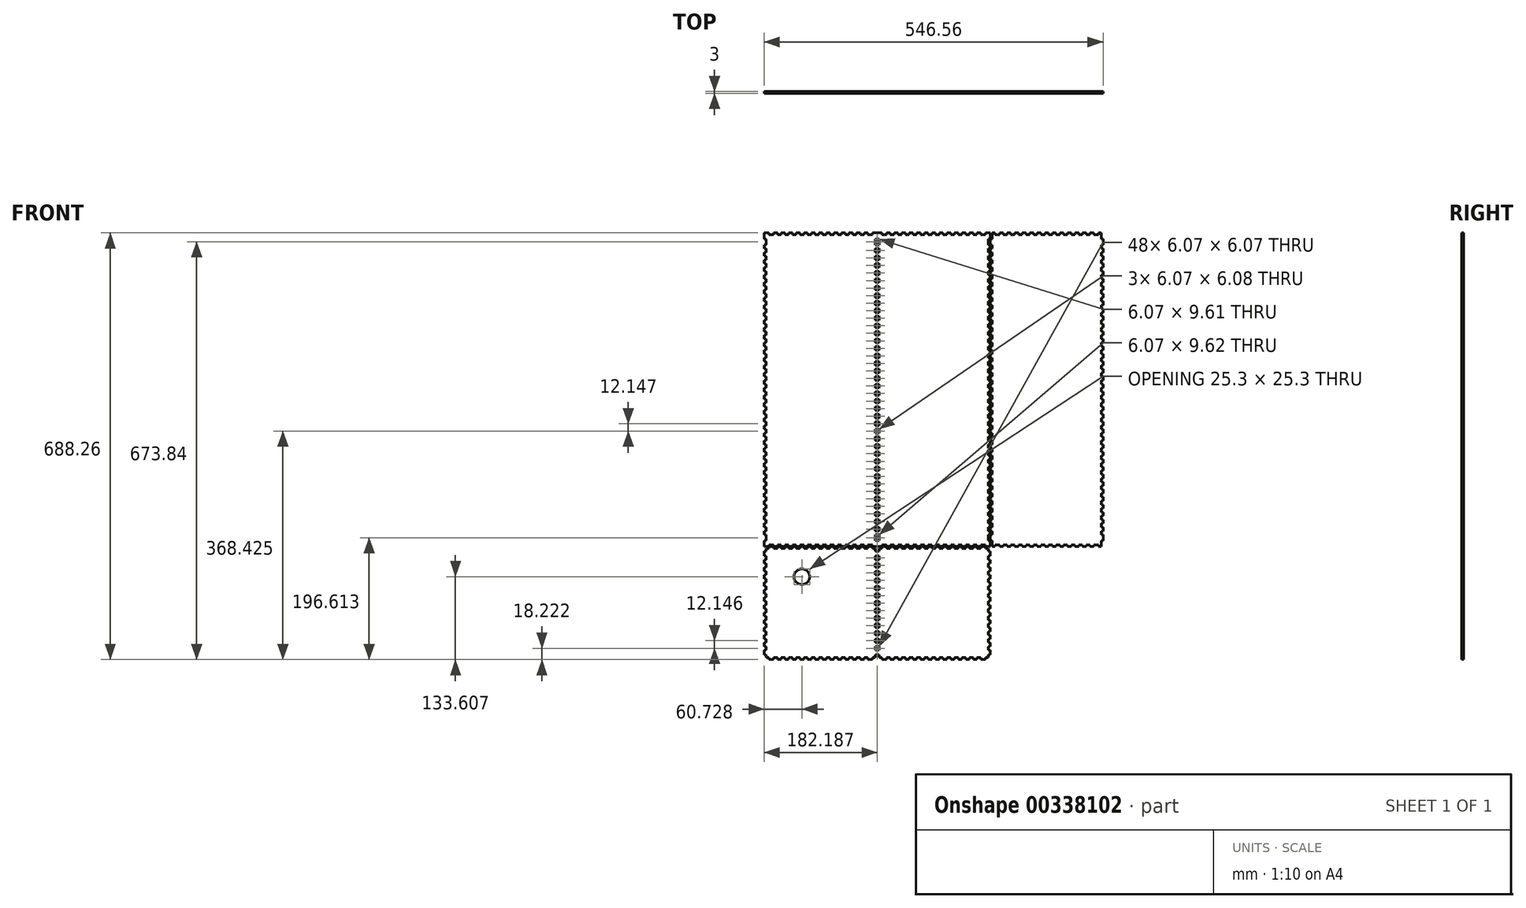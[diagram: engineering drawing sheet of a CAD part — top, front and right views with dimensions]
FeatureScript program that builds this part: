
annotation { "Feature Type Name" : "Feature", "Feature Type Description" : "" }
export const myFeature = defineFeature(function(context is Context, id is Id, definition is map)
    precondition{}
    {
        {
            var Q0;
            Q0=qCreatedBy(makeId("Front.planeOp"),FACE);
            var sketch = newSketch(context, id + "F0", { "sketchPlane" : qUnion([Q0])});
            skLineSegment(sketch, "E0", {"start": v(-273.28, 506.07) * mm, "end": v(-265.69, 506.07) * mm});
            skLineSegment(sketch, "E1", {"start": v(-265.69, 506.07) * mm, "end": v(-265.69, 503.04) * mm});
            skLineSegment(sketch, "E2", {"start": v(-265.69, 503.04) * mm, "end": v(-258.1, 503.04) * mm});
            skLineSegment(sketch, "E3", {"start": v(-258.1, 503.04) * mm, "end": v(-258.1, 506.07) * mm});
            skLineSegment(sketch, "E4", {"start": v(-258.1, 506.07) * mm, "end": v(-252.03, 506.07) * mm});
            skLineSegment(sketch, "E5", {"start": v(-252.03, 506.07) * mm, "end": v(-252.03, 503.04) * mm});
            skLineSegment(sketch, "E6", {"start": v(-252.03, 503.04) * mm, "end": v(-245.95, 503.04) * mm});
            skLineSegment(sketch, "E7", {"start": v(-245.95, 503.04) * mm, "end": v(-245.95, 506.07) * mm});
            skLineSegment(sketch, "E8", {"start": v(-245.95, 506.07) * mm, "end": v(-239.88, 506.07) * mm});
            skLineSegment(sketch, "E9", {"start": v(-239.88, 506.07) * mm, "end": v(-239.88, 503.04) * mm});
            skLineSegment(sketch, "E10", {"start": v(-239.88, 503.04) * mm, "end": v(-233.8, 503.04) * mm});
            skLineSegment(sketch, "E11", {"start": v(-233.8, 503.04) * mm, "end": v(-233.8, 506.07) * mm});
            skLineSegment(sketch, "E12", {"start": v(-233.8, 506.07) * mm, "end": v(-227.73, 506.07) * mm});
            skLineSegment(sketch, "E13", {"start": v(-227.73, 506.07) * mm, "end": v(-227.73, 503.04) * mm});
            skLineSegment(sketch, "E14", {"start": v(-227.73, 503.04) * mm, "end": v(-221.66, 503.04) * mm});
            skLineSegment(sketch, "E15", {"start": v(-221.66, 503.04) * mm, "end": v(-221.66, 506.07) * mm});
            skLineSegment(sketch, "E16", {"start": v(-221.66, 506.07) * mm, "end": v(-215.59, 506.07) * mm});
            skLineSegment(sketch, "E17", {"start": v(-215.59, 506.07) * mm, "end": v(-215.59, 503.04) * mm});
            skLineSegment(sketch, "E18", {"start": v(-215.59, 503.04) * mm, "end": v(-209.52, 503.04) * mm});
            skLineSegment(sketch, "E19", {"start": v(-209.52, 503.04) * mm, "end": v(-209.52, 506.07) * mm});
            skLineSegment(sketch, "E20", {"start": v(-209.52, 506.07) * mm, "end": v(-203.44, 506.07) * mm});
            skLineSegment(sketch, "E21", {"start": v(-203.44, 506.07) * mm, "end": v(-203.44, 503.04) * mm});
            skLineSegment(sketch, "E22", {"start": v(-203.44, 503.04) * mm, "end": v(-197.37, 503.04) * mm});
            skLineSegment(sketch, "E23", {"start": v(-197.37, 503.04) * mm, "end": v(-197.37, 506.07) * mm});
            skLineSegment(sketch, "E24", {"start": v(-197.37, 506.07) * mm, "end": v(-191.3, 506.07) * mm});
            skLineSegment(sketch, "E25", {"start": v(-191.3, 506.07) * mm, "end": v(-191.3, 503.04) * mm});
            skLineSegment(sketch, "E26", {"start": v(-191.3, 503.04) * mm, "end": v(-185.22, 503.04) * mm});
            skLineSegment(sketch, "E27", {"start": v(-185.22, 503.04) * mm, "end": v(-185.22, 506.07) * mm});
            skLineSegment(sketch, "E28", {"start": v(-185.22, 506.07) * mm, "end": v(-179.15, 506.07) * mm});
            skLineSegment(sketch, "E29", {"start": v(-179.15, 506.07) * mm, "end": v(-179.15, 503.04) * mm});
            skLineSegment(sketch, "E30", {"start": v(-179.15, 503.04) * mm, "end": v(-173.08, 503.04) * mm});
            skLineSegment(sketch, "E31", {"start": v(-173.08, 503.04) * mm, "end": v(-173.08, 506.07) * mm});
            skLineSegment(sketch, "E32", {"start": v(-173.08, 506.07) * mm, "end": v(-167, 506.07) * mm});
            skLineSegment(sketch, "E33", {"start": v(-167, 506.07) * mm, "end": v(-167, 503.04) * mm});
            skLineSegment(sketch, "E34", {"start": v(-167, 503.04) * mm, "end": v(-160.93, 503.04) * mm});
            skLineSegment(sketch, "E35", {"start": v(-160.93, 503.04) * mm, "end": v(-160.93, 506.07) * mm});
            skLineSegment(sketch, "E36", {"start": v(-160.93, 506.07) * mm, "end": v(-154.86, 506.07) * mm});
            skLineSegment(sketch, "E37", {"start": v(-154.86, 506.07) * mm, "end": v(-154.86, 503.04) * mm});
            skLineSegment(sketch, "E38", {"start": v(-154.86, 503.04) * mm, "end": v(-148.79, 503.04) * mm});
            skLineSegment(sketch, "E39", {"start": v(-148.79, 503.04) * mm, "end": v(-148.79, 506.07) * mm});
            skLineSegment(sketch, "E40", {"start": v(-148.79, 506.07) * mm, "end": v(-142.71, 506.07) * mm});
            skLineSegment(sketch, "E41", {"start": v(-142.71, 506.07) * mm, "end": v(-142.71, 503.04) * mm});
            skLineSegment(sketch, "E42", {"start": v(-142.71, 503.04) * mm, "end": v(-136.64, 503.04) * mm});
            skLineSegment(sketch, "E43", {"start": v(-136.64, 503.04) * mm, "end": v(-136.64, 506.07) * mm});
            skLineSegment(sketch, "E44", {"start": v(-136.64, 506.07) * mm, "end": v(-130.57, 506.07) * mm});
            skLineSegment(sketch, "E45", {"start": v(-130.57, 506.07) * mm, "end": v(-130.57, 503.04) * mm});
            skLineSegment(sketch, "E46", {"start": v(-130.57, 503.04) * mm, "end": v(-124.5, 503.04) * mm});
            skLineSegment(sketch, "E47", {"start": v(-124.5, 503.04) * mm, "end": v(-124.5, 506.07) * mm});
            skLineSegment(sketch, "E48", {"start": v(-124.5, 506.07) * mm, "end": v(-118.42, 506.07) * mm});
            skLineSegment(sketch, "E49", {"start": v(-118.42, 506.07) * mm, "end": v(-118.42, 503.04) * mm});
            skLineSegment(sketch, "E50", {"start": v(-118.42, 503.04) * mm, "end": v(-112.35, 503.04) * mm});
            skLineSegment(sketch, "E51", {"start": v(-112.35, 503.04) * mm, "end": v(-112.35, 506.07) * mm});
            skLineSegment(sketch, "E52", {"start": v(-112.35, 506.07) * mm, "end": v(-106.28, 506.07) * mm});
            skLineSegment(sketch, "E53", {"start": v(-106.28, 506.07) * mm, "end": v(-106.28, 503.04) * mm});
            skLineSegment(sketch, "E54", {"start": v(-106.28, 503.04) * mm, "end": v(-98.68, 503.04) * mm});
            skLineSegment(sketch, "E55", {"start": v(-98.68, 503.04) * mm, "end": v(-98.68, 506.07) * mm});
            skLineSegment(sketch, "E56", {"start": v(-98.68, 506.07) * mm, "end": v(-91.1, 506.07) * mm});
            skLineSegment(sketch, "E57", {"start": v(-91.1, 506.07) * mm, "end": v(-91.1, 496.46) * mm});
            skLineSegment(sketch, "E58", {"start": v(-91.1, 496.46) * mm, "end": v(-94.13, 496.46) * mm});
            skLineSegment(sketch, "E59", {"start": v(-94.13, 496.46) * mm, "end": v(-94.13, 486.84) * mm});
            skLineSegment(sketch, "E60", {"start": v(-94.13, 486.84) * mm, "end": v(-91.1, 486.84) * mm});
            skLineSegment(sketch, "E61", {"start": v(-91.1, 486.84) * mm, "end": v(-91.1, 480.77) * mm});
            skLineSegment(sketch, "E62", {"start": v(-91.1, 480.77) * mm, "end": v(-94.13, 480.77) * mm});
            skLineSegment(sketch, "E63", {"start": v(-94.13, 480.77) * mm, "end": v(-94.13, 474.7) * mm});
            skLineSegment(sketch, "E64", {"start": v(-94.13, 474.7) * mm, "end": v(-91.1, 474.7) * mm});
            skLineSegment(sketch, "E65", {"start": v(-91.1, 474.7) * mm, "end": v(-91.1, 468.62) * mm});
            skLineSegment(sketch, "E66", {"start": v(-91.1, 468.62) * mm, "end": v(-94.13, 468.62) * mm});
            skLineSegment(sketch, "E67", {"start": v(-94.13, 468.62) * mm, "end": v(-94.13, 462.55) * mm});
            skLineSegment(sketch, "E68", {"start": v(-94.13, 462.55) * mm, "end": v(-91.1, 462.55) * mm});
            skLineSegment(sketch, "E69", {"start": v(-91.1, 462.55) * mm, "end": v(-91.1, 456.48) * mm});
            skLineSegment(sketch, "E70", {"start": v(-91.1, 456.48) * mm, "end": v(-94.13, 456.48) * mm});
            skLineSegment(sketch, "E71", {"start": v(-94.13, 456.48) * mm, "end": v(-94.13, 450.4) * mm});
            skLineSegment(sketch, "E72", {"start": v(-94.13, 450.4) * mm, "end": v(-91.1, 450.4) * mm});
            skLineSegment(sketch, "E73", {"start": v(-91.1, 450.4) * mm, "end": v(-91.1, 444.33) * mm});
            skLineSegment(sketch, "E74", {"start": v(-91.1, 444.33) * mm, "end": v(-94.13, 444.33) * mm});
            skLineSegment(sketch, "E75", {"start": v(-94.13, 444.33) * mm, "end": v(-94.13, 438.26) * mm});
            skLineSegment(sketch, "E76", {"start": v(-94.13, 438.26) * mm, "end": v(-91.1, 438.26) * mm});
            skLineSegment(sketch, "E77", {"start": v(-91.1, 438.26) * mm, "end": v(-91.1, 432.18) * mm});
            skLineSegment(sketch, "E78", {"start": v(-91.1, 432.18) * mm, "end": v(-94.13, 432.18) * mm});
            skLineSegment(sketch, "E79", {"start": v(-94.13, 432.18) * mm, "end": v(-94.13, 426.11) * mm});
            skLineSegment(sketch, "E80", {"start": v(-94.13, 426.11) * mm, "end": v(-91.1, 426.11) * mm});
            skLineSegment(sketch, "E81", {"start": v(-91.1, 426.11) * mm, "end": v(-91.1, 420.04) * mm});
            skLineSegment(sketch, "E82", {"start": v(-91.1, 420.04) * mm, "end": v(-94.13, 420.04) * mm});
            skLineSegment(sketch, "E83", {"start": v(-94.13, 420.04) * mm, "end": v(-94.13, 413.97) * mm});
            skLineSegment(sketch, "E84", {"start": v(-94.13, 413.97) * mm, "end": v(-91.1, 413.97) * mm});
            skLineSegment(sketch, "E85", {"start": v(-91.1, 413.97) * mm, "end": v(-91.1, 407.9) * mm});
            skLineSegment(sketch, "E86", {"start": v(-91.1, 407.9) * mm, "end": v(-94.13, 407.9) * mm});
            skLineSegment(sketch, "E87", {"start": v(-94.13, 407.9) * mm, "end": v(-94.13, 401.82) * mm});
            skLineSegment(sketch, "E88", {"start": v(-94.13, 401.82) * mm, "end": v(-91.1, 401.82) * mm});
            skLineSegment(sketch, "E89", {"start": v(-91.1, 401.82) * mm, "end": v(-91.1, 395.75) * mm});
            skLineSegment(sketch, "E90", {"start": v(-91.1, 395.75) * mm, "end": v(-94.13, 395.75) * mm});
            skLineSegment(sketch, "E91", {"start": v(-94.13, 395.75) * mm, "end": v(-94.13, 389.68) * mm});
            skLineSegment(sketch, "E92", {"start": v(-94.13, 389.68) * mm, "end": v(-91.1, 389.68) * mm});
            skLineSegment(sketch, "E93", {"start": v(-91.1, 389.68) * mm, "end": v(-91.1, 383.6) * mm});
            skLineSegment(sketch, "E94", {"start": v(-91.1, 383.6) * mm, "end": v(-94.13, 383.6) * mm});
            skLineSegment(sketch, "E95", {"start": v(-94.13, 383.6) * mm, "end": v(-94.13, 377.53) * mm});
            skLineSegment(sketch, "E96", {"start": v(-94.13, 377.53) * mm, "end": v(-91.1, 377.53) * mm});
            skLineSegment(sketch, "E97", {"start": v(-91.1, 377.53) * mm, "end": v(-91.1, 371.46) * mm});
            skLineSegment(sketch, "E98", {"start": v(-91.1, 371.46) * mm, "end": v(-94.13, 371.46) * mm});
            skLineSegment(sketch, "E99", {"start": v(-94.13, 371.46) * mm, "end": v(-94.13, 365.39) * mm});
            skLineSegment(sketch, "E100", {"start": v(-94.13, 365.39) * mm, "end": v(-91.1, 365.39) * mm});
            skLineSegment(sketch, "E101", {"start": v(-91.1, 365.39) * mm, "end": v(-91.1, 359.31) * mm});
            skLineSegment(sketch, "E102", {"start": v(-91.1, 359.31) * mm, "end": v(-94.13, 359.31) * mm});
            skLineSegment(sketch, "E103", {"start": v(-94.13, 359.31) * mm, "end": v(-94.13, 353.24) * mm});
            skLineSegment(sketch, "E104", {"start": v(-94.13, 353.24) * mm, "end": v(-91.1, 353.24) * mm});
            skLineSegment(sketch, "E105", {"start": v(-91.1, 353.24) * mm, "end": v(-91.1, 347.16) * mm});
            skLineSegment(sketch, "E106", {"start": v(-91.1, 347.16) * mm, "end": v(-94.13, 347.16) * mm});
            skLineSegment(sketch, "E107", {"start": v(-94.13, 347.16) * mm, "end": v(-94.13, 341.1) * mm});
            skLineSegment(sketch, "E108", {"start": v(-94.13, 341.1) * mm, "end": v(-91.1, 341.1) * mm});
            skLineSegment(sketch, "E109", {"start": v(-91.1, 341.1) * mm, "end": v(-91.1, 335.02) * mm});
            skLineSegment(sketch, "E110", {"start": v(-91.1, 335.02) * mm, "end": v(-94.13, 335.02) * mm});
            skLineSegment(sketch, "E111", {"start": v(-94.13, 335.02) * mm, "end": v(-94.13, 328.95) * mm});
            skLineSegment(sketch, "E112", {"start": v(-94.13, 328.95) * mm, "end": v(-91.1, 328.95) * mm});
            skLineSegment(sketch, "E113", {"start": v(-91.1, 328.95) * mm, "end": v(-91.1, 322.87) * mm});
            skLineSegment(sketch, "E114", {"start": v(-91.1, 322.87) * mm, "end": v(-94.13, 322.87) * mm});
            skLineSegment(sketch, "E115", {"start": v(-94.13, 322.87) * mm, "end": v(-94.13, 316.8) * mm});
            skLineSegment(sketch, "E116", {"start": v(-94.13, 316.8) * mm, "end": v(-91.1, 316.8) * mm});
            skLineSegment(sketch, "E117", {"start": v(-91.1, 316.8) * mm, "end": v(-91.1, 310.73) * mm});
            skLineSegment(sketch, "E118", {"start": v(-91.1, 310.73) * mm, "end": v(-94.13, 310.73) * mm});
            skLineSegment(sketch, "E119", {"start": v(-94.13, 310.73) * mm, "end": v(-94.13, 304.66) * mm});
            skLineSegment(sketch, "E120", {"start": v(-94.13, 304.66) * mm, "end": v(-91.1, 304.66) * mm});
            skLineSegment(sketch, "E121", {"start": v(-91.1, 304.66) * mm, "end": v(-91.1, 298.58) * mm});
            skLineSegment(sketch, "E122", {"start": v(-91.1, 298.58) * mm, "end": v(-94.13, 298.58) * mm});
            skLineSegment(sketch, "E123", {"start": v(-94.13, 298.58) * mm, "end": v(-94.13, 292.51) * mm});
            skLineSegment(sketch, "E124", {"start": v(-94.13, 292.51) * mm, "end": v(-91.1, 292.51) * mm});
            skLineSegment(sketch, "E125", {"start": v(-91.1, 292.51) * mm, "end": v(-91.1, 286.44) * mm});
            skLineSegment(sketch, "E126", {"start": v(-91.1, 286.44) * mm, "end": v(-94.13, 286.44) * mm});
            skLineSegment(sketch, "E127", {"start": v(-94.13, 286.44) * mm, "end": v(-94.13, 280.37) * mm});
            skLineSegment(sketch, "E128", {"start": v(-94.13, 280.37) * mm, "end": v(-91.1, 280.37) * mm});
            skLineSegment(sketch, "E129", {"start": v(-91.1, 280.37) * mm, "end": v(-91.1, 274.3) * mm});
            skLineSegment(sketch, "E130", {"start": v(-91.1, 274.3) * mm, "end": v(-94.13, 274.3) * mm});
            skLineSegment(sketch, "E131", {"start": v(-94.13, 274.3) * mm, "end": v(-94.13, 268.22) * mm});
            skLineSegment(sketch, "E132", {"start": v(-94.13, 268.22) * mm, "end": v(-91.1, 268.22) * mm});
            skLineSegment(sketch, "E133", {"start": v(-91.1, 268.22) * mm, "end": v(-91.1, 262.15) * mm});
            skLineSegment(sketch, "E134", {"start": v(-91.1, 262.15) * mm, "end": v(-94.13, 262.15) * mm});
            skLineSegment(sketch, "E135", {"start": v(-94.13, 262.15) * mm, "end": v(-94.13, 256.07) * mm});
            skLineSegment(sketch, "E136", {"start": v(-94.13, 256.07) * mm, "end": v(-91.1, 256.07) * mm});
            skLineSegment(sketch, "E137", {"start": v(-91.1, 256.07) * mm, "end": v(-91.1, 250) * mm});
            skLineSegment(sketch, "E138", {"start": v(-91.1, 250) * mm, "end": v(-94.13, 250) * mm});
            skLineSegment(sketch, "E139", {"start": v(-94.13, 250) * mm, "end": v(-94.13, 243.93) * mm});
            skLineSegment(sketch, "E140", {"start": v(-94.13, 243.93) * mm, "end": v(-91.1, 243.93) * mm});
            skLineSegment(sketch, "E141", {"start": v(-91.1, 243.93) * mm, "end": v(-91.1, 237.85) * mm});
            skLineSegment(sketch, "E142", {"start": v(-91.1, 237.85) * mm, "end": v(-94.13, 237.85) * mm});
            skLineSegment(sketch, "E143", {"start": v(-94.13, 237.85) * mm, "end": v(-94.13, 231.78) * mm});
            skLineSegment(sketch, "E144", {"start": v(-94.13, 231.78) * mm, "end": v(-91.1, 231.78) * mm});
            skLineSegment(sketch, "E145", {"start": v(-91.1, 231.78) * mm, "end": v(-91.1, 225.7) * mm});
            skLineSegment(sketch, "E146", {"start": v(-91.1, 225.7) * mm, "end": v(-94.13, 225.7) * mm});
            skLineSegment(sketch, "E147", {"start": v(-94.13, 225.7) * mm, "end": v(-94.13, 219.64) * mm});
            skLineSegment(sketch, "E148", {"start": v(-94.13, 219.64) * mm, "end": v(-91.1, 219.64) * mm});
            skLineSegment(sketch, "E149", {"start": v(-91.1, 219.64) * mm, "end": v(-91.1, 213.56) * mm});
            skLineSegment(sketch, "E150", {"start": v(-91.1, 213.56) * mm, "end": v(-94.13, 213.56) * mm});
            skLineSegment(sketch, "E151", {"start": v(-94.13, 213.56) * mm, "end": v(-94.13, 207.49) * mm});
            skLineSegment(sketch, "E152", {"start": v(-94.13, 207.49) * mm, "end": v(-91.1, 207.49) * mm});
            skLineSegment(sketch, "E153", {"start": v(-91.1, 207.49) * mm, "end": v(-91.1, 201.42) * mm});
            skLineSegment(sketch, "E154", {"start": v(-91.1, 201.42) * mm, "end": v(-94.13, 201.42) * mm});
            skLineSegment(sketch, "E155", {"start": v(-94.13, 201.42) * mm, "end": v(-94.13, 195.34) * mm});
            skLineSegment(sketch, "E156", {"start": v(-94.13, 195.34) * mm, "end": v(-91.1, 195.34) * mm});
            skLineSegment(sketch, "E157", {"start": v(-91.1, 195.34) * mm, "end": v(-91.1, 189.27) * mm});
            skLineSegment(sketch, "E158", {"start": v(-91.1, 189.27) * mm, "end": v(-94.13, 189.27) * mm});
            skLineSegment(sketch, "E159", {"start": v(-94.13, 189.27) * mm, "end": v(-94.13, 183.2) * mm});
            skLineSegment(sketch, "E160", {"start": v(-94.13, 183.2) * mm, "end": v(-91.1, 183.2) * mm});
            skLineSegment(sketch, "E161", {"start": v(-91.1, 183.2) * mm, "end": v(-91.1, 177.13) * mm});
            skLineSegment(sketch, "E162", {"start": v(-91.1, 177.13) * mm, "end": v(-94.13, 177.13) * mm});
            skLineSegment(sketch, "E163", {"start": v(-94.13, 177.13) * mm, "end": v(-94.13, 171.06) * mm});
            skLineSegment(sketch, "E164", {"start": v(-94.13, 171.06) * mm, "end": v(-91.1, 171.06) * mm});
            skLineSegment(sketch, "E165", {"start": v(-91.1, 171.06) * mm, "end": v(-91.1, 164.98) * mm});
            skLineSegment(sketch, "E166", {"start": v(-91.1, 164.98) * mm, "end": v(-94.13, 164.98) * mm});
            skLineSegment(sketch, "E167", {"start": v(-94.13, 164.98) * mm, "end": v(-94.13, 158.9) * mm});
            skLineSegment(sketch, "E168", {"start": v(-94.13, 158.9) * mm, "end": v(-91.1, 158.9) * mm});
            skLineSegment(sketch, "E169", {"start": v(-91.1, 158.9) * mm, "end": v(-91.1, 152.83) * mm});
            skLineSegment(sketch, "E170", {"start": v(-91.1, 152.83) * mm, "end": v(-94.13, 152.83) * mm});
            skLineSegment(sketch, "E171", {"start": v(-94.13, 152.83) * mm, "end": v(-94.13, 146.76) * mm});
            skLineSegment(sketch, "E172", {"start": v(-94.13, 146.76) * mm, "end": v(-91.1, 146.76) * mm});
            skLineSegment(sketch, "E173", {"start": v(-91.1, 146.76) * mm, "end": v(-91.1, 140.69) * mm});
            skLineSegment(sketch, "E174", {"start": v(-91.1, 140.69) * mm, "end": v(-94.13, 140.69) * mm});
            skLineSegment(sketch, "E175", {"start": v(-94.13, 140.69) * mm, "end": v(-94.13, 134.62) * mm});
            skLineSegment(sketch, "E176", {"start": v(-94.13, 134.62) * mm, "end": v(-91.1, 134.62) * mm});
            skLineSegment(sketch, "E177", {"start": v(-91.1, 134.62) * mm, "end": v(-91.1, 128.54) * mm});
            skLineSegment(sketch, "E178", {"start": v(-91.1, 128.54) * mm, "end": v(-94.13, 128.54) * mm});
            skLineSegment(sketch, "E179", {"start": v(-94.13, 128.54) * mm, "end": v(-94.13, 122.47) * mm});
            skLineSegment(sketch, "E180", {"start": v(-94.13, 122.47) * mm, "end": v(-91.1, 122.47) * mm});
            skLineSegment(sketch, "E181", {"start": v(-91.1, 122.47) * mm, "end": v(-91.1, 116.4) * mm});
            skLineSegment(sketch, "E182", {"start": v(-91.1, 116.4) * mm, "end": v(-94.13, 116.4) * mm});
            skLineSegment(sketch, "E183", {"start": v(-94.13, 116.4) * mm, "end": v(-94.13, 110.32) * mm});
            skLineSegment(sketch, "E184", {"start": v(-94.13, 110.32) * mm, "end": v(-91.1, 110.32) * mm});
            skLineSegment(sketch, "E185", {"start": v(-91.1, 110.32) * mm, "end": v(-91.1, 104.25) * mm});
            skLineSegment(sketch, "E186", {"start": v(-91.1, 104.25) * mm, "end": v(-94.13, 104.25) * mm});
            skLineSegment(sketch, "E187", {"start": v(-94.13, 104.25) * mm, "end": v(-94.13, 98.18) * mm});
            skLineSegment(sketch, "E188", {"start": v(-94.13, 98.18) * mm, "end": v(-91.1, 98.18) * mm});
            skLineSegment(sketch, "E189", {"start": v(-91.1, 98.18) * mm, "end": v(-91.1, 92.1) * mm});
            skLineSegment(sketch, "E190", {"start": v(-91.1, 92.1) * mm, "end": v(-94.13, 92.1) * mm});
            skLineSegment(sketch, "E191", {"start": v(-94.13, 92.1) * mm, "end": v(-94.13, 86.03) * mm});
            skLineSegment(sketch, "E192", {"start": v(-94.13, 86.03) * mm, "end": v(-91.1, 86.03) * mm});
            skLineSegment(sketch, "E193", {"start": v(-91.1, 86.03) * mm, "end": v(-91.1, 79.96) * mm});
            skLineSegment(sketch, "E194", {"start": v(-91.1, 79.96) * mm, "end": v(-94.13, 79.96) * mm});
            skLineSegment(sketch, "E195", {"start": v(-94.13, 79.96) * mm, "end": v(-94.13, 73.89) * mm});
            skLineSegment(sketch, "E196", {"start": v(-94.13, 73.89) * mm, "end": v(-91.1, 73.89) * mm});
            skLineSegment(sketch, "E197", {"start": v(-91.1, 73.89) * mm, "end": v(-91.1, 67.81) * mm});
            skLineSegment(sketch, "E198", {"start": v(-91.1, 67.81) * mm, "end": v(-94.13, 67.81) * mm});
            skLineSegment(sketch, "E199", {"start": v(-94.13, 67.81) * mm, "end": v(-94.13, 61.74) * mm});
            skLineSegment(sketch, "E200", {"start": v(-94.13, 61.74) * mm, "end": v(-91.1, 61.74) * mm});
            skLineSegment(sketch, "E201", {"start": v(-91.1, 61.74) * mm, "end": v(-91.1, 55.67) * mm});
            skLineSegment(sketch, "E202", {"start": v(-91.1, 55.67) * mm, "end": v(-94.13, 55.67) * mm});
            skLineSegment(sketch, "E203", {"start": v(-94.13, 55.67) * mm, "end": v(-94.13, 49.6) * mm});
            skLineSegment(sketch, "E204", {"start": v(-94.13, 49.6) * mm, "end": v(-91.1, 49.6) * mm});
            skLineSegment(sketch, "E205", {"start": v(-91.1, 49.6) * mm, "end": v(-91.1, 43.52) * mm});
            skLineSegment(sketch, "E206", {"start": v(-91.1, 43.52) * mm, "end": v(-94.13, 43.52) * mm});
            skLineSegment(sketch, "E207", {"start": v(-94.13, 43.52) * mm, "end": v(-94.13, 37.45) * mm});
            skLineSegment(sketch, "E208", {"start": v(-94.13, 37.45) * mm, "end": v(-91.1, 37.45) * mm});
            skLineSegment(sketch, "E209", {"start": v(-91.1, 37.45) * mm, "end": v(-91.1, 31.38) * mm});
            skLineSegment(sketch, "E210", {"start": v(-91.1, 31.38) * mm, "end": v(-94.13, 31.38) * mm});
            skLineSegment(sketch, "E211", {"start": v(-94.13, 31.38) * mm, "end": v(-94.13, 25.3) * mm});
            skLineSegment(sketch, "E212", {"start": v(-94.13, 25.3) * mm, "end": v(-91.1, 25.3) * mm});
            skLineSegment(sketch, "E213", {"start": v(-91.1, 25.3) * mm, "end": v(-91.1, 19.23) * mm});
            skLineSegment(sketch, "E214", {"start": v(-91.1, 19.23) * mm, "end": v(-94.13, 19.23) * mm});
            skLineSegment(sketch, "E215", {"start": v(-94.13, 19.23) * mm, "end": v(-94.13, 9.62) * mm});
            skLineSegment(sketch, "E216", {"start": v(-94.13, 9.62) * mm, "end": v(-91.1, 9.62) * mm});
            skLineSegment(sketch, "E217", {"start": v(-91.1, 9.62) * mm, "end": v(-91.1, 0) * mm});
            skLineSegment(sketch, "E218", {"start": v(-91.1, 0) * mm, "end": v(-98.68, 0) * mm});
            skLineSegment(sketch, "E219", {"start": v(-98.68, 0) * mm, "end": v(-98.68, 3.04) * mm});
            skLineSegment(sketch, "E220", {"start": v(-98.68, 3.04) * mm, "end": v(-106.28, 3.04) * mm});
            skLineSegment(sketch, "E221", {"start": v(-106.28, 3.04) * mm, "end": v(-106.28, 0) * mm});
            skLineSegment(sketch, "E222", {"start": v(-106.28, 0) * mm, "end": v(-112.35, 0) * mm});
            skLineSegment(sketch, "E223", {"start": v(-112.35, 0) * mm, "end": v(-112.35, 3.04) * mm});
            skLineSegment(sketch, "E224", {"start": v(-112.35, 3.04) * mm, "end": v(-118.42, 3.04) * mm});
            skLineSegment(sketch, "E225", {"start": v(-118.42, 3.04) * mm, "end": v(-118.42, 0) * mm});
            skLineSegment(sketch, "E226", {"start": v(-118.42, 0) * mm, "end": v(-124.5, 0) * mm});
            skLineSegment(sketch, "E227", {"start": v(-124.5, 0) * mm, "end": v(-124.5, 3.04) * mm});
            skLineSegment(sketch, "E228", {"start": v(-124.5, 3.04) * mm, "end": v(-130.57, 3.04) * mm});
            skLineSegment(sketch, "E229", {"start": v(-130.57, 3.04) * mm, "end": v(-130.57, 0) * mm});
            skLineSegment(sketch, "E230", {"start": v(-130.57, 0) * mm, "end": v(-136.64, 0) * mm});
            skLineSegment(sketch, "E231", {"start": v(-136.64, 0) * mm, "end": v(-136.64, 3.04) * mm});
            skLineSegment(sketch, "E232", {"start": v(-136.64, 3.04) * mm, "end": v(-142.71, 3.04) * mm});
            skLineSegment(sketch, "E233", {"start": v(-142.71, 3.04) * mm, "end": v(-142.71, 0) * mm});
            skLineSegment(sketch, "E234", {"start": v(-142.71, 0) * mm, "end": v(-148.79, 0) * mm});
            skLineSegment(sketch, "E235", {"start": v(-148.79, 0) * mm, "end": v(-148.79, 3.04) * mm});
            skLineSegment(sketch, "E236", {"start": v(-148.79, 3.04) * mm, "end": v(-154.86, 3.04) * mm});
            skLineSegment(sketch, "E237", {"start": v(-154.86, 3.04) * mm, "end": v(-154.86, 0) * mm});
            skLineSegment(sketch, "E238", {"start": v(-154.86, 0) * mm, "end": v(-160.93, 0) * mm});
            skLineSegment(sketch, "E239", {"start": v(-160.93, 0) * mm, "end": v(-160.93, 3.04) * mm});
            skLineSegment(sketch, "E240", {"start": v(-160.93, 3.04) * mm, "end": v(-167, 3.04) * mm});
            skLineSegment(sketch, "E241", {"start": v(-167, 3.04) * mm, "end": v(-167, 0) * mm});
            skLineSegment(sketch, "E242", {"start": v(-167, 0) * mm, "end": v(-173.08, 0) * mm});
            skLineSegment(sketch, "E243", {"start": v(-173.08, 0) * mm, "end": v(-173.08, 3.04) * mm});
            skLineSegment(sketch, "E244", {"start": v(-173.08, 3.04) * mm, "end": v(-179.15, 3.04) * mm});
            skLineSegment(sketch, "E245", {"start": v(-179.15, 3.04) * mm, "end": v(-179.15, 0) * mm});
            skLineSegment(sketch, "E246", {"start": v(-179.15, 0) * mm, "end": v(-185.22, 0) * mm});
            skLineSegment(sketch, "E247", {"start": v(-185.22, 0) * mm, "end": v(-185.22, 3.04) * mm});
            skLineSegment(sketch, "E248", {"start": v(-185.22, 3.04) * mm, "end": v(-191.3, 3.04) * mm});
            skLineSegment(sketch, "E249", {"start": v(-191.3, 3.04) * mm, "end": v(-191.3, 0) * mm});
            skLineSegment(sketch, "E250", {"start": v(-191.3, 0) * mm, "end": v(-197.37, 0) * mm});
            skLineSegment(sketch, "E251", {"start": v(-197.37, 0) * mm, "end": v(-197.37, 3.04) * mm});
            skLineSegment(sketch, "E252", {"start": v(-197.37, 3.04) * mm, "end": v(-203.44, 3.04) * mm});
            skLineSegment(sketch, "E253", {"start": v(-203.44, 3.04) * mm, "end": v(-203.44, 0) * mm});
            skLineSegment(sketch, "E254", {"start": v(-203.44, 0) * mm, "end": v(-209.52, 0) * mm});
            skLineSegment(sketch, "E255", {"start": v(-209.52, 0) * mm, "end": v(-209.52, 3.04) * mm});
            skLineSegment(sketch, "E256", {"start": v(-209.52, 3.04) * mm, "end": v(-215.59, 3.04) * mm});
            skLineSegment(sketch, "E257", {"start": v(-215.59, 3.04) * mm, "end": v(-215.59, 0) * mm});
            skLineSegment(sketch, "E258", {"start": v(-215.59, 0) * mm, "end": v(-221.66, 0) * mm});
            skLineSegment(sketch, "E259", {"start": v(-221.66, 0) * mm, "end": v(-221.66, 3.04) * mm});
            skLineSegment(sketch, "E260", {"start": v(-221.66, 3.04) * mm, "end": v(-227.73, 3.04) * mm});
            skLineSegment(sketch, "E261", {"start": v(-227.73, 3.04) * mm, "end": v(-227.73, 0) * mm});
            skLineSegment(sketch, "E262", {"start": v(-227.73, 0) * mm, "end": v(-233.8, 0) * mm});
            skLineSegment(sketch, "E263", {"start": v(-233.8, 0) * mm, "end": v(-233.8, 3.04) * mm});
            skLineSegment(sketch, "E264", {"start": v(-233.8, 3.04) * mm, "end": v(-239.88, 3.04) * mm});
            skLineSegment(sketch, "E265", {"start": v(-239.88, 3.04) * mm, "end": v(-239.88, 0) * mm});
            skLineSegment(sketch, "E266", {"start": v(-239.88, 0) * mm, "end": v(-245.95, 0) * mm});
            skLineSegment(sketch, "E267", {"start": v(-245.95, 0) * mm, "end": v(-245.95, 3.04) * mm});
            skLineSegment(sketch, "E268", {"start": v(-245.95, 3.04) * mm, "end": v(-252.03, 3.04) * mm});
            skLineSegment(sketch, "E269", {"start": v(-252.03, 3.04) * mm, "end": v(-252.03, 0) * mm});
            skLineSegment(sketch, "E270", {"start": v(-252.03, 0) * mm, "end": v(-258.1, 0) * mm});
            skLineSegment(sketch, "E271", {"start": v(-258.1, 0) * mm, "end": v(-258.1, 3.04) * mm});
            skLineSegment(sketch, "E272", {"start": v(-258.1, 3.04) * mm, "end": v(-265.69, 3.04) * mm});
            skLineSegment(sketch, "E273", {"start": v(-265.69, 3.04) * mm, "end": v(-265.69, 0) * mm});
            skLineSegment(sketch, "E274", {"start": v(-265.69, 0) * mm, "end": v(-273.28, 0) * mm});
            skLineSegment(sketch, "E275", {"start": v(-273.28, 0) * mm, "end": v(-273.28, 9.62) * mm});
            skLineSegment(sketch, "E276", {"start": v(-273.28, 9.62) * mm, "end": v(-270.24, 9.62) * mm});
            skLineSegment(sketch, "E277", {"start": v(-270.24, 9.62) * mm, "end": v(-270.24, 19.23) * mm});
            skLineSegment(sketch, "E278", {"start": v(-270.24, 19.23) * mm, "end": v(-273.28, 19.23) * mm});
            skLineSegment(sketch, "E279", {"start": v(-273.28, 19.23) * mm, "end": v(-273.28, 25.3) * mm});
            skLineSegment(sketch, "E280", {"start": v(-273.28, 25.3) * mm, "end": v(-270.24, 25.3) * mm});
            skLineSegment(sketch, "E281", {"start": v(-270.24, 25.3) * mm, "end": v(-270.24, 31.38) * mm});
            skLineSegment(sketch, "E282", {"start": v(-270.24, 31.38) * mm, "end": v(-273.28, 31.38) * mm});
            skLineSegment(sketch, "E283", {"start": v(-273.28, 31.38) * mm, "end": v(-273.28, 37.45) * mm});
            skLineSegment(sketch, "E284", {"start": v(-273.28, 37.45) * mm, "end": v(-270.24, 37.45) * mm});
            skLineSegment(sketch, "E285", {"start": v(-270.24, 37.45) * mm, "end": v(-270.24, 43.52) * mm});
            skLineSegment(sketch, "E286", {"start": v(-270.24, 43.52) * mm, "end": v(-273.28, 43.52) * mm});
            skLineSegment(sketch, "E287", {"start": v(-273.28, 43.52) * mm, "end": v(-273.28, 49.6) * mm});
            skLineSegment(sketch, "E288", {"start": v(-273.28, 49.6) * mm, "end": v(-270.24, 49.6) * mm});
            skLineSegment(sketch, "E289", {"start": v(-270.24, 49.6) * mm, "end": v(-270.24, 55.67) * mm});
            skLineSegment(sketch, "E290", {"start": v(-270.24, 55.67) * mm, "end": v(-273.28, 55.67) * mm});
            skLineSegment(sketch, "E291", {"start": v(-273.28, 55.67) * mm, "end": v(-273.28, 61.74) * mm});
            skLineSegment(sketch, "E292", {"start": v(-273.28, 61.74) * mm, "end": v(-270.24, 61.74) * mm});
            skLineSegment(sketch, "E293", {"start": v(-270.24, 61.74) * mm, "end": v(-270.24, 67.81) * mm});
            skLineSegment(sketch, "E294", {"start": v(-270.24, 67.81) * mm, "end": v(-273.28, 67.81) * mm});
            skLineSegment(sketch, "E295", {"start": v(-273.28, 67.81) * mm, "end": v(-273.28, 73.89) * mm});
            skLineSegment(sketch, "E296", {"start": v(-273.28, 73.89) * mm, "end": v(-270.24, 73.89) * mm});
            skLineSegment(sketch, "E297", {"start": v(-270.24, 73.89) * mm, "end": v(-270.24, 79.96) * mm});
            skLineSegment(sketch, "E298", {"start": v(-270.24, 79.96) * mm, "end": v(-273.28, 79.96) * mm});
            skLineSegment(sketch, "E299", {"start": v(-273.28, 79.96) * mm, "end": v(-273.28, 86.03) * mm});
            skLineSegment(sketch, "E300", {"start": v(-273.28, 86.03) * mm, "end": v(-270.24, 86.03) * mm});
            skLineSegment(sketch, "E301", {"start": v(-270.24, 86.03) * mm, "end": v(-270.24, 92.1) * mm});
            skLineSegment(sketch, "E302", {"start": v(-270.24, 92.1) * mm, "end": v(-273.28, 92.1) * mm});
            skLineSegment(sketch, "E303", {"start": v(-273.28, 92.1) * mm, "end": v(-273.28, 98.18) * mm});
            skLineSegment(sketch, "E304", {"start": v(-273.28, 98.18) * mm, "end": v(-270.24, 98.18) * mm});
            skLineSegment(sketch, "E305", {"start": v(-270.24, 98.18) * mm, "end": v(-270.24, 104.25) * mm});
            skLineSegment(sketch, "E306", {"start": v(-270.24, 104.25) * mm, "end": v(-273.28, 104.25) * mm});
            skLineSegment(sketch, "E307", {"start": v(-273.28, 104.25) * mm, "end": v(-273.28, 110.32) * mm});
            skLineSegment(sketch, "E308", {"start": v(-273.28, 110.32) * mm, "end": v(-270.24, 110.32) * mm});
            skLineSegment(sketch, "E309", {"start": v(-270.24, 110.32) * mm, "end": v(-270.24, 116.4) * mm});
            skLineSegment(sketch, "E310", {"start": v(-270.24, 116.4) * mm, "end": v(-273.28, 116.4) * mm});
            skLineSegment(sketch, "E311", {"start": v(-273.28, 116.4) * mm, "end": v(-273.28, 122.47) * mm});
            skLineSegment(sketch, "E312", {"start": v(-273.28, 122.47) * mm, "end": v(-270.24, 122.47) * mm});
            skLineSegment(sketch, "E313", {"start": v(-270.24, 122.47) * mm, "end": v(-270.24, 128.54) * mm});
            skLineSegment(sketch, "E314", {"start": v(-270.24, 128.54) * mm, "end": v(-273.28, 128.54) * mm});
            skLineSegment(sketch, "E315", {"start": v(-273.28, 128.54) * mm, "end": v(-273.28, 134.62) * mm});
            skLineSegment(sketch, "E316", {"start": v(-273.28, 134.62) * mm, "end": v(-270.24, 134.62) * mm});
            skLineSegment(sketch, "E317", {"start": v(-270.24, 134.62) * mm, "end": v(-270.24, 140.69) * mm});
            skLineSegment(sketch, "E318", {"start": v(-270.24, 140.69) * mm, "end": v(-273.28, 140.69) * mm});
            skLineSegment(sketch, "E319", {"start": v(-273.28, 140.69) * mm, "end": v(-273.28, 146.76) * mm});
            skLineSegment(sketch, "E320", {"start": v(-273.28, 146.76) * mm, "end": v(-270.24, 146.76) * mm});
            skLineSegment(sketch, "E321", {"start": v(-270.24, 146.76) * mm, "end": v(-270.24, 152.83) * mm});
            skLineSegment(sketch, "E322", {"start": v(-270.24, 152.83) * mm, "end": v(-273.28, 152.83) * mm});
            skLineSegment(sketch, "E323", {"start": v(-273.28, 152.83) * mm, "end": v(-273.28, 158.9) * mm});
            skLineSegment(sketch, "E324", {"start": v(-273.28, 158.9) * mm, "end": v(-270.24, 158.9) * mm});
            skLineSegment(sketch, "E325", {"start": v(-270.24, 158.9) * mm, "end": v(-270.24, 164.98) * mm});
            skLineSegment(sketch, "E326", {"start": v(-270.24, 164.98) * mm, "end": v(-273.28, 164.98) * mm});
            skLineSegment(sketch, "E327", {"start": v(-273.28, 164.98) * mm, "end": v(-273.28, 171.06) * mm});
            skLineSegment(sketch, "E328", {"start": v(-273.28, 171.06) * mm, "end": v(-270.24, 171.06) * mm});
            skLineSegment(sketch, "E329", {"start": v(-270.24, 171.06) * mm, "end": v(-270.24, 177.13) * mm});
            skLineSegment(sketch, "E330", {"start": v(-270.24, 177.13) * mm, "end": v(-273.28, 177.13) * mm});
            skLineSegment(sketch, "E331", {"start": v(-273.28, 177.13) * mm, "end": v(-273.28, 183.2) * mm});
            skLineSegment(sketch, "E332", {"start": v(-273.28, 183.2) * mm, "end": v(-270.24, 183.2) * mm});
            skLineSegment(sketch, "E333", {"start": v(-270.24, 183.2) * mm, "end": v(-270.24, 189.27) * mm});
            skLineSegment(sketch, "E334", {"start": v(-270.24, 189.27) * mm, "end": v(-273.28, 189.27) * mm});
            skLineSegment(sketch, "E335", {"start": v(-273.28, 189.27) * mm, "end": v(-273.28, 195.34) * mm});
            skLineSegment(sketch, "E336", {"start": v(-273.28, 195.34) * mm, "end": v(-270.24, 195.34) * mm});
            skLineSegment(sketch, "E337", {"start": v(-270.24, 195.34) * mm, "end": v(-270.24, 201.42) * mm});
            skLineSegment(sketch, "E338", {"start": v(-270.24, 201.42) * mm, "end": v(-273.28, 201.42) * mm});
            skLineSegment(sketch, "E339", {"start": v(-273.28, 201.42) * mm, "end": v(-273.28, 207.49) * mm});
            skLineSegment(sketch, "E340", {"start": v(-273.28, 207.49) * mm, "end": v(-270.24, 207.49) * mm});
            skLineSegment(sketch, "E341", {"start": v(-270.24, 207.49) * mm, "end": v(-270.24, 213.56) * mm});
            skLineSegment(sketch, "E342", {"start": v(-270.24, 213.56) * mm, "end": v(-273.28, 213.56) * mm});
            skLineSegment(sketch, "E343", {"start": v(-273.28, 213.56) * mm, "end": v(-273.28, 219.64) * mm});
            skLineSegment(sketch, "E344", {"start": v(-273.28, 219.64) * mm, "end": v(-270.24, 219.64) * mm});
            skLineSegment(sketch, "E345", {"start": v(-270.24, 219.64) * mm, "end": v(-270.24, 225.7) * mm});
            skLineSegment(sketch, "E346", {"start": v(-270.24, 225.7) * mm, "end": v(-273.28, 225.7) * mm});
            skLineSegment(sketch, "E347", {"start": v(-273.28, 225.7) * mm, "end": v(-273.28, 231.78) * mm});
            skLineSegment(sketch, "E348", {"start": v(-273.28, 231.78) * mm, "end": v(-270.24, 231.78) * mm});
            skLineSegment(sketch, "E349", {"start": v(-270.24, 231.78) * mm, "end": v(-270.24, 237.85) * mm});
            skLineSegment(sketch, "E350", {"start": v(-270.24, 237.85) * mm, "end": v(-273.28, 237.85) * mm});
            skLineSegment(sketch, "E351", {"start": v(-273.28, 237.85) * mm, "end": v(-273.28, 243.93) * mm});
            skLineSegment(sketch, "E352", {"start": v(-273.28, 243.93) * mm, "end": v(-270.24, 243.93) * mm});
            skLineSegment(sketch, "E353", {"start": v(-270.24, 243.93) * mm, "end": v(-270.24, 250) * mm});
            skLineSegment(sketch, "E354", {"start": v(-270.24, 250) * mm, "end": v(-273.28, 250) * mm});
            skLineSegment(sketch, "E355", {"start": v(-273.28, 250) * mm, "end": v(-273.28, 256.07) * mm});
            skLineSegment(sketch, "E356", {"start": v(-273.28, 256.07) * mm, "end": v(-270.24, 256.07) * mm});
            skLineSegment(sketch, "E357", {"start": v(-270.24, 256.07) * mm, "end": v(-270.24, 262.15) * mm});
            skLineSegment(sketch, "E358", {"start": v(-270.24, 262.15) * mm, "end": v(-273.28, 262.15) * mm});
            skLineSegment(sketch, "E359", {"start": v(-273.28, 262.15) * mm, "end": v(-273.28, 268.22) * mm});
            skLineSegment(sketch, "E360", {"start": v(-273.28, 268.22) * mm, "end": v(-270.24, 268.22) * mm});
            skLineSegment(sketch, "E361", {"start": v(-270.24, 268.22) * mm, "end": v(-270.24, 274.3) * mm});
            skLineSegment(sketch, "E362", {"start": v(-270.24, 274.3) * mm, "end": v(-273.28, 274.3) * mm});
            skLineSegment(sketch, "E363", {"start": v(-273.28, 274.3) * mm, "end": v(-273.28, 280.37) * mm});
            skLineSegment(sketch, "E364", {"start": v(-273.28, 280.37) * mm, "end": v(-270.24, 280.37) * mm});
            skLineSegment(sketch, "E365", {"start": v(-270.24, 280.37) * mm, "end": v(-270.24, 286.44) * mm});
            skLineSegment(sketch, "E366", {"start": v(-270.24, 286.44) * mm, "end": v(-273.28, 286.44) * mm});
            skLineSegment(sketch, "E367", {"start": v(-273.28, 286.44) * mm, "end": v(-273.28, 292.51) * mm});
            skLineSegment(sketch, "E368", {"start": v(-273.28, 292.51) * mm, "end": v(-270.24, 292.51) * mm});
            skLineSegment(sketch, "E369", {"start": v(-270.24, 292.51) * mm, "end": v(-270.24, 298.58) * mm});
            skLineSegment(sketch, "E370", {"start": v(-270.24, 298.58) * mm, "end": v(-273.28, 298.58) * mm});
            skLineSegment(sketch, "E371", {"start": v(-273.28, 298.58) * mm, "end": v(-273.28, 304.66) * mm});
            skLineSegment(sketch, "E372", {"start": v(-273.28, 304.66) * mm, "end": v(-270.24, 304.66) * mm});
            skLineSegment(sketch, "E373", {"start": v(-270.24, 304.66) * mm, "end": v(-270.24, 310.73) * mm});
            skLineSegment(sketch, "E374", {"start": v(-270.24, 310.73) * mm, "end": v(-273.28, 310.73) * mm});
            skLineSegment(sketch, "E375", {"start": v(-273.28, 310.73) * mm, "end": v(-273.28, 316.8) * mm});
            skLineSegment(sketch, "E376", {"start": v(-273.28, 316.8) * mm, "end": v(-270.24, 316.8) * mm});
            skLineSegment(sketch, "E377", {"start": v(-270.24, 316.8) * mm, "end": v(-270.24, 322.87) * mm});
            skLineSegment(sketch, "E378", {"start": v(-270.24, 322.87) * mm, "end": v(-273.28, 322.87) * mm});
            skLineSegment(sketch, "E379", {"start": v(-273.28, 322.87) * mm, "end": v(-273.28, 328.95) * mm});
            skLineSegment(sketch, "E380", {"start": v(-273.28, 328.95) * mm, "end": v(-270.24, 328.95) * mm});
            skLineSegment(sketch, "E381", {"start": v(-270.24, 328.95) * mm, "end": v(-270.24, 335.02) * mm});
            skLineSegment(sketch, "E382", {"start": v(-270.24, 335.02) * mm, "end": v(-273.28, 335.02) * mm});
            skLineSegment(sketch, "E383", {"start": v(-273.28, 335.02) * mm, "end": v(-273.28, 341.1) * mm});
            skLineSegment(sketch, "E384", {"start": v(-273.28, 341.1) * mm, "end": v(-270.24, 341.1) * mm});
            skLineSegment(sketch, "E385", {"start": v(-270.24, 341.1) * mm, "end": v(-270.24, 347.16) * mm});
            skLineSegment(sketch, "E386", {"start": v(-270.24, 347.16) * mm, "end": v(-273.28, 347.16) * mm});
            skLineSegment(sketch, "E387", {"start": v(-273.28, 347.16) * mm, "end": v(-273.28, 353.24) * mm});
            skLineSegment(sketch, "E388", {"start": v(-273.28, 353.24) * mm, "end": v(-270.24, 353.24) * mm});
            skLineSegment(sketch, "E389", {"start": v(-270.24, 353.24) * mm, "end": v(-270.24, 359.31) * mm});
            skLineSegment(sketch, "E390", {"start": v(-270.24, 359.31) * mm, "end": v(-273.28, 359.31) * mm});
            skLineSegment(sketch, "E391", {"start": v(-273.28, 359.31) * mm, "end": v(-273.28, 365.39) * mm});
            skLineSegment(sketch, "E392", {"start": v(-273.28, 365.39) * mm, "end": v(-270.24, 365.39) * mm});
            skLineSegment(sketch, "E393", {"start": v(-270.24, 365.39) * mm, "end": v(-270.24, 371.46) * mm});
            skLineSegment(sketch, "E394", {"start": v(-270.24, 371.46) * mm, "end": v(-273.28, 371.46) * mm});
            skLineSegment(sketch, "E395", {"start": v(-273.28, 371.46) * mm, "end": v(-273.28, 377.53) * mm});
            skLineSegment(sketch, "E396", {"start": v(-273.28, 377.53) * mm, "end": v(-270.24, 377.53) * mm});
            skLineSegment(sketch, "E397", {"start": v(-270.24, 377.53) * mm, "end": v(-270.24, 383.6) * mm});
            skLineSegment(sketch, "E398", {"start": v(-270.24, 383.6) * mm, "end": v(-273.28, 383.6) * mm});
            skLineSegment(sketch, "E399", {"start": v(-273.28, 383.6) * mm, "end": v(-273.28, 389.68) * mm});
            skLineSegment(sketch, "E400", {"start": v(-273.28, 389.68) * mm, "end": v(-270.24, 389.68) * mm});
            skLineSegment(sketch, "E401", {"start": v(-270.24, 389.68) * mm, "end": v(-270.24, 395.75) * mm});
            skLineSegment(sketch, "E402", {"start": v(-270.24, 395.75) * mm, "end": v(-273.28, 395.75) * mm});
            skLineSegment(sketch, "E403", {"start": v(-273.28, 395.75) * mm, "end": v(-273.28, 401.82) * mm});
            skLineSegment(sketch, "E404", {"start": v(-273.28, 401.82) * mm, "end": v(-270.24, 401.82) * mm});
            skLineSegment(sketch, "E405", {"start": v(-270.24, 401.82) * mm, "end": v(-270.24, 407.9) * mm});
            skLineSegment(sketch, "E406", {"start": v(-270.24, 407.9) * mm, "end": v(-273.28, 407.9) * mm});
            skLineSegment(sketch, "E407", {"start": v(-273.28, 407.9) * mm, "end": v(-273.28, 413.97) * mm});
            skLineSegment(sketch, "E408", {"start": v(-273.28, 413.97) * mm, "end": v(-270.24, 413.97) * mm});
            skLineSegment(sketch, "E409", {"start": v(-270.24, 413.97) * mm, "end": v(-270.24, 420.04) * mm});
            skLineSegment(sketch, "E410", {"start": v(-270.24, 420.04) * mm, "end": v(-273.28, 420.04) * mm});
            skLineSegment(sketch, "E411", {"start": v(-273.28, 420.04) * mm, "end": v(-273.28, 426.11) * mm});
            skLineSegment(sketch, "E412", {"start": v(-273.28, 426.11) * mm, "end": v(-270.24, 426.11) * mm});
            skLineSegment(sketch, "E413", {"start": v(-270.24, 426.11) * mm, "end": v(-270.24, 432.18) * mm});
            skLineSegment(sketch, "E414", {"start": v(-270.24, 432.18) * mm, "end": v(-273.28, 432.18) * mm});
            skLineSegment(sketch, "E415", {"start": v(-273.28, 432.18) * mm, "end": v(-273.28, 438.26) * mm});
            skLineSegment(sketch, "E416", {"start": v(-273.28, 438.26) * mm, "end": v(-270.24, 438.26) * mm});
            skLineSegment(sketch, "E417", {"start": v(-270.24, 438.26) * mm, "end": v(-270.24, 444.33) * mm});
            skLineSegment(sketch, "E418", {"start": v(-270.24, 444.33) * mm, "end": v(-273.28, 444.33) * mm});
            skLineSegment(sketch, "E419", {"start": v(-273.28, 444.33) * mm, "end": v(-273.28, 450.4) * mm});
            skLineSegment(sketch, "E420", {"start": v(-273.28, 450.4) * mm, "end": v(-270.24, 450.4) * mm});
            skLineSegment(sketch, "E421", {"start": v(-270.24, 450.4) * mm, "end": v(-270.24, 456.48) * mm});
            skLineSegment(sketch, "E422", {"start": v(-270.24, 456.48) * mm, "end": v(-273.28, 456.48) * mm});
            skLineSegment(sketch, "E423", {"start": v(-273.28, 456.48) * mm, "end": v(-273.28, 462.55) * mm});
            skLineSegment(sketch, "E424", {"start": v(-273.28, 462.55) * mm, "end": v(-270.24, 462.55) * mm});
            skLineSegment(sketch, "E425", {"start": v(-270.24, 462.55) * mm, "end": v(-270.24, 468.62) * mm});
            skLineSegment(sketch, "E426", {"start": v(-270.24, 468.62) * mm, "end": v(-273.28, 468.62) * mm});
            skLineSegment(sketch, "E427", {"start": v(-273.28, 468.62) * mm, "end": v(-273.28, 474.7) * mm});
            skLineSegment(sketch, "E428", {"start": v(-273.28, 474.7) * mm, "end": v(-270.24, 474.7) * mm});
            skLineSegment(sketch, "E429", {"start": v(-270.24, 474.7) * mm, "end": v(-270.24, 480.77) * mm});
            skLineSegment(sketch, "E430", {"start": v(-270.24, 480.77) * mm, "end": v(-273.28, 480.77) * mm});
            skLineSegment(sketch, "E431", {"start": v(-273.28, 480.77) * mm, "end": v(-273.28, 486.84) * mm});
            skLineSegment(sketch, "E432", {"start": v(-273.28, 486.84) * mm, "end": v(-270.24, 486.84) * mm});
            skLineSegment(sketch, "E433", {"start": v(-270.24, 486.84) * mm, "end": v(-270.24, 496.46) * mm});
            skLineSegment(sketch, "E434", {"start": v(-270.24, 496.46) * mm, "end": v(-273.28, 496.46) * mm});
            skLineSegment(sketch, "E435", {"start": v(-273.28, 496.46) * mm, "end": v(-273.28, 506.07) * mm});
            skLineSegment(sketch, "E436", {"start": v(-91.1, 506.07) * mm, "end": v(-83.5, 506.07) * mm});
            skLineSegment(sketch, "E437", {"start": v(-83.5, 506.07) * mm, "end": v(-83.5, 503.04) * mm});
            skLineSegment(sketch, "E438", {"start": v(-83.5, 503.04) * mm, "end": v(-75.91, 503.04) * mm});
            skLineSegment(sketch, "E439", {"start": v(-75.91, 503.04) * mm, "end": v(-75.91, 506.07) * mm});
            skLineSegment(sketch, "E440", {"start": v(-75.91, 506.07) * mm, "end": v(-69.84, 506.07) * mm});
            skLineSegment(sketch, "E441", {"start": v(-69.84, 506.07) * mm, "end": v(-69.84, 503.04) * mm});
            skLineSegment(sketch, "E442", {"start": v(-69.84, 503.04) * mm, "end": v(-63.77, 503.04) * mm});
            skLineSegment(sketch, "E443", {"start": v(-63.77, 503.04) * mm, "end": v(-63.77, 506.07) * mm});
            skLineSegment(sketch, "E444", {"start": v(-63.77, 506.07) * mm, "end": v(-57.7, 506.07) * mm});
            skLineSegment(sketch, "E445", {"start": v(-57.7, 506.07) * mm, "end": v(-57.7, 503.04) * mm});
            skLineSegment(sketch, "E446", {"start": v(-57.7, 503.04) * mm, "end": v(-51.62, 503.04) * mm});
            skLineSegment(sketch, "E447", {"start": v(-51.62, 503.04) * mm, "end": v(-51.62, 506.07) * mm});
            skLineSegment(sketch, "E448", {"start": v(-51.62, 506.07) * mm, "end": v(-45.55, 506.07) * mm});
            skLineSegment(sketch, "E449", {"start": v(-45.55, 506.07) * mm, "end": v(-45.55, 503.04) * mm});
            skLineSegment(sketch, "E450", {"start": v(-45.55, 503.04) * mm, "end": v(-39.47, 503.04) * mm});
            skLineSegment(sketch, "E451", {"start": v(-39.47, 503.04) * mm, "end": v(-39.47, 506.07) * mm});
            skLineSegment(sketch, "E452", {"start": v(-39.47, 506.07) * mm, "end": v(-33.4, 506.07) * mm});
            skLineSegment(sketch, "E453", {"start": v(-33.4, 506.07) * mm, "end": v(-33.4, 503.04) * mm});
            skLineSegment(sketch, "E454", {"start": v(-33.4, 503.04) * mm, "end": v(-27.33, 503.04) * mm});
            skLineSegment(sketch, "E455", {"start": v(-27.33, 503.04) * mm, "end": v(-27.33, 506.07) * mm});
            skLineSegment(sketch, "E456", {"start": v(-27.33, 506.07) * mm, "end": v(-21.25, 506.07) * mm});
            skLineSegment(sketch, "E457", {"start": v(-21.25, 506.07) * mm, "end": v(-21.25, 503.04) * mm});
            skLineSegment(sketch, "E458", {"start": v(-21.25, 503.04) * mm, "end": v(-15.18, 503.04) * mm});
            skLineSegment(sketch, "E459", {"start": v(-15.18, 503.04) * mm, "end": v(-15.18, 506.07) * mm});
            skLineSegment(sketch, "E460", {"start": v(-15.18, 506.07) * mm, "end": v(-9.1, 506.07) * mm});
            skLineSegment(sketch, "E461", {"start": v(-9.1, 506.07) * mm, "end": v(-9.1, 503.04) * mm});
            skLineSegment(sketch, "E462", {"start": v(-9.1, 503.04) * mm, "end": v(-3.04, 503.04) * mm});
            skLineSegment(sketch, "E463", {"start": v(-3.04, 503.04) * mm, "end": v(-3.04, 506.07) * mm});
            skLineSegment(sketch, "E464", {"start": v(-3.04, 506.07) * mm, "end": v(3.04, 506.07) * mm});
            skLineSegment(sketch, "E465", {"start": v(3.04, 506.07) * mm, "end": v(3.04, 503.04) * mm});
            skLineSegment(sketch, "E466", {"start": v(3.04, 503.04) * mm, "end": v(9.1, 503.04) * mm});
            skLineSegment(sketch, "E467", {"start": v(9.1, 503.04) * mm, "end": v(9.1, 506.07) * mm});
            skLineSegment(sketch, "E468", {"start": v(9.1, 506.07) * mm, "end": v(15.18, 506.07) * mm});
            skLineSegment(sketch, "E469", {"start": v(15.18, 506.07) * mm, "end": v(15.18, 503.04) * mm});
            skLineSegment(sketch, "E470", {"start": v(15.18, 503.04) * mm, "end": v(21.25, 503.04) * mm});
            skLineSegment(sketch, "E471", {"start": v(21.25, 503.04) * mm, "end": v(21.25, 506.07) * mm});
            skLineSegment(sketch, "E472", {"start": v(21.25, 506.07) * mm, "end": v(27.33, 506.07) * mm});
            skLineSegment(sketch, "E473", {"start": v(27.33, 506.07) * mm, "end": v(27.33, 503.04) * mm});
            skLineSegment(sketch, "E474", {"start": v(27.33, 503.04) * mm, "end": v(33.4, 503.04) * mm});
            skLineSegment(sketch, "E475", {"start": v(33.4, 503.04) * mm, "end": v(33.4, 506.07) * mm});
            skLineSegment(sketch, "E476", {"start": v(33.4, 506.07) * mm, "end": v(39.47, 506.07) * mm});
            skLineSegment(sketch, "E477", {"start": v(39.47, 506.07) * mm, "end": v(39.47, 503.04) * mm});
            skLineSegment(sketch, "E478", {"start": v(39.47, 503.04) * mm, "end": v(45.54, 503.04) * mm});
            skLineSegment(sketch, "E479", {"start": v(45.54, 503.04) * mm, "end": v(45.54, 506.07) * mm});
            skLineSegment(sketch, "E480", {"start": v(45.54, 506.07) * mm, "end": v(51.62, 506.07) * mm});
            skLineSegment(sketch, "E481", {"start": v(51.62, 506.07) * mm, "end": v(51.62, 503.04) * mm});
            skLineSegment(sketch, "E482", {"start": v(51.62, 503.04) * mm, "end": v(57.7, 503.04) * mm});
            skLineSegment(sketch, "E483", {"start": v(57.7, 503.04) * mm, "end": v(57.7, 506.07) * mm});
            skLineSegment(sketch, "E484", {"start": v(57.7, 506.07) * mm, "end": v(63.77, 506.07) * mm});
            skLineSegment(sketch, "E485", {"start": v(63.77, 506.07) * mm, "end": v(63.77, 503.04) * mm});
            skLineSegment(sketch, "E486", {"start": v(63.77, 503.04) * mm, "end": v(69.84, 503.04) * mm});
            skLineSegment(sketch, "E487", {"start": v(69.84, 503.04) * mm, "end": v(69.84, 506.07) * mm});
            skLineSegment(sketch, "E488", {"start": v(69.84, 506.07) * mm, "end": v(75.91, 506.07) * mm});
            skLineSegment(sketch, "E489", {"start": v(75.91, 506.07) * mm, "end": v(75.91, 503.04) * mm});
            skLineSegment(sketch, "E490", {"start": v(75.91, 503.04) * mm, "end": v(83.5, 503.04) * mm});
            skLineSegment(sketch, "E491", {"start": v(83.5, 503.04) * mm, "end": v(83.5, 506.07) * mm});
            skLineSegment(sketch, "E492", {"start": v(83.5, 506.07) * mm, "end": v(91.1, 506.07) * mm});
            skLineSegment(sketch, "E493", {"start": v(91.1, 506.07) * mm, "end": v(91.1, 496.46) * mm});
            skLineSegment(sketch, "E494", {"start": v(91.1, 496.46) * mm, "end": v(88.06, 496.46) * mm});
            skLineSegment(sketch, "E495", {"start": v(88.06, 496.46) * mm, "end": v(88.06, 486.84) * mm});
            skLineSegment(sketch, "E496", {"start": v(88.06, 486.84) * mm, "end": v(91.1, 486.84) * mm});
            skLineSegment(sketch, "E497", {"start": v(91.1, 486.84) * mm, "end": v(91.1, 480.77) * mm});
            skLineSegment(sketch, "E498", {"start": v(91.1, 480.77) * mm, "end": v(88.06, 480.77) * mm});
            skLineSegment(sketch, "E499", {"start": v(88.06, 480.77) * mm, "end": v(88.06, 474.7) * mm});
            skLineSegment(sketch, "E500", {"start": v(88.06, 474.7) * mm, "end": v(91.1, 474.7) * mm});
            skLineSegment(sketch, "E501", {"start": v(91.1, 474.7) * mm, "end": v(91.1, 468.62) * mm});
            skLineSegment(sketch, "E502", {"start": v(91.1, 468.62) * mm, "end": v(88.06, 468.62) * mm});
            skLineSegment(sketch, "E503", {"start": v(88.06, 468.62) * mm, "end": v(88.06, 462.55) * mm});
            skLineSegment(sketch, "E504", {"start": v(88.06, 462.55) * mm, "end": v(91.1, 462.55) * mm});
            skLineSegment(sketch, "E505", {"start": v(91.1, 462.55) * mm, "end": v(91.1, 456.48) * mm});
            skLineSegment(sketch, "E506", {"start": v(91.1, 456.48) * mm, "end": v(88.06, 456.48) * mm});
            skLineSegment(sketch, "E507", {"start": v(88.06, 456.48) * mm, "end": v(88.06, 450.4) * mm});
            skLineSegment(sketch, "E508", {"start": v(88.06, 450.4) * mm, "end": v(91.1, 450.4) * mm});
            skLineSegment(sketch, "E509", {"start": v(91.1, 450.4) * mm, "end": v(91.1, 444.33) * mm});
            skLineSegment(sketch, "E510", {"start": v(91.1, 444.33) * mm, "end": v(88.06, 444.33) * mm});
            skLineSegment(sketch, "E511", {"start": v(88.06, 444.33) * mm, "end": v(88.06, 438.26) * mm});
            skLineSegment(sketch, "E512", {"start": v(88.06, 438.26) * mm, "end": v(91.1, 438.26) * mm});
            skLineSegment(sketch, "E513", {"start": v(91.1, 438.26) * mm, "end": v(91.1, 432.18) * mm});
            skLineSegment(sketch, "E514", {"start": v(91.1, 432.18) * mm, "end": v(88.06, 432.18) * mm});
            skLineSegment(sketch, "E515", {"start": v(88.06, 432.18) * mm, "end": v(88.06, 426.11) * mm});
            skLineSegment(sketch, "E516", {"start": v(88.06, 426.11) * mm, "end": v(91.1, 426.11) * mm});
            skLineSegment(sketch, "E517", {"start": v(91.1, 426.11) * mm, "end": v(91.1, 420.04) * mm});
            skLineSegment(sketch, "E518", {"start": v(91.1, 420.04) * mm, "end": v(88.06, 420.04) * mm});
            skLineSegment(sketch, "E519", {"start": v(88.06, 420.04) * mm, "end": v(88.06, 413.97) * mm});
            skLineSegment(sketch, "E520", {"start": v(88.06, 413.97) * mm, "end": v(91.1, 413.97) * mm});
            skLineSegment(sketch, "E521", {"start": v(91.1, 413.97) * mm, "end": v(91.1, 407.9) * mm});
            skLineSegment(sketch, "E522", {"start": v(91.1, 407.9) * mm, "end": v(88.06, 407.9) * mm});
            skLineSegment(sketch, "E523", {"start": v(88.06, 407.9) * mm, "end": v(88.06, 401.82) * mm});
            skLineSegment(sketch, "E524", {"start": v(88.06, 401.82) * mm, "end": v(91.1, 401.82) * mm});
            skLineSegment(sketch, "E525", {"start": v(91.1, 401.82) * mm, "end": v(91.1, 395.75) * mm});
            skLineSegment(sketch, "E526", {"start": v(91.1, 395.75) * mm, "end": v(88.06, 395.75) * mm});
            skLineSegment(sketch, "E527", {"start": v(88.06, 395.75) * mm, "end": v(88.06, 389.68) * mm});
            skLineSegment(sketch, "E528", {"start": v(88.06, 389.68) * mm, "end": v(91.1, 389.68) * mm});
            skLineSegment(sketch, "E529", {"start": v(91.1, 389.68) * mm, "end": v(91.1, 383.6) * mm});
            skLineSegment(sketch, "E530", {"start": v(91.1, 383.6) * mm, "end": v(88.06, 383.6) * mm});
            skLineSegment(sketch, "E531", {"start": v(88.06, 383.6) * mm, "end": v(88.06, 377.53) * mm});
            skLineSegment(sketch, "E532", {"start": v(88.06, 377.53) * mm, "end": v(91.1, 377.53) * mm});
            skLineSegment(sketch, "E533", {"start": v(91.1, 377.53) * mm, "end": v(91.1, 371.46) * mm});
            skLineSegment(sketch, "E534", {"start": v(91.1, 371.46) * mm, "end": v(88.06, 371.46) * mm});
            skLineSegment(sketch, "E535", {"start": v(88.06, 371.46) * mm, "end": v(88.06, 365.39) * mm});
            skLineSegment(sketch, "E536", {"start": v(88.06, 365.39) * mm, "end": v(91.1, 365.39) * mm});
            skLineSegment(sketch, "E537", {"start": v(91.1, 365.39) * mm, "end": v(91.1, 359.31) * mm});
            skLineSegment(sketch, "E538", {"start": v(91.1, 359.31) * mm, "end": v(88.06, 359.31) * mm});
            skLineSegment(sketch, "E539", {"start": v(88.06, 359.31) * mm, "end": v(88.06, 353.24) * mm});
            skLineSegment(sketch, "E540", {"start": v(88.06, 353.24) * mm, "end": v(91.1, 353.24) * mm});
            skLineSegment(sketch, "E541", {"start": v(91.1, 353.24) * mm, "end": v(91.1, 347.16) * mm});
            skLineSegment(sketch, "E542", {"start": v(91.1, 347.16) * mm, "end": v(88.06, 347.16) * mm});
            skLineSegment(sketch, "E543", {"start": v(88.06, 347.16) * mm, "end": v(88.06, 341.1) * mm});
            skLineSegment(sketch, "E544", {"start": v(88.06, 341.1) * mm, "end": v(91.1, 341.1) * mm});
            skLineSegment(sketch, "E545", {"start": v(91.1, 341.1) * mm, "end": v(91.1, 335.02) * mm});
            skLineSegment(sketch, "E546", {"start": v(91.1, 335.02) * mm, "end": v(88.06, 335.02) * mm});
            skLineSegment(sketch, "E547", {"start": v(88.06, 335.02) * mm, "end": v(88.06, 328.95) * mm});
            skLineSegment(sketch, "E548", {"start": v(88.06, 328.95) * mm, "end": v(91.1, 328.95) * mm});
            skLineSegment(sketch, "E549", {"start": v(91.1, 328.95) * mm, "end": v(91.1, 322.87) * mm});
            skLineSegment(sketch, "E550", {"start": v(91.1, 322.87) * mm, "end": v(88.06, 322.87) * mm});
            skLineSegment(sketch, "E551", {"start": v(88.06, 322.87) * mm, "end": v(88.06, 316.8) * mm});
            skLineSegment(sketch, "E552", {"start": v(88.06, 316.8) * mm, "end": v(91.1, 316.8) * mm});
            skLineSegment(sketch, "E553", {"start": v(91.1, 316.8) * mm, "end": v(91.1, 310.73) * mm});
            skLineSegment(sketch, "E554", {"start": v(91.1, 310.73) * mm, "end": v(88.06, 310.73) * mm});
            skLineSegment(sketch, "E555", {"start": v(88.06, 310.73) * mm, "end": v(88.06, 304.66) * mm});
            skLineSegment(sketch, "E556", {"start": v(88.06, 304.66) * mm, "end": v(91.1, 304.66) * mm});
            skLineSegment(sketch, "E557", {"start": v(91.1, 304.66) * mm, "end": v(91.1, 298.58) * mm});
            skLineSegment(sketch, "E558", {"start": v(91.1, 298.58) * mm, "end": v(88.06, 298.58) * mm});
            skLineSegment(sketch, "E559", {"start": v(88.06, 298.58) * mm, "end": v(88.06, 292.51) * mm});
            skLineSegment(sketch, "E560", {"start": v(88.06, 292.51) * mm, "end": v(91.1, 292.51) * mm});
            skLineSegment(sketch, "E561", {"start": v(91.1, 292.51) * mm, "end": v(91.1, 286.44) * mm});
            skLineSegment(sketch, "E562", {"start": v(91.1, 286.44) * mm, "end": v(88.06, 286.44) * mm});
            skLineSegment(sketch, "E563", {"start": v(88.06, 286.44) * mm, "end": v(88.06, 280.37) * mm});
            skLineSegment(sketch, "E564", {"start": v(88.06, 280.37) * mm, "end": v(91.1, 280.37) * mm});
            skLineSegment(sketch, "E565", {"start": v(91.1, 280.37) * mm, "end": v(91.1, 274.3) * mm});
            skLineSegment(sketch, "E566", {"start": v(91.1, 274.3) * mm, "end": v(88.06, 274.3) * mm});
            skLineSegment(sketch, "E567", {"start": v(88.06, 274.3) * mm, "end": v(88.06, 268.22) * mm});
            skLineSegment(sketch, "E568", {"start": v(88.06, 268.22) * mm, "end": v(91.1, 268.22) * mm});
            skLineSegment(sketch, "E569", {"start": v(91.1, 268.22) * mm, "end": v(91.1, 262.15) * mm});
            skLineSegment(sketch, "E570", {"start": v(91.1, 262.15) * mm, "end": v(88.06, 262.15) * mm});
            skLineSegment(sketch, "E571", {"start": v(88.06, 262.15) * mm, "end": v(88.06, 256.07) * mm});
            skLineSegment(sketch, "E572", {"start": v(88.06, 256.07) * mm, "end": v(91.1, 256.07) * mm});
            skLineSegment(sketch, "E573", {"start": v(91.1, 256.07) * mm, "end": v(91.1, 250) * mm});
            skLineSegment(sketch, "E574", {"start": v(91.1, 250) * mm, "end": v(88.06, 250) * mm});
            skLineSegment(sketch, "E575", {"start": v(88.06, 250) * mm, "end": v(88.06, 243.93) * mm});
            skLineSegment(sketch, "E576", {"start": v(88.06, 243.93) * mm, "end": v(91.1, 243.93) * mm});
            skLineSegment(sketch, "E577", {"start": v(91.1, 243.93) * mm, "end": v(91.1, 237.85) * mm});
            skLineSegment(sketch, "E578", {"start": v(91.1, 237.85) * mm, "end": v(88.06, 237.85) * mm});
            skLineSegment(sketch, "E579", {"start": v(88.06, 237.85) * mm, "end": v(88.06, 231.78) * mm});
            skLineSegment(sketch, "E580", {"start": v(88.06, 231.78) * mm, "end": v(91.1, 231.78) * mm});
            skLineSegment(sketch, "E581", {"start": v(91.1, 231.78) * mm, "end": v(91.1, 225.7) * mm});
            skLineSegment(sketch, "E582", {"start": v(91.1, 225.7) * mm, "end": v(88.06, 225.7) * mm});
            skLineSegment(sketch, "E583", {"start": v(88.06, 225.7) * mm, "end": v(88.06, 219.64) * mm});
            skLineSegment(sketch, "E584", {"start": v(88.06, 219.64) * mm, "end": v(91.1, 219.64) * mm});
            skLineSegment(sketch, "E585", {"start": v(91.1, 219.64) * mm, "end": v(91.1, 213.56) * mm});
            skLineSegment(sketch, "E586", {"start": v(91.1, 213.56) * mm, "end": v(88.06, 213.56) * mm});
            skLineSegment(sketch, "E587", {"start": v(88.06, 213.56) * mm, "end": v(88.06, 207.49) * mm});
            skLineSegment(sketch, "E588", {"start": v(88.06, 207.49) * mm, "end": v(91.1, 207.49) * mm});
            skLineSegment(sketch, "E589", {"start": v(91.1, 207.49) * mm, "end": v(91.1, 201.42) * mm});
            skLineSegment(sketch, "E590", {"start": v(91.1, 201.42) * mm, "end": v(88.06, 201.42) * mm});
            skLineSegment(sketch, "E591", {"start": v(88.06, 201.42) * mm, "end": v(88.06, 195.34) * mm});
            skLineSegment(sketch, "E592", {"start": v(88.06, 195.34) * mm, "end": v(91.1, 195.34) * mm});
            skLineSegment(sketch, "E593", {"start": v(91.1, 195.34) * mm, "end": v(91.1, 189.27) * mm});
            skLineSegment(sketch, "E594", {"start": v(91.1, 189.27) * mm, "end": v(88.06, 189.27) * mm});
            skLineSegment(sketch, "E595", {"start": v(88.06, 189.27) * mm, "end": v(88.06, 183.2) * mm});
            skLineSegment(sketch, "E596", {"start": v(88.06, 183.2) * mm, "end": v(91.1, 183.2) * mm});
            skLineSegment(sketch, "E597", {"start": v(91.1, 183.2) * mm, "end": v(91.1, 177.13) * mm});
            skLineSegment(sketch, "E598", {"start": v(91.1, 177.13) * mm, "end": v(88.06, 177.13) * mm});
            skLineSegment(sketch, "E599", {"start": v(88.06, 177.13) * mm, "end": v(88.06, 171.06) * mm});
            skLineSegment(sketch, "E600", {"start": v(88.06, 171.06) * mm, "end": v(91.1, 171.06) * mm});
            skLineSegment(sketch, "E601", {"start": v(91.1, 171.06) * mm, "end": v(91.1, 164.98) * mm});
            skLineSegment(sketch, "E602", {"start": v(91.1, 164.98) * mm, "end": v(88.06, 164.98) * mm});
            skLineSegment(sketch, "E603", {"start": v(88.06, 164.98) * mm, "end": v(88.06, 158.9) * mm});
            skLineSegment(sketch, "E604", {"start": v(88.06, 158.9) * mm, "end": v(91.1, 158.9) * mm});
            skLineSegment(sketch, "E605", {"start": v(91.1, 158.9) * mm, "end": v(91.1, 152.83) * mm});
            skLineSegment(sketch, "E606", {"start": v(91.1, 152.83) * mm, "end": v(88.06, 152.83) * mm});
            skLineSegment(sketch, "E607", {"start": v(88.06, 152.83) * mm, "end": v(88.06, 146.76) * mm});
            skLineSegment(sketch, "E608", {"start": v(88.06, 146.76) * mm, "end": v(91.1, 146.76) * mm});
            skLineSegment(sketch, "E609", {"start": v(91.1, 146.76) * mm, "end": v(91.1, 140.69) * mm});
            skLineSegment(sketch, "E610", {"start": v(91.1, 140.69) * mm, "end": v(88.06, 140.69) * mm});
            skLineSegment(sketch, "E611", {"start": v(88.06, 140.69) * mm, "end": v(88.06, 134.62) * mm});
            skLineSegment(sketch, "E612", {"start": v(88.06, 134.62) * mm, "end": v(91.1, 134.62) * mm});
            skLineSegment(sketch, "E613", {"start": v(91.1, 134.62) * mm, "end": v(91.1, 128.54) * mm});
            skLineSegment(sketch, "E614", {"start": v(91.1, 128.54) * mm, "end": v(88.06, 128.54) * mm});
            skLineSegment(sketch, "E615", {"start": v(88.06, 128.54) * mm, "end": v(88.06, 122.47) * mm});
            skLineSegment(sketch, "E616", {"start": v(88.06, 122.47) * mm, "end": v(91.1, 122.47) * mm});
            skLineSegment(sketch, "E617", {"start": v(91.1, 122.47) * mm, "end": v(91.1, 116.4) * mm});
            skLineSegment(sketch, "E618", {"start": v(91.1, 116.4) * mm, "end": v(88.06, 116.4) * mm});
            skLineSegment(sketch, "E619", {"start": v(88.06, 116.4) * mm, "end": v(88.06, 110.32) * mm});
            skLineSegment(sketch, "E620", {"start": v(88.06, 110.32) * mm, "end": v(91.1, 110.32) * mm});
            skLineSegment(sketch, "E621", {"start": v(91.1, 110.32) * mm, "end": v(91.1, 104.25) * mm});
            skLineSegment(sketch, "E622", {"start": v(91.1, 104.25) * mm, "end": v(88.06, 104.25) * mm});
            skLineSegment(sketch, "E623", {"start": v(88.06, 104.25) * mm, "end": v(88.06, 98.18) * mm});
            skLineSegment(sketch, "E624", {"start": v(88.06, 98.18) * mm, "end": v(91.1, 98.18) * mm});
            skLineSegment(sketch, "E625", {"start": v(91.1, 98.18) * mm, "end": v(91.1, 92.1) * mm});
            skLineSegment(sketch, "E626", {"start": v(91.1, 92.1) * mm, "end": v(88.06, 92.1) * mm});
            skLineSegment(sketch, "E627", {"start": v(88.06, 92.1) * mm, "end": v(88.06, 86.03) * mm});
            skLineSegment(sketch, "E628", {"start": v(88.06, 86.03) * mm, "end": v(91.1, 86.03) * mm});
            skLineSegment(sketch, "E629", {"start": v(91.1, 86.03) * mm, "end": v(91.1, 79.96) * mm});
            skLineSegment(sketch, "E630", {"start": v(91.1, 79.96) * mm, "end": v(88.06, 79.96) * mm});
            skLineSegment(sketch, "E631", {"start": v(88.06, 79.96) * mm, "end": v(88.06, 73.89) * mm});
            skLineSegment(sketch, "E632", {"start": v(88.06, 73.89) * mm, "end": v(91.1, 73.89) * mm});
            skLineSegment(sketch, "E633", {"start": v(91.1, 73.89) * mm, "end": v(91.1, 67.81) * mm});
            skLineSegment(sketch, "E634", {"start": v(91.1, 67.81) * mm, "end": v(88.06, 67.81) * mm});
            skLineSegment(sketch, "E635", {"start": v(88.06, 67.81) * mm, "end": v(88.06, 61.74) * mm});
            skLineSegment(sketch, "E636", {"start": v(88.06, 61.74) * mm, "end": v(91.1, 61.74) * mm});
            skLineSegment(sketch, "E637", {"start": v(91.1, 61.74) * mm, "end": v(91.1, 55.67) * mm});
            skLineSegment(sketch, "E638", {"start": v(91.1, 55.67) * mm, "end": v(88.06, 55.67) * mm});
            skLineSegment(sketch, "E639", {"start": v(88.06, 55.67) * mm, "end": v(88.06, 49.6) * mm});
            skLineSegment(sketch, "E640", {"start": v(88.06, 49.6) * mm, "end": v(91.1, 49.6) * mm});
            skLineSegment(sketch, "E641", {"start": v(91.1, 49.6) * mm, "end": v(91.1, 43.52) * mm});
            skLineSegment(sketch, "E642", {"start": v(91.1, 43.52) * mm, "end": v(88.06, 43.52) * mm});
            skLineSegment(sketch, "E643", {"start": v(88.06, 43.52) * mm, "end": v(88.06, 37.45) * mm});
            skLineSegment(sketch, "E644", {"start": v(88.06, 37.45) * mm, "end": v(91.1, 37.45) * mm});
            skLineSegment(sketch, "E645", {"start": v(91.1, 37.45) * mm, "end": v(91.1, 31.38) * mm});
            skLineSegment(sketch, "E646", {"start": v(91.1, 31.38) * mm, "end": v(88.06, 31.38) * mm});
            skLineSegment(sketch, "E647", {"start": v(88.06, 31.38) * mm, "end": v(88.06, 25.3) * mm});
            skLineSegment(sketch, "E648", {"start": v(88.06, 25.3) * mm, "end": v(91.1, 25.3) * mm});
            skLineSegment(sketch, "E649", {"start": v(91.1, 25.3) * mm, "end": v(91.1, 19.23) * mm});
            skLineSegment(sketch, "E650", {"start": v(91.1, 19.23) * mm, "end": v(88.06, 19.23) * mm});
            skLineSegment(sketch, "E651", {"start": v(88.06, 19.23) * mm, "end": v(88.06, 9.62) * mm});
            skLineSegment(sketch, "E652", {"start": v(88.06, 9.62) * mm, "end": v(91.1, 9.62) * mm});
            skLineSegment(sketch, "E653", {"start": v(91.1, 9.62) * mm, "end": v(91.1, 0) * mm});
            skLineSegment(sketch, "E654", {"start": v(91.1, 0) * mm, "end": v(83.5, 0) * mm});
            skLineSegment(sketch, "E655", {"start": v(83.5, 0) * mm, "end": v(83.5, 3.04) * mm});
            skLineSegment(sketch, "E656", {"start": v(83.5, 3.04) * mm, "end": v(75.91, 3.04) * mm});
            skLineSegment(sketch, "E657", {"start": v(75.91, 3.04) * mm, "end": v(75.91, 0) * mm});
            skLineSegment(sketch, "E658", {"start": v(75.91, 0) * mm, "end": v(69.84, 0) * mm});
            skLineSegment(sketch, "E659", {"start": v(69.84, 0) * mm, "end": v(69.84, 3.04) * mm});
            skLineSegment(sketch, "E660", {"start": v(69.84, 3.04) * mm, "end": v(63.77, 3.04) * mm});
            skLineSegment(sketch, "E661", {"start": v(63.77, 3.04) * mm, "end": v(63.77, 0) * mm});
            skLineSegment(sketch, "E662", {"start": v(63.77, 0) * mm, "end": v(57.7, 0) * mm});
            skLineSegment(sketch, "E663", {"start": v(57.7, 0) * mm, "end": v(57.7, 3.04) * mm});
            skLineSegment(sketch, "E664", {"start": v(57.7, 3.04) * mm, "end": v(51.62, 3.04) * mm});
            skLineSegment(sketch, "E665", {"start": v(51.62, 3.04) * mm, "end": v(51.62, 0) * mm});
            skLineSegment(sketch, "E666", {"start": v(51.62, 0) * mm, "end": v(45.54, 0) * mm});
            skLineSegment(sketch, "E667", {"start": v(45.54, 0) * mm, "end": v(45.54, 3.04) * mm});
            skLineSegment(sketch, "E668", {"start": v(45.54, 3.04) * mm, "end": v(39.47, 3.04) * mm});
            skLineSegment(sketch, "E669", {"start": v(39.47, 3.04) * mm, "end": v(39.47, 0) * mm});
            skLineSegment(sketch, "E670", {"start": v(39.47, 0) * mm, "end": v(33.4, 0) * mm});
            skLineSegment(sketch, "E671", {"start": v(33.4, 0) * mm, "end": v(33.4, 3.04) * mm});
            skLineSegment(sketch, "E672", {"start": v(33.4, 3.04) * mm, "end": v(27.33, 3.04) * mm});
            skLineSegment(sketch, "E673", {"start": v(27.33, 3.04) * mm, "end": v(27.33, 0) * mm});
            skLineSegment(sketch, "E674", {"start": v(27.33, 0) * mm, "end": v(21.25, 0) * mm});
            skLineSegment(sketch, "E675", {"start": v(21.25, 0) * mm, "end": v(21.25, 3.04) * mm});
            skLineSegment(sketch, "E676", {"start": v(21.25, 3.04) * mm, "end": v(15.18, 3.04) * mm});
            skLineSegment(sketch, "E677", {"start": v(15.18, 3.04) * mm, "end": v(15.18, 0) * mm});
            skLineSegment(sketch, "E678", {"start": v(15.18, 0) * mm, "end": v(9.1, 0) * mm});
            skLineSegment(sketch, "E679", {"start": v(9.1, 0) * mm, "end": v(9.1, 3.04) * mm});
            skLineSegment(sketch, "E680", {"start": v(9.1, 3.04) * mm, "end": v(3.04, 3.04) * mm});
            skLineSegment(sketch, "E681", {"start": v(3.04, 3.04) * mm, "end": v(3.04, 0) * mm});
            skLineSegment(sketch, "E682", {"start": v(3.04, 0) * mm, "end": v(-3.04, 0) * mm});
            skLineSegment(sketch, "E683", {"start": v(-3.04, 0) * mm, "end": v(-3.04, 3.04) * mm});
            skLineSegment(sketch, "E684", {"start": v(-3.04, 3.04) * mm, "end": v(-9.1, 3.04) * mm});
            skLineSegment(sketch, "E685", {"start": v(-9.1, 3.04) * mm, "end": v(-9.1, 0) * mm});
            skLineSegment(sketch, "E686", {"start": v(-9.1, 0) * mm, "end": v(-15.18, 0) * mm});
            skLineSegment(sketch, "E687", {"start": v(-15.18, 0) * mm, "end": v(-15.18, 3.04) * mm});
            skLineSegment(sketch, "E688", {"start": v(-15.18, 3.04) * mm, "end": v(-21.25, 3.04) * mm});
            skLineSegment(sketch, "E689", {"start": v(-21.25, 3.04) * mm, "end": v(-21.25, 0) * mm});
            skLineSegment(sketch, "E690", {"start": v(-21.25, 0) * mm, "end": v(-27.33, 0) * mm});
            skLineSegment(sketch, "E691", {"start": v(-27.33, 0) * mm, "end": v(-27.33, 3.04) * mm});
            skLineSegment(sketch, "E692", {"start": v(-27.33, 3.04) * mm, "end": v(-33.4, 3.04) * mm});
            skLineSegment(sketch, "E693", {"start": v(-33.4, 3.04) * mm, "end": v(-33.4, 0) * mm});
            skLineSegment(sketch, "E694", {"start": v(-33.4, 0) * mm, "end": v(-39.47, 0) * mm});
            skLineSegment(sketch, "E695", {"start": v(-39.47, 0) * mm, "end": v(-39.47, 3.04) * mm});
            skLineSegment(sketch, "E696", {"start": v(-39.47, 3.04) * mm, "end": v(-45.55, 3.04) * mm});
            skLineSegment(sketch, "E697", {"start": v(-45.55, 3.04) * mm, "end": v(-45.55, 0) * mm});
            skLineSegment(sketch, "E698", {"start": v(-45.55, 0) * mm, "end": v(-51.62, 0) * mm});
            skLineSegment(sketch, "E699", {"start": v(-51.62, 0) * mm, "end": v(-51.62, 3.04) * mm});
            skLineSegment(sketch, "E700", {"start": v(-51.62, 3.04) * mm, "end": v(-57.7, 3.04) * mm});
            skLineSegment(sketch, "E701", {"start": v(-57.7, 3.04) * mm, "end": v(-57.7, 0) * mm});
            skLineSegment(sketch, "E702", {"start": v(-57.7, 0) * mm, "end": v(-63.77, 0) * mm});
            skLineSegment(sketch, "E703", {"start": v(-63.77, 0) * mm, "end": v(-63.77, 3.04) * mm});
            skLineSegment(sketch, "E704", {"start": v(-63.77, 3.04) * mm, "end": v(-69.84, 3.04) * mm});
            skLineSegment(sketch, "E705", {"start": v(-69.84, 3.04) * mm, "end": v(-69.84, 0) * mm});
            skLineSegment(sketch, "E706", {"start": v(-69.84, 0) * mm, "end": v(-75.91, 0) * mm});
            skLineSegment(sketch, "E707", {"start": v(-75.91, 0) * mm, "end": v(-75.91, 3.04) * mm});
            skLineSegment(sketch, "E708", {"start": v(-75.91, 3.04) * mm, "end": v(-83.5, 3.04) * mm});
            skLineSegment(sketch, "E709", {"start": v(-83.5, 3.04) * mm, "end": v(-83.5, 0) * mm});
            skLineSegment(sketch, "E710", {"start": v(-83.5, 0) * mm, "end": v(-91.1, 0) * mm});
            skLineSegment(sketch, "E711", {"start": v(-91.1, 0) * mm, "end": v(-91.1, 9.62) * mm});
            skLineSegment(sketch, "E712", {"start": v(-91.1, 9.62) * mm, "end": v(-88.06, 9.62) * mm});
            skLineSegment(sketch, "E713", {"start": v(-88.06, 9.62) * mm, "end": v(-88.06, 19.23) * mm});
            skLineSegment(sketch, "E714", {"start": v(-88.06, 19.23) * mm, "end": v(-91.1, 19.23) * mm});
            skLineSegment(sketch, "E715", {"start": v(-91.1, 19.23) * mm, "end": v(-91.1, 25.3) * mm});
            skLineSegment(sketch, "E716", {"start": v(-91.1, 25.3) * mm, "end": v(-88.06, 25.3) * mm});
            skLineSegment(sketch, "E717", {"start": v(-88.06, 25.3) * mm, "end": v(-88.06, 31.38) * mm});
            skLineSegment(sketch, "E718", {"start": v(-88.06, 31.38) * mm, "end": v(-91.1, 31.38) * mm});
            skLineSegment(sketch, "E719", {"start": v(-91.1, 31.38) * mm, "end": v(-91.1, 37.45) * mm});
            skLineSegment(sketch, "E720", {"start": v(-91.1, 37.45) * mm, "end": v(-88.06, 37.45) * mm});
            skLineSegment(sketch, "E721", {"start": v(-88.06, 37.45) * mm, "end": v(-88.06, 43.52) * mm});
            skLineSegment(sketch, "E722", {"start": v(-88.06, 43.52) * mm, "end": v(-91.1, 43.52) * mm});
            skLineSegment(sketch, "E723", {"start": v(-91.1, 43.52) * mm, "end": v(-91.1, 49.6) * mm});
            skLineSegment(sketch, "E724", {"start": v(-91.1, 49.6) * mm, "end": v(-88.06, 49.6) * mm});
            skLineSegment(sketch, "E725", {"start": v(-88.06, 49.6) * mm, "end": v(-88.06, 55.67) * mm});
            skLineSegment(sketch, "E726", {"start": v(-88.06, 55.67) * mm, "end": v(-91.1, 55.67) * mm});
            skLineSegment(sketch, "E727", {"start": v(-91.1, 55.67) * mm, "end": v(-91.1, 61.74) * mm});
            skLineSegment(sketch, "E728", {"start": v(-91.1, 61.74) * mm, "end": v(-88.06, 61.74) * mm});
            skLineSegment(sketch, "E729", {"start": v(-88.06, 61.74) * mm, "end": v(-88.06, 67.81) * mm});
            skLineSegment(sketch, "E730", {"start": v(-88.06, 67.81) * mm, "end": v(-91.1, 67.81) * mm});
            skLineSegment(sketch, "E731", {"start": v(-91.1, 67.81) * mm, "end": v(-91.1, 73.89) * mm});
            skLineSegment(sketch, "E732", {"start": v(-91.1, 73.89) * mm, "end": v(-88.06, 73.89) * mm});
            skLineSegment(sketch, "E733", {"start": v(-88.06, 73.89) * mm, "end": v(-88.06, 79.96) * mm});
            skLineSegment(sketch, "E734", {"start": v(-88.06, 79.96) * mm, "end": v(-91.1, 79.96) * mm});
            skLineSegment(sketch, "E735", {"start": v(-91.1, 79.96) * mm, "end": v(-91.1, 86.03) * mm});
            skLineSegment(sketch, "E736", {"start": v(-91.1, 86.03) * mm, "end": v(-88.06, 86.03) * mm});
            skLineSegment(sketch, "E737", {"start": v(-88.06, 86.03) * mm, "end": v(-88.06, 92.1) * mm});
            skLineSegment(sketch, "E738", {"start": v(-88.06, 92.1) * mm, "end": v(-91.1, 92.1) * mm});
            skLineSegment(sketch, "E739", {"start": v(-91.1, 92.1) * mm, "end": v(-91.1, 98.18) * mm});
            skLineSegment(sketch, "E740", {"start": v(-91.1, 98.18) * mm, "end": v(-88.06, 98.18) * mm});
            skLineSegment(sketch, "E741", {"start": v(-88.06, 98.18) * mm, "end": v(-88.06, 104.25) * mm});
            skLineSegment(sketch, "E742", {"start": v(-88.06, 104.25) * mm, "end": v(-91.1, 104.25) * mm});
            skLineSegment(sketch, "E743", {"start": v(-91.1, 104.25) * mm, "end": v(-91.1, 110.32) * mm});
            skLineSegment(sketch, "E744", {"start": v(-91.1, 110.32) * mm, "end": v(-88.06, 110.32) * mm});
            skLineSegment(sketch, "E745", {"start": v(-88.06, 110.32) * mm, "end": v(-88.06, 116.4) * mm});
            skLineSegment(sketch, "E746", {"start": v(-88.06, 116.4) * mm, "end": v(-91.1, 116.4) * mm});
            skLineSegment(sketch, "E747", {"start": v(-91.1, 116.4) * mm, "end": v(-91.1, 122.47) * mm});
            skLineSegment(sketch, "E748", {"start": v(-91.1, 122.47) * mm, "end": v(-88.06, 122.47) * mm});
            skLineSegment(sketch, "E749", {"start": v(-88.06, 122.47) * mm, "end": v(-88.06, 128.54) * mm});
            skLineSegment(sketch, "E750", {"start": v(-88.06, 128.54) * mm, "end": v(-91.1, 128.54) * mm});
            skLineSegment(sketch, "E751", {"start": v(-91.1, 128.54) * mm, "end": v(-91.1, 134.62) * mm});
            skLineSegment(sketch, "E752", {"start": v(-91.1, 134.62) * mm, "end": v(-88.06, 134.62) * mm});
            skLineSegment(sketch, "E753", {"start": v(-88.06, 134.62) * mm, "end": v(-88.06, 140.69) * mm});
            skLineSegment(sketch, "E754", {"start": v(-88.06, 140.69) * mm, "end": v(-91.1, 140.69) * mm});
            skLineSegment(sketch, "E755", {"start": v(-91.1, 140.69) * mm, "end": v(-91.1, 146.76) * mm});
            skLineSegment(sketch, "E756", {"start": v(-91.1, 146.76) * mm, "end": v(-88.06, 146.76) * mm});
            skLineSegment(sketch, "E757", {"start": v(-88.06, 146.76) * mm, "end": v(-88.06, 152.83) * mm});
            skLineSegment(sketch, "E758", {"start": v(-88.06, 152.83) * mm, "end": v(-91.1, 152.83) * mm});
            skLineSegment(sketch, "E759", {"start": v(-91.1, 152.83) * mm, "end": v(-91.1, 158.9) * mm});
            skLineSegment(sketch, "E760", {"start": v(-91.1, 158.9) * mm, "end": v(-88.06, 158.9) * mm});
            skLineSegment(sketch, "E761", {"start": v(-88.06, 158.9) * mm, "end": v(-88.06, 164.98) * mm});
            skLineSegment(sketch, "E762", {"start": v(-88.06, 164.98) * mm, "end": v(-91.1, 164.98) * mm});
            skLineSegment(sketch, "E763", {"start": v(-91.1, 164.98) * mm, "end": v(-91.1, 171.06) * mm});
            skLineSegment(sketch, "E764", {"start": v(-91.1, 171.06) * mm, "end": v(-88.06, 171.06) * mm});
            skLineSegment(sketch, "E765", {"start": v(-88.06, 171.06) * mm, "end": v(-88.06, 177.13) * mm});
            skLineSegment(sketch, "E766", {"start": v(-88.06, 177.13) * mm, "end": v(-91.1, 177.13) * mm});
            skLineSegment(sketch, "E767", {"start": v(-91.1, 177.13) * mm, "end": v(-91.1, 183.2) * mm});
            skLineSegment(sketch, "E768", {"start": v(-91.1, 183.2) * mm, "end": v(-88.06, 183.2) * mm});
            skLineSegment(sketch, "E769", {"start": v(-88.06, 183.2) * mm, "end": v(-88.06, 189.27) * mm});
            skLineSegment(sketch, "E770", {"start": v(-88.06, 189.27) * mm, "end": v(-91.1, 189.27) * mm});
            skLineSegment(sketch, "E771", {"start": v(-91.1, 189.27) * mm, "end": v(-91.1, 195.34) * mm});
            skLineSegment(sketch, "E772", {"start": v(-91.1, 195.34) * mm, "end": v(-88.06, 195.34) * mm});
            skLineSegment(sketch, "E773", {"start": v(-88.06, 195.34) * mm, "end": v(-88.06, 201.42) * mm});
            skLineSegment(sketch, "E774", {"start": v(-88.06, 201.42) * mm, "end": v(-91.1, 201.42) * mm});
            skLineSegment(sketch, "E775", {"start": v(-91.1, 201.42) * mm, "end": v(-91.1, 207.49) * mm});
            skLineSegment(sketch, "E776", {"start": v(-91.1, 207.49) * mm, "end": v(-88.06, 207.49) * mm});
            skLineSegment(sketch, "E777", {"start": v(-88.06, 207.49) * mm, "end": v(-88.06, 213.56) * mm});
            skLineSegment(sketch, "E778", {"start": v(-88.06, 213.56) * mm, "end": v(-91.1, 213.56) * mm});
            skLineSegment(sketch, "E779", {"start": v(-91.1, 213.56) * mm, "end": v(-91.1, 219.64) * mm});
            skLineSegment(sketch, "E780", {"start": v(-91.1, 219.64) * mm, "end": v(-88.06, 219.64) * mm});
            skLineSegment(sketch, "E781", {"start": v(-88.06, 219.64) * mm, "end": v(-88.06, 225.7) * mm});
            skLineSegment(sketch, "E782", {"start": v(-88.06, 225.7) * mm, "end": v(-91.1, 225.7) * mm});
            skLineSegment(sketch, "E783", {"start": v(-91.1, 225.7) * mm, "end": v(-91.1, 231.78) * mm});
            skLineSegment(sketch, "E784", {"start": v(-91.1, 231.78) * mm, "end": v(-88.06, 231.78) * mm});
            skLineSegment(sketch, "E785", {"start": v(-88.06, 231.78) * mm, "end": v(-88.06, 237.85) * mm});
            skLineSegment(sketch, "E786", {"start": v(-88.06, 237.85) * mm, "end": v(-91.1, 237.85) * mm});
            skLineSegment(sketch, "E787", {"start": v(-91.1, 237.85) * mm, "end": v(-91.1, 243.93) * mm});
            skLineSegment(sketch, "E788", {"start": v(-91.1, 243.93) * mm, "end": v(-88.06, 243.93) * mm});
            skLineSegment(sketch, "E789", {"start": v(-88.06, 243.93) * mm, "end": v(-88.06, 250) * mm});
            skLineSegment(sketch, "E790", {"start": v(-88.06, 250) * mm, "end": v(-91.1, 250) * mm});
            skLineSegment(sketch, "E791", {"start": v(-91.1, 250) * mm, "end": v(-91.1, 256.07) * mm});
            skLineSegment(sketch, "E792", {"start": v(-91.1, 256.07) * mm, "end": v(-88.06, 256.07) * mm});
            skLineSegment(sketch, "E793", {"start": v(-88.06, 256.07) * mm, "end": v(-88.06, 262.15) * mm});
            skLineSegment(sketch, "E794", {"start": v(-88.06, 262.15) * mm, "end": v(-91.1, 262.15) * mm});
            skLineSegment(sketch, "E795", {"start": v(-91.1, 262.15) * mm, "end": v(-91.1, 268.22) * mm});
            skLineSegment(sketch, "E796", {"start": v(-91.1, 268.22) * mm, "end": v(-88.06, 268.22) * mm});
            skLineSegment(sketch, "E797", {"start": v(-88.06, 268.22) * mm, "end": v(-88.06, 274.3) * mm});
            skLineSegment(sketch, "E798", {"start": v(-88.06, 274.3) * mm, "end": v(-91.1, 274.3) * mm});
            skLineSegment(sketch, "E799", {"start": v(-91.1, 274.3) * mm, "end": v(-91.1, 280.37) * mm});
            skLineSegment(sketch, "E800", {"start": v(-91.1, 280.37) * mm, "end": v(-88.06, 280.37) * mm});
            skLineSegment(sketch, "E801", {"start": v(-88.06, 280.37) * mm, "end": v(-88.06, 286.44) * mm});
            skLineSegment(sketch, "E802", {"start": v(-88.06, 286.44) * mm, "end": v(-91.1, 286.44) * mm});
            skLineSegment(sketch, "E803", {"start": v(-91.1, 286.44) * mm, "end": v(-91.1, 292.51) * mm});
            skLineSegment(sketch, "E804", {"start": v(-91.1, 292.51) * mm, "end": v(-88.06, 292.51) * mm});
            skLineSegment(sketch, "E805", {"start": v(-88.06, 292.51) * mm, "end": v(-88.06, 298.58) * mm});
            skLineSegment(sketch, "E806", {"start": v(-88.06, 298.58) * mm, "end": v(-91.1, 298.58) * mm});
            skLineSegment(sketch, "E807", {"start": v(-91.1, 298.58) * mm, "end": v(-91.1, 304.66) * mm});
            skLineSegment(sketch, "E808", {"start": v(-91.1, 304.66) * mm, "end": v(-88.06, 304.66) * mm});
            skLineSegment(sketch, "E809", {"start": v(-88.06, 304.66) * mm, "end": v(-88.06, 310.73) * mm});
            skLineSegment(sketch, "E810", {"start": v(-88.06, 310.73) * mm, "end": v(-91.1, 310.73) * mm});
            skLineSegment(sketch, "E811", {"start": v(-91.1, 310.73) * mm, "end": v(-91.1, 316.8) * mm});
            skLineSegment(sketch, "E812", {"start": v(-91.1, 316.8) * mm, "end": v(-88.06, 316.8) * mm});
            skLineSegment(sketch, "E813", {"start": v(-88.06, 316.8) * mm, "end": v(-88.06, 322.87) * mm});
            skLineSegment(sketch, "E814", {"start": v(-88.06, 322.87) * mm, "end": v(-91.1, 322.87) * mm});
            skLineSegment(sketch, "E815", {"start": v(-91.1, 322.87) * mm, "end": v(-91.1, 328.95) * mm});
            skLineSegment(sketch, "E816", {"start": v(-91.1, 328.95) * mm, "end": v(-88.06, 328.95) * mm});
            skLineSegment(sketch, "E817", {"start": v(-88.06, 328.95) * mm, "end": v(-88.06, 335.02) * mm});
            skLineSegment(sketch, "E818", {"start": v(-88.06, 335.02) * mm, "end": v(-91.1, 335.02) * mm});
            skLineSegment(sketch, "E819", {"start": v(-91.1, 335.02) * mm, "end": v(-91.1, 341.1) * mm});
            skLineSegment(sketch, "E820", {"start": v(-91.1, 341.1) * mm, "end": v(-88.06, 341.1) * mm});
            skLineSegment(sketch, "E821", {"start": v(-88.06, 341.1) * mm, "end": v(-88.06, 347.16) * mm});
            skLineSegment(sketch, "E822", {"start": v(-88.06, 347.16) * mm, "end": v(-91.1, 347.16) * mm});
            skLineSegment(sketch, "E823", {"start": v(-91.1, 347.16) * mm, "end": v(-91.1, 353.24) * mm});
            skLineSegment(sketch, "E824", {"start": v(-91.1, 353.24) * mm, "end": v(-88.06, 353.24) * mm});
            skLineSegment(sketch, "E825", {"start": v(-88.06, 353.24) * mm, "end": v(-88.06, 359.31) * mm});
            skLineSegment(sketch, "E826", {"start": v(-88.06, 359.31) * mm, "end": v(-91.1, 359.31) * mm});
            skLineSegment(sketch, "E827", {"start": v(-91.1, 359.31) * mm, "end": v(-91.1, 365.39) * mm});
            skLineSegment(sketch, "E828", {"start": v(-91.1, 365.39) * mm, "end": v(-88.06, 365.39) * mm});
            skLineSegment(sketch, "E829", {"start": v(-88.06, 365.39) * mm, "end": v(-88.06, 371.46) * mm});
            skLineSegment(sketch, "E830", {"start": v(-88.06, 371.46) * mm, "end": v(-91.1, 371.46) * mm});
            skLineSegment(sketch, "E831", {"start": v(-91.1, 371.46) * mm, "end": v(-91.1, 377.53) * mm});
            skLineSegment(sketch, "E832", {"start": v(-91.1, 377.53) * mm, "end": v(-88.06, 377.53) * mm});
            skLineSegment(sketch, "E833", {"start": v(-88.06, 377.53) * mm, "end": v(-88.06, 383.6) * mm});
            skLineSegment(sketch, "E834", {"start": v(-88.06, 383.6) * mm, "end": v(-91.1, 383.6) * mm});
            skLineSegment(sketch, "E835", {"start": v(-91.1, 383.6) * mm, "end": v(-91.1, 389.68) * mm});
            skLineSegment(sketch, "E836", {"start": v(-91.1, 389.68) * mm, "end": v(-88.06, 389.68) * mm});
            skLineSegment(sketch, "E837", {"start": v(-88.06, 389.68) * mm, "end": v(-88.06, 395.75) * mm});
            skLineSegment(sketch, "E838", {"start": v(-88.06, 395.75) * mm, "end": v(-91.1, 395.75) * mm});
            skLineSegment(sketch, "E839", {"start": v(-91.1, 395.75) * mm, "end": v(-91.1, 401.82) * mm});
            skLineSegment(sketch, "E840", {"start": v(-91.1, 401.82) * mm, "end": v(-88.06, 401.82) * mm});
            skLineSegment(sketch, "E841", {"start": v(-88.06, 401.82) * mm, "end": v(-88.06, 407.9) * mm});
            skLineSegment(sketch, "E842", {"start": v(-88.06, 407.9) * mm, "end": v(-91.1, 407.9) * mm});
            skLineSegment(sketch, "E843", {"start": v(-91.1, 407.9) * mm, "end": v(-91.1, 413.97) * mm});
            skLineSegment(sketch, "E844", {"start": v(-91.1, 413.97) * mm, "end": v(-88.06, 413.97) * mm});
            skLineSegment(sketch, "E845", {"start": v(-88.06, 413.97) * mm, "end": v(-88.06, 420.04) * mm});
            skLineSegment(sketch, "E846", {"start": v(-88.06, 420.04) * mm, "end": v(-91.1, 420.04) * mm});
            skLineSegment(sketch, "E847", {"start": v(-91.1, 420.04) * mm, "end": v(-91.1, 426.11) * mm});
            skLineSegment(sketch, "E848", {"start": v(-91.1, 426.11) * mm, "end": v(-88.06, 426.11) * mm});
            skLineSegment(sketch, "E849", {"start": v(-88.06, 426.11) * mm, "end": v(-88.06, 432.18) * mm});
            skLineSegment(sketch, "E850", {"start": v(-88.06, 432.18) * mm, "end": v(-91.1, 432.18) * mm});
            skLineSegment(sketch, "E851", {"start": v(-91.1, 432.18) * mm, "end": v(-91.1, 438.26) * mm});
            skLineSegment(sketch, "E852", {"start": v(-91.1, 438.26) * mm, "end": v(-88.06, 438.26) * mm});
            skLineSegment(sketch, "E853", {"start": v(-88.06, 438.26) * mm, "end": v(-88.06, 444.33) * mm});
            skLineSegment(sketch, "E854", {"start": v(-88.06, 444.33) * mm, "end": v(-91.1, 444.33) * mm});
            skLineSegment(sketch, "E855", {"start": v(-91.1, 444.33) * mm, "end": v(-91.1, 450.4) * mm});
            skLineSegment(sketch, "E856", {"start": v(-91.1, 450.4) * mm, "end": v(-88.06, 450.4) * mm});
            skLineSegment(sketch, "E857", {"start": v(-88.06, 450.4) * mm, "end": v(-88.06, 456.48) * mm});
            skLineSegment(sketch, "E858", {"start": v(-88.06, 456.48) * mm, "end": v(-91.1, 456.48) * mm});
            skLineSegment(sketch, "E859", {"start": v(-91.1, 456.48) * mm, "end": v(-91.1, 462.55) * mm});
            skLineSegment(sketch, "E860", {"start": v(-91.1, 462.55) * mm, "end": v(-88.06, 462.55) * mm});
            skLineSegment(sketch, "E861", {"start": v(-88.06, 462.55) * mm, "end": v(-88.06, 468.62) * mm});
            skLineSegment(sketch, "E862", {"start": v(-88.06, 468.62) * mm, "end": v(-91.1, 468.62) * mm});
            skLineSegment(sketch, "E863", {"start": v(-91.1, 468.62) * mm, "end": v(-91.1, 474.7) * mm});
            skLineSegment(sketch, "E864", {"start": v(-91.1, 474.7) * mm, "end": v(-88.06, 474.7) * mm});
            skLineSegment(sketch, "E865", {"start": v(-88.06, 474.7) * mm, "end": v(-88.06, 480.77) * mm});
            skLineSegment(sketch, "E866", {"start": v(-88.06, 480.77) * mm, "end": v(-91.1, 480.77) * mm});
            skLineSegment(sketch, "E867", {"start": v(-91.1, 480.77) * mm, "end": v(-91.1, 486.84) * mm});
            skLineSegment(sketch, "E868", {"start": v(-91.1, 486.84) * mm, "end": v(-88.06, 486.84) * mm});
            skLineSegment(sketch, "E869", {"start": v(-88.06, 486.84) * mm, "end": v(-88.06, 496.46) * mm});
            skLineSegment(sketch, "E870", {"start": v(-88.06, 496.46) * mm, "end": v(-91.1, 496.46) * mm});
            skLineSegment(sketch, "E871", {"start": v(-91.1, 496.46) * mm, "end": v(-91.1, 506.07) * mm});
            skLineSegment(sketch, "E872", {"start": v(94.13, 506.07) * mm, "end": v(98.68, 506.07) * mm});
            skLineSegment(sketch, "E873", {"start": v(98.68, 506.07) * mm, "end": v(98.68, 503.04) * mm});
            skLineSegment(sketch, "E874", {"start": v(98.68, 503.04) * mm, "end": v(106.28, 503.04) * mm});
            skLineSegment(sketch, "E875", {"start": v(106.28, 503.04) * mm, "end": v(106.28, 506.07) * mm});
            skLineSegment(sketch, "E876", {"start": v(106.28, 506.07) * mm, "end": v(112.35, 506.07) * mm});
            skLineSegment(sketch, "E877", {"start": v(112.35, 506.07) * mm, "end": v(112.35, 503.04) * mm});
            skLineSegment(sketch, "E878", {"start": v(112.35, 503.04) * mm, "end": v(118.42, 503.04) * mm});
            skLineSegment(sketch, "E879", {"start": v(118.42, 503.04) * mm, "end": v(118.42, 506.07) * mm});
            skLineSegment(sketch, "E880", {"start": v(118.42, 506.07) * mm, "end": v(124.5, 506.07) * mm});
            skLineSegment(sketch, "E881", {"start": v(124.5, 506.07) * mm, "end": v(124.5, 503.04) * mm});
            skLineSegment(sketch, "E882", {"start": v(124.5, 503.04) * mm, "end": v(130.56, 503.04) * mm});
            skLineSegment(sketch, "E883", {"start": v(130.56, 503.04) * mm, "end": v(130.56, 506.07) * mm});
            skLineSegment(sketch, "E884", {"start": v(130.56, 506.07) * mm, "end": v(136.64, 506.07) * mm});
            skLineSegment(sketch, "E885", {"start": v(136.64, 506.07) * mm, "end": v(136.64, 503.04) * mm});
            skLineSegment(sketch, "E886", {"start": v(136.64, 503.04) * mm, "end": v(142.71, 503.04) * mm});
            skLineSegment(sketch, "E887", {"start": v(142.71, 503.04) * mm, "end": v(142.71, 506.07) * mm});
            skLineSegment(sketch, "E888", {"start": v(142.71, 506.07) * mm, "end": v(148.79, 506.07) * mm});
            skLineSegment(sketch, "E889", {"start": v(148.79, 506.07) * mm, "end": v(148.79, 503.04) * mm});
            skLineSegment(sketch, "E890", {"start": v(148.79, 503.04) * mm, "end": v(154.86, 503.04) * mm});
            skLineSegment(sketch, "E891", {"start": v(154.86, 503.04) * mm, "end": v(154.86, 506.07) * mm});
            skLineSegment(sketch, "E892", {"start": v(154.86, 506.07) * mm, "end": v(160.93, 506.07) * mm});
            skLineSegment(sketch, "E893", {"start": v(160.93, 506.07) * mm, "end": v(160.93, 503.04) * mm});
            skLineSegment(sketch, "E894", {"start": v(160.93, 503.04) * mm, "end": v(167, 503.04) * mm});
            skLineSegment(sketch, "E895", {"start": v(167, 503.04) * mm, "end": v(167, 506.07) * mm});
            skLineSegment(sketch, "E896", {"start": v(167, 506.07) * mm, "end": v(173.08, 506.07) * mm});
            skLineSegment(sketch, "E897", {"start": v(173.08, 506.07) * mm, "end": v(173.08, 503.04) * mm});
            skLineSegment(sketch, "E898", {"start": v(173.08, 503.04) * mm, "end": v(179.15, 503.04) * mm});
            skLineSegment(sketch, "E899", {"start": v(179.15, 503.04) * mm, "end": v(179.15, 506.07) * mm});
            skLineSegment(sketch, "E900", {"start": v(179.15, 506.07) * mm, "end": v(185.22, 506.07) * mm});
            skLineSegment(sketch, "E901", {"start": v(185.22, 506.07) * mm, "end": v(185.22, 503.04) * mm});
            skLineSegment(sketch, "E902", {"start": v(185.22, 503.04) * mm, "end": v(191.3, 503.04) * mm});
            skLineSegment(sketch, "E903", {"start": v(191.3, 503.04) * mm, "end": v(191.3, 506.07) * mm});
            skLineSegment(sketch, "E904", {"start": v(191.3, 506.07) * mm, "end": v(197.37, 506.07) * mm});
            skLineSegment(sketch, "E905", {"start": v(197.37, 506.07) * mm, "end": v(197.37, 503.04) * mm});
            skLineSegment(sketch, "E906", {"start": v(197.37, 503.04) * mm, "end": v(203.44, 503.04) * mm});
            skLineSegment(sketch, "E907", {"start": v(203.44, 503.04) * mm, "end": v(203.44, 506.07) * mm});
            skLineSegment(sketch, "E908", {"start": v(203.44, 506.07) * mm, "end": v(209.51, 506.07) * mm});
            skLineSegment(sketch, "E909", {"start": v(209.51, 506.07) * mm, "end": v(209.51, 503.04) * mm});
            skLineSegment(sketch, "E910", {"start": v(209.51, 503.04) * mm, "end": v(215.59, 503.04) * mm});
            skLineSegment(sketch, "E911", {"start": v(215.59, 503.04) * mm, "end": v(215.59, 506.07) * mm});
            skLineSegment(sketch, "E912", {"start": v(215.59, 506.07) * mm, "end": v(221.66, 506.07) * mm});
            skLineSegment(sketch, "E913", {"start": v(221.66, 506.07) * mm, "end": v(221.66, 503.04) * mm});
            skLineSegment(sketch, "E914", {"start": v(221.66, 503.04) * mm, "end": v(227.73, 503.04) * mm});
            skLineSegment(sketch, "E915", {"start": v(227.73, 503.04) * mm, "end": v(227.73, 506.07) * mm});
            skLineSegment(sketch, "E916", {"start": v(227.73, 506.07) * mm, "end": v(233.8, 506.07) * mm});
            skLineSegment(sketch, "E917", {"start": v(233.8, 506.07) * mm, "end": v(233.8, 503.04) * mm});
            skLineSegment(sketch, "E918", {"start": v(233.8, 503.04) * mm, "end": v(239.88, 503.04) * mm});
            skLineSegment(sketch, "E919", {"start": v(239.88, 503.04) * mm, "end": v(239.88, 506.07) * mm});
            skLineSegment(sketch, "E920", {"start": v(239.88, 506.07) * mm, "end": v(245.95, 506.07) * mm});
            skLineSegment(sketch, "E921", {"start": v(245.95, 506.07) * mm, "end": v(245.95, 503.04) * mm});
            skLineSegment(sketch, "E922", {"start": v(245.95, 503.04) * mm, "end": v(252.02, 503.04) * mm});
            skLineSegment(sketch, "E923", {"start": v(252.02, 503.04) * mm, "end": v(252.02, 506.07) * mm});
            skLineSegment(sketch, "E924", {"start": v(252.02, 506.07) * mm, "end": v(258.1, 506.07) * mm});
            skLineSegment(sketch, "E925", {"start": v(258.1, 506.07) * mm, "end": v(258.1, 503.04) * mm});
            skLineSegment(sketch, "E926", {"start": v(258.1, 503.04) * mm, "end": v(265.69, 503.04) * mm});
            skLineSegment(sketch, "E927", {"start": v(265.69, 503.04) * mm, "end": v(265.69, 506.07) * mm});
            skLineSegment(sketch, "E928", {"start": v(265.69, 506.07) * mm, "end": v(270.24, 506.07) * mm});
            skLineSegment(sketch, "E929", {"start": v(270.24, 506.07) * mm, "end": v(270.24, 496.46) * mm});
            skLineSegment(sketch, "E930", {"start": v(270.24, 496.46) * mm, "end": v(273.28, 496.46) * mm});
            skLineSegment(sketch, "E931", {"start": v(273.28, 496.46) * mm, "end": v(273.28, 486.84) * mm});
            skLineSegment(sketch, "E932", {"start": v(273.28, 486.84) * mm, "end": v(270.24, 486.84) * mm});
            skLineSegment(sketch, "E933", {"start": v(270.24, 486.84) * mm, "end": v(270.24, 480.77) * mm});
            skLineSegment(sketch, "E934", {"start": v(270.24, 480.77) * mm, "end": v(273.28, 480.77) * mm});
            skLineSegment(sketch, "E935", {"start": v(273.28, 480.77) * mm, "end": v(273.28, 474.7) * mm});
            skLineSegment(sketch, "E936", {"start": v(273.28, 474.7) * mm, "end": v(270.24, 474.7) * mm});
            skLineSegment(sketch, "E937", {"start": v(270.24, 474.7) * mm, "end": v(270.24, 468.62) * mm});
            skLineSegment(sketch, "E938", {"start": v(270.24, 468.62) * mm, "end": v(273.28, 468.62) * mm});
            skLineSegment(sketch, "E939", {"start": v(273.28, 468.62) * mm, "end": v(273.28, 462.55) * mm});
            skLineSegment(sketch, "E940", {"start": v(273.28, 462.55) * mm, "end": v(270.24, 462.55) * mm});
            skLineSegment(sketch, "E941", {"start": v(270.24, 462.55) * mm, "end": v(270.24, 456.48) * mm});
            skLineSegment(sketch, "E942", {"start": v(270.24, 456.48) * mm, "end": v(273.28, 456.48) * mm});
            skLineSegment(sketch, "E943", {"start": v(273.28, 456.48) * mm, "end": v(273.28, 450.4) * mm});
            skLineSegment(sketch, "E944", {"start": v(273.28, 450.4) * mm, "end": v(270.24, 450.4) * mm});
            skLineSegment(sketch, "E945", {"start": v(270.24, 450.4) * mm, "end": v(270.24, 444.33) * mm});
            skLineSegment(sketch, "E946", {"start": v(270.24, 444.33) * mm, "end": v(273.28, 444.33) * mm});
            skLineSegment(sketch, "E947", {"start": v(273.28, 444.33) * mm, "end": v(273.28, 438.26) * mm});
            skLineSegment(sketch, "E948", {"start": v(273.28, 438.26) * mm, "end": v(270.24, 438.26) * mm});
            skLineSegment(sketch, "E949", {"start": v(270.24, 438.26) * mm, "end": v(270.24, 432.18) * mm});
            skLineSegment(sketch, "E950", {"start": v(270.24, 432.18) * mm, "end": v(273.28, 432.18) * mm});
            skLineSegment(sketch, "E951", {"start": v(273.28, 432.18) * mm, "end": v(273.28, 426.11) * mm});
            skLineSegment(sketch, "E952", {"start": v(273.28, 426.11) * mm, "end": v(270.24, 426.11) * mm});
            skLineSegment(sketch, "E953", {"start": v(270.24, 426.11) * mm, "end": v(270.24, 420.04) * mm});
            skLineSegment(sketch, "E954", {"start": v(270.24, 420.04) * mm, "end": v(273.28, 420.04) * mm});
            skLineSegment(sketch, "E955", {"start": v(273.28, 420.04) * mm, "end": v(273.28, 413.97) * mm});
            skLineSegment(sketch, "E956", {"start": v(273.28, 413.97) * mm, "end": v(270.24, 413.97) * mm});
            skLineSegment(sketch, "E957", {"start": v(270.24, 413.97) * mm, "end": v(270.24, 407.9) * mm});
            skLineSegment(sketch, "E958", {"start": v(270.24, 407.9) * mm, "end": v(273.28, 407.9) * mm});
            skLineSegment(sketch, "E959", {"start": v(273.28, 407.9) * mm, "end": v(273.28, 401.82) * mm});
            skLineSegment(sketch, "E960", {"start": v(273.28, 401.82) * mm, "end": v(270.24, 401.82) * mm});
            skLineSegment(sketch, "E961", {"start": v(270.24, 401.82) * mm, "end": v(270.24, 395.75) * mm});
            skLineSegment(sketch, "E962", {"start": v(270.24, 395.75) * mm, "end": v(273.28, 395.75) * mm});
            skLineSegment(sketch, "E963", {"start": v(273.28, 395.75) * mm, "end": v(273.28, 389.68) * mm});
            skLineSegment(sketch, "E964", {"start": v(273.28, 389.68) * mm, "end": v(270.24, 389.68) * mm});
            skLineSegment(sketch, "E965", {"start": v(270.24, 389.68) * mm, "end": v(270.24, 383.6) * mm});
            skLineSegment(sketch, "E966", {"start": v(270.24, 383.6) * mm, "end": v(273.28, 383.6) * mm});
            skLineSegment(sketch, "E967", {"start": v(273.28, 383.6) * mm, "end": v(273.28, 377.53) * mm});
            skLineSegment(sketch, "E968", {"start": v(273.28, 377.53) * mm, "end": v(270.24, 377.53) * mm});
            skLineSegment(sketch, "E969", {"start": v(270.24, 377.53) * mm, "end": v(270.24, 371.46) * mm});
            skLineSegment(sketch, "E970", {"start": v(270.24, 371.46) * mm, "end": v(273.28, 371.46) * mm});
            skLineSegment(sketch, "E971", {"start": v(273.28, 371.46) * mm, "end": v(273.28, 365.39) * mm});
            skLineSegment(sketch, "E972", {"start": v(273.28, 365.39) * mm, "end": v(270.24, 365.39) * mm});
            skLineSegment(sketch, "E973", {"start": v(270.24, 365.39) * mm, "end": v(270.24, 359.31) * mm});
            skLineSegment(sketch, "E974", {"start": v(270.24, 359.31) * mm, "end": v(273.28, 359.31) * mm});
            skLineSegment(sketch, "E975", {"start": v(273.28, 359.31) * mm, "end": v(273.28, 353.24) * mm});
            skLineSegment(sketch, "E976", {"start": v(273.28, 353.24) * mm, "end": v(270.24, 353.24) * mm});
            skLineSegment(sketch, "E977", {"start": v(270.24, 353.24) * mm, "end": v(270.24, 347.16) * mm});
            skLineSegment(sketch, "E978", {"start": v(270.24, 347.16) * mm, "end": v(273.28, 347.16) * mm});
            skLineSegment(sketch, "E979", {"start": v(273.28, 347.16) * mm, "end": v(273.28, 341.1) * mm});
            skLineSegment(sketch, "E980", {"start": v(273.28, 341.1) * mm, "end": v(270.24, 341.1) * mm});
            skLineSegment(sketch, "E981", {"start": v(270.24, 341.1) * mm, "end": v(270.24, 335.02) * mm});
            skLineSegment(sketch, "E982", {"start": v(270.24, 335.02) * mm, "end": v(273.28, 335.02) * mm});
            skLineSegment(sketch, "E983", {"start": v(273.28, 335.02) * mm, "end": v(273.28, 328.95) * mm});
            skLineSegment(sketch, "E984", {"start": v(273.28, 328.95) * mm, "end": v(270.24, 328.95) * mm});
            skLineSegment(sketch, "E985", {"start": v(270.24, 328.95) * mm, "end": v(270.24, 322.87) * mm});
            skLineSegment(sketch, "E986", {"start": v(270.24, 322.87) * mm, "end": v(273.28, 322.87) * mm});
            skLineSegment(sketch, "E987", {"start": v(273.28, 322.87) * mm, "end": v(273.28, 316.8) * mm});
            skLineSegment(sketch, "E988", {"start": v(273.28, 316.8) * mm, "end": v(270.24, 316.8) * mm});
            skLineSegment(sketch, "E989", {"start": v(270.24, 316.8) * mm, "end": v(270.24, 310.73) * mm});
            skLineSegment(sketch, "E990", {"start": v(270.24, 310.73) * mm, "end": v(273.28, 310.73) * mm});
            skLineSegment(sketch, "E991", {"start": v(273.28, 310.73) * mm, "end": v(273.28, 304.66) * mm});
            skLineSegment(sketch, "E992", {"start": v(273.28, 304.66) * mm, "end": v(270.24, 304.66) * mm});
            skLineSegment(sketch, "E993", {"start": v(270.24, 304.66) * mm, "end": v(270.24, 298.58) * mm});
            skLineSegment(sketch, "E994", {"start": v(270.24, 298.58) * mm, "end": v(273.28, 298.58) * mm});
            skLineSegment(sketch, "E995", {"start": v(273.28, 298.58) * mm, "end": v(273.28, 292.51) * mm});
            skLineSegment(sketch, "E996", {"start": v(273.28, 292.51) * mm, "end": v(270.24, 292.51) * mm});
            skLineSegment(sketch, "E997", {"start": v(270.24, 292.51) * mm, "end": v(270.24, 286.44) * mm});
            skLineSegment(sketch, "E998", {"start": v(270.24, 286.44) * mm, "end": v(273.28, 286.44) * mm});
            skLineSegment(sketch, "E999", {"start": v(273.28, 286.44) * mm, "end": v(273.28, 280.37) * mm});
            skLineSegment(sketch, "E1000", {"start": v(273.28, 280.37) * mm, "end": v(270.24, 280.37) * mm});
            skLineSegment(sketch, "E1001", {"start": v(270.24, 280.37) * mm, "end": v(270.24, 274.3) * mm});
            skLineSegment(sketch, "E1002", {"start": v(270.24, 274.3) * mm, "end": v(273.28, 274.3) * mm});
            skLineSegment(sketch, "E1003", {"start": v(273.28, 274.3) * mm, "end": v(273.28, 268.22) * mm});
            skLineSegment(sketch, "E1004", {"start": v(273.28, 268.22) * mm, "end": v(270.24, 268.22) * mm});
            skLineSegment(sketch, "E1005", {"start": v(270.24, 268.22) * mm, "end": v(270.24, 262.15) * mm});
            skLineSegment(sketch, "E1006", {"start": v(270.24, 262.15) * mm, "end": v(273.28, 262.15) * mm});
            skLineSegment(sketch, "E1007", {"start": v(273.28, 262.15) * mm, "end": v(273.28, 256.07) * mm});
            skLineSegment(sketch, "E1008", {"start": v(273.28, 256.07) * mm, "end": v(270.24, 256.07) * mm});
            skLineSegment(sketch, "E1009", {"start": v(270.24, 256.07) * mm, "end": v(270.24, 250) * mm});
            skLineSegment(sketch, "E1010", {"start": v(270.24, 250) * mm, "end": v(273.28, 250) * mm});
            skLineSegment(sketch, "E1011", {"start": v(273.28, 250) * mm, "end": v(273.28, 243.93) * mm});
            skLineSegment(sketch, "E1012", {"start": v(273.28, 243.93) * mm, "end": v(270.24, 243.93) * mm});
            skLineSegment(sketch, "E1013", {"start": v(270.24, 243.93) * mm, "end": v(270.24, 237.85) * mm});
            skLineSegment(sketch, "E1014", {"start": v(270.24, 237.85) * mm, "end": v(273.28, 237.85) * mm});
            skLineSegment(sketch, "E1015", {"start": v(273.28, 237.85) * mm, "end": v(273.28, 231.78) * mm});
            skLineSegment(sketch, "E1016", {"start": v(273.28, 231.78) * mm, "end": v(270.24, 231.78) * mm});
            skLineSegment(sketch, "E1017", {"start": v(270.24, 231.78) * mm, "end": v(270.24, 225.7) * mm});
            skLineSegment(sketch, "E1018", {"start": v(270.24, 225.7) * mm, "end": v(273.28, 225.7) * mm});
            skLineSegment(sketch, "E1019", {"start": v(273.28, 225.7) * mm, "end": v(273.28, 219.64) * mm});
            skLineSegment(sketch, "E1020", {"start": v(273.28, 219.64) * mm, "end": v(270.24, 219.64) * mm});
            skLineSegment(sketch, "E1021", {"start": v(270.24, 219.64) * mm, "end": v(270.24, 213.56) * mm});
            skLineSegment(sketch, "E1022", {"start": v(270.24, 213.56) * mm, "end": v(273.28, 213.56) * mm});
            skLineSegment(sketch, "E1023", {"start": v(273.28, 213.56) * mm, "end": v(273.28, 207.49) * mm});
            skLineSegment(sketch, "E1024", {"start": v(273.28, 207.49) * mm, "end": v(270.24, 207.49) * mm});
            skLineSegment(sketch, "E1025", {"start": v(270.24, 207.49) * mm, "end": v(270.24, 201.42) * mm});
            skLineSegment(sketch, "E1026", {"start": v(270.24, 201.42) * mm, "end": v(273.28, 201.42) * mm});
            skLineSegment(sketch, "E1027", {"start": v(273.28, 201.42) * mm, "end": v(273.28, 195.34) * mm});
            skLineSegment(sketch, "E1028", {"start": v(273.28, 195.34) * mm, "end": v(270.24, 195.34) * mm});
            skLineSegment(sketch, "E1029", {"start": v(270.24, 195.34) * mm, "end": v(270.24, 189.27) * mm});
            skLineSegment(sketch, "E1030", {"start": v(270.24, 189.27) * mm, "end": v(273.28, 189.27) * mm});
            skLineSegment(sketch, "E1031", {"start": v(273.28, 189.27) * mm, "end": v(273.28, 183.2) * mm});
            skLineSegment(sketch, "E1032", {"start": v(273.28, 183.2) * mm, "end": v(270.24, 183.2) * mm});
            skLineSegment(sketch, "E1033", {"start": v(270.24, 183.2) * mm, "end": v(270.24, 177.13) * mm});
            skLineSegment(sketch, "E1034", {"start": v(270.24, 177.13) * mm, "end": v(273.28, 177.13) * mm});
            skLineSegment(sketch, "E1035", {"start": v(273.28, 177.13) * mm, "end": v(273.28, 171.06) * mm});
            skLineSegment(sketch, "E1036", {"start": v(273.28, 171.06) * mm, "end": v(270.24, 171.06) * mm});
            skLineSegment(sketch, "E1037", {"start": v(270.24, 171.06) * mm, "end": v(270.24, 164.98) * mm});
            skLineSegment(sketch, "E1038", {"start": v(270.24, 164.98) * mm, "end": v(273.28, 164.98) * mm});
            skLineSegment(sketch, "E1039", {"start": v(273.28, 164.98) * mm, "end": v(273.28, 158.9) * mm});
            skLineSegment(sketch, "E1040", {"start": v(273.28, 158.9) * mm, "end": v(270.24, 158.9) * mm});
            skLineSegment(sketch, "E1041", {"start": v(270.24, 158.9) * mm, "end": v(270.24, 152.83) * mm});
            skLineSegment(sketch, "E1042", {"start": v(270.24, 152.83) * mm, "end": v(273.28, 152.83) * mm});
            skLineSegment(sketch, "E1043", {"start": v(273.28, 152.83) * mm, "end": v(273.28, 146.76) * mm});
            skLineSegment(sketch, "E1044", {"start": v(273.28, 146.76) * mm, "end": v(270.24, 146.76) * mm});
            skLineSegment(sketch, "E1045", {"start": v(270.24, 146.76) * mm, "end": v(270.24, 140.69) * mm});
            skLineSegment(sketch, "E1046", {"start": v(270.24, 140.69) * mm, "end": v(273.28, 140.69) * mm});
            skLineSegment(sketch, "E1047", {"start": v(273.28, 140.69) * mm, "end": v(273.28, 134.62) * mm});
            skLineSegment(sketch, "E1048", {"start": v(273.28, 134.62) * mm, "end": v(270.24, 134.62) * mm});
            skLineSegment(sketch, "E1049", {"start": v(270.24, 134.62) * mm, "end": v(270.24, 128.54) * mm});
            skLineSegment(sketch, "E1050", {"start": v(270.24, 128.54) * mm, "end": v(273.28, 128.54) * mm});
            skLineSegment(sketch, "E1051", {"start": v(273.28, 128.54) * mm, "end": v(273.28, 122.47) * mm});
            skLineSegment(sketch, "E1052", {"start": v(273.28, 122.47) * mm, "end": v(270.24, 122.47) * mm});
            skLineSegment(sketch, "E1053", {"start": v(270.24, 122.47) * mm, "end": v(270.24, 116.4) * mm});
            skLineSegment(sketch, "E1054", {"start": v(270.24, 116.4) * mm, "end": v(273.28, 116.4) * mm});
            skLineSegment(sketch, "E1055", {"start": v(273.28, 116.4) * mm, "end": v(273.28, 110.32) * mm});
            skLineSegment(sketch, "E1056", {"start": v(273.28, 110.32) * mm, "end": v(270.24, 110.32) * mm});
            skLineSegment(sketch, "E1057", {"start": v(270.24, 110.32) * mm, "end": v(270.24, 104.25) * mm});
            skLineSegment(sketch, "E1058", {"start": v(270.24, 104.25) * mm, "end": v(273.28, 104.25) * mm});
            skLineSegment(sketch, "E1059", {"start": v(273.28, 104.25) * mm, "end": v(273.28, 98.18) * mm});
            skLineSegment(sketch, "E1060", {"start": v(273.28, 98.18) * mm, "end": v(270.24, 98.18) * mm});
            skLineSegment(sketch, "E1061", {"start": v(270.24, 98.18) * mm, "end": v(270.24, 92.1) * mm});
            skLineSegment(sketch, "E1062", {"start": v(270.24, 92.1) * mm, "end": v(273.28, 92.1) * mm});
            skLineSegment(sketch, "E1063", {"start": v(273.28, 92.1) * mm, "end": v(273.28, 86.03) * mm});
            skLineSegment(sketch, "E1064", {"start": v(273.28, 86.03) * mm, "end": v(270.24, 86.03) * mm});
            skLineSegment(sketch, "E1065", {"start": v(270.24, 86.03) * mm, "end": v(270.24, 79.96) * mm});
            skLineSegment(sketch, "E1066", {"start": v(270.24, 79.96) * mm, "end": v(273.28, 79.96) * mm});
            skLineSegment(sketch, "E1067", {"start": v(273.28, 79.96) * mm, "end": v(273.28, 73.89) * mm});
            skLineSegment(sketch, "E1068", {"start": v(273.28, 73.89) * mm, "end": v(270.24, 73.89) * mm});
            skLineSegment(sketch, "E1069", {"start": v(270.24, 73.89) * mm, "end": v(270.24, 67.81) * mm});
            skLineSegment(sketch, "E1070", {"start": v(270.24, 67.81) * mm, "end": v(273.28, 67.81) * mm});
            skLineSegment(sketch, "E1071", {"start": v(273.28, 67.81) * mm, "end": v(273.28, 61.74) * mm});
            skLineSegment(sketch, "E1072", {"start": v(273.28, 61.74) * mm, "end": v(270.24, 61.74) * mm});
            skLineSegment(sketch, "E1073", {"start": v(270.24, 61.74) * mm, "end": v(270.24, 55.67) * mm});
            skLineSegment(sketch, "E1074", {"start": v(270.24, 55.67) * mm, "end": v(273.28, 55.67) * mm});
            skLineSegment(sketch, "E1075", {"start": v(273.28, 55.67) * mm, "end": v(273.28, 49.6) * mm});
            skLineSegment(sketch, "E1076", {"start": v(273.28, 49.6) * mm, "end": v(270.24, 49.6) * mm});
            skLineSegment(sketch, "E1077", {"start": v(270.24, 49.6) * mm, "end": v(270.24, 43.52) * mm});
            skLineSegment(sketch, "E1078", {"start": v(270.24, 43.52) * mm, "end": v(273.28, 43.52) * mm});
            skLineSegment(sketch, "E1079", {"start": v(273.28, 43.52) * mm, "end": v(273.28, 37.45) * mm});
            skLineSegment(sketch, "E1080", {"start": v(273.28, 37.45) * mm, "end": v(270.24, 37.45) * mm});
            skLineSegment(sketch, "E1081", {"start": v(270.24, 37.45) * mm, "end": v(270.24, 31.38) * mm});
            skLineSegment(sketch, "E1082", {"start": v(270.24, 31.38) * mm, "end": v(273.28, 31.38) * mm});
            skLineSegment(sketch, "E1083", {"start": v(273.28, 31.38) * mm, "end": v(273.28, 25.3) * mm});
            skLineSegment(sketch, "E1084", {"start": v(273.28, 25.3) * mm, "end": v(270.24, 25.3) * mm});
            skLineSegment(sketch, "E1085", {"start": v(270.24, 25.3) * mm, "end": v(270.24, 19.23) * mm});
            skLineSegment(sketch, "E1086", {"start": v(270.24, 19.23) * mm, "end": v(273.28, 19.23) * mm});
            skLineSegment(sketch, "E1087", {"start": v(273.28, 19.23) * mm, "end": v(273.28, 9.62) * mm});
            skLineSegment(sketch, "E1088", {"start": v(273.28, 9.62) * mm, "end": v(270.24, 9.62) * mm});
            skLineSegment(sketch, "E1089", {"start": v(270.24, 9.62) * mm, "end": v(270.24, 0) * mm});
            skLineSegment(sketch, "E1090", {"start": v(270.24, 0) * mm, "end": v(265.69, 0) * mm});
            skLineSegment(sketch, "E1091", {"start": v(265.69, 0) * mm, "end": v(265.69, 3.04) * mm});
            skLineSegment(sketch, "E1092", {"start": v(265.69, 3.04) * mm, "end": v(258.1, 3.04) * mm});
            skLineSegment(sketch, "E1093", {"start": v(258.1, 3.04) * mm, "end": v(258.1, 0) * mm});
            skLineSegment(sketch, "E1094", {"start": v(258.1, 0) * mm, "end": v(252.02, 0) * mm});
            skLineSegment(sketch, "E1095", {"start": v(252.02, 0) * mm, "end": v(252.02, 3.04) * mm});
            skLineSegment(sketch, "E1096", {"start": v(252.02, 3.04) * mm, "end": v(245.95, 3.04) * mm});
            skLineSegment(sketch, "E1097", {"start": v(245.95, 3.04) * mm, "end": v(245.95, 0) * mm});
            skLineSegment(sketch, "E1098", {"start": v(245.95, 0) * mm, "end": v(239.88, 0) * mm});
            skLineSegment(sketch, "E1099", {"start": v(239.88, 0) * mm, "end": v(239.88, 3.04) * mm});
            skLineSegment(sketch, "E1100", {"start": v(239.88, 3.04) * mm, "end": v(233.8, 3.04) * mm});
            skLineSegment(sketch, "E1101", {"start": v(233.8, 3.04) * mm, "end": v(233.8, 0) * mm});
            skLineSegment(sketch, "E1102", {"start": v(233.8, 0) * mm, "end": v(227.73, 0) * mm});
            skLineSegment(sketch, "E1103", {"start": v(227.73, 0) * mm, "end": v(227.73, 3.04) * mm});
            skLineSegment(sketch, "E1104", {"start": v(227.73, 3.04) * mm, "end": v(221.66, 3.04) * mm});
            skLineSegment(sketch, "E1105", {"start": v(221.66, 3.04) * mm, "end": v(221.66, 0) * mm});
            skLineSegment(sketch, "E1106", {"start": v(221.66, 0) * mm, "end": v(215.59, 0) * mm});
            skLineSegment(sketch, "E1107", {"start": v(215.59, 0) * mm, "end": v(215.59, 3.04) * mm});
            skLineSegment(sketch, "E1108", {"start": v(215.59, 3.04) * mm, "end": v(209.51, 3.04) * mm});
            skLineSegment(sketch, "E1109", {"start": v(209.51, 3.04) * mm, "end": v(209.51, 0) * mm});
            skLineSegment(sketch, "E1110", {"start": v(209.51, 0) * mm, "end": v(203.44, 0) * mm});
            skLineSegment(sketch, "E1111", {"start": v(203.44, 0) * mm, "end": v(203.44, 3.04) * mm});
            skLineSegment(sketch, "E1112", {"start": v(203.44, 3.04) * mm, "end": v(197.37, 3.04) * mm});
            skLineSegment(sketch, "E1113", {"start": v(197.37, 3.04) * mm, "end": v(197.37, 0) * mm});
            skLineSegment(sketch, "E1114", {"start": v(197.37, 0) * mm, "end": v(191.3, 0) * mm});
            skLineSegment(sketch, "E1115", {"start": v(191.3, 0) * mm, "end": v(191.3, 3.04) * mm});
            skLineSegment(sketch, "E1116", {"start": v(191.3, 3.04) * mm, "end": v(185.22, 3.04) * mm});
            skLineSegment(sketch, "E1117", {"start": v(185.22, 3.04) * mm, "end": v(185.22, 0) * mm});
            skLineSegment(sketch, "E1118", {"start": v(185.22, 0) * mm, "end": v(179.15, 0) * mm});
            skLineSegment(sketch, "E1119", {"start": v(179.15, 0) * mm, "end": v(179.15, 3.04) * mm});
            skLineSegment(sketch, "E1120", {"start": v(179.15, 3.04) * mm, "end": v(173.08, 3.04) * mm});
            skLineSegment(sketch, "E1121", {"start": v(173.08, 3.04) * mm, "end": v(173.08, 0) * mm});
            skLineSegment(sketch, "E1122", {"start": v(173.08, 0) * mm, "end": v(167, 0) * mm});
            skLineSegment(sketch, "E1123", {"start": v(167, 0) * mm, "end": v(167, 3.04) * mm});
            skLineSegment(sketch, "E1124", {"start": v(167, 3.04) * mm, "end": v(160.93, 3.04) * mm});
            skLineSegment(sketch, "E1125", {"start": v(160.93, 3.04) * mm, "end": v(160.93, 0) * mm});
            skLineSegment(sketch, "E1126", {"start": v(160.93, 0) * mm, "end": v(154.86, 0) * mm});
            skLineSegment(sketch, "E1127", {"start": v(154.86, 0) * mm, "end": v(154.86, 3.04) * mm});
            skLineSegment(sketch, "E1128", {"start": v(154.86, 3.04) * mm, "end": v(148.79, 3.04) * mm});
            skLineSegment(sketch, "E1129", {"start": v(148.79, 3.04) * mm, "end": v(148.79, 0) * mm});
            skLineSegment(sketch, "E1130", {"start": v(148.79, 0) * mm, "end": v(142.71, 0) * mm});
            skLineSegment(sketch, "E1131", {"start": v(142.71, 0) * mm, "end": v(142.71, 3.04) * mm});
            skLineSegment(sketch, "E1132", {"start": v(142.71, 3.04) * mm, "end": v(136.64, 3.04) * mm});
            skLineSegment(sketch, "E1133", {"start": v(136.64, 3.04) * mm, "end": v(136.64, 0) * mm});
            skLineSegment(sketch, "E1134", {"start": v(136.64, 0) * mm, "end": v(130.56, 0) * mm});
            skLineSegment(sketch, "E1135", {"start": v(130.56, 0) * mm, "end": v(130.56, 3.04) * mm});
            skLineSegment(sketch, "E1136", {"start": v(130.56, 3.04) * mm, "end": v(124.5, 3.04) * mm});
            skLineSegment(sketch, "E1137", {"start": v(124.5, 3.04) * mm, "end": v(124.5, 0) * mm});
            skLineSegment(sketch, "E1138", {"start": v(124.5, 0) * mm, "end": v(118.42, 0) * mm});
            skLineSegment(sketch, "E1139", {"start": v(118.42, 0) * mm, "end": v(118.42, 3.04) * mm});
            skLineSegment(sketch, "E1140", {"start": v(118.42, 3.04) * mm, "end": v(112.35, 3.04) * mm});
            skLineSegment(sketch, "E1141", {"start": v(112.35, 3.04) * mm, "end": v(112.35, 0) * mm});
            skLineSegment(sketch, "E1142", {"start": v(112.35, 0) * mm, "end": v(106.28, 0) * mm});
            skLineSegment(sketch, "E1143", {"start": v(106.28, 0) * mm, "end": v(106.28, 3.04) * mm});
            skLineSegment(sketch, "E1144", {"start": v(106.28, 3.04) * mm, "end": v(98.68, 3.04) * mm});
            skLineSegment(sketch, "E1145", {"start": v(98.68, 3.04) * mm, "end": v(98.68, 0) * mm});
            skLineSegment(sketch, "E1146", {"start": v(98.68, 0) * mm, "end": v(94.13, 0) * mm});
            skLineSegment(sketch, "E1147", {"start": v(94.13, 0) * mm, "end": v(94.13, 9.62) * mm});
            skLineSegment(sketch, "E1148", {"start": v(94.13, 9.62) * mm, "end": v(91.1, 9.62) * mm});
            skLineSegment(sketch, "E1149", {"start": v(91.1, 9.62) * mm, "end": v(91.1, 19.23) * mm});
            skLineSegment(sketch, "E1150", {"start": v(91.1, 19.23) * mm, "end": v(94.13, 19.23) * mm});
            skLineSegment(sketch, "E1151", {"start": v(94.13, 19.23) * mm, "end": v(94.13, 25.3) * mm});
            skLineSegment(sketch, "E1152", {"start": v(94.13, 25.3) * mm, "end": v(91.1, 25.3) * mm});
            skLineSegment(sketch, "E1153", {"start": v(91.1, 25.3) * mm, "end": v(91.1, 31.38) * mm});
            skLineSegment(sketch, "E1154", {"start": v(91.1, 31.38) * mm, "end": v(94.13, 31.38) * mm});
            skLineSegment(sketch, "E1155", {"start": v(94.13, 31.38) * mm, "end": v(94.13, 37.45) * mm});
            skLineSegment(sketch, "E1156", {"start": v(94.13, 37.45) * mm, "end": v(91.1, 37.45) * mm});
            skLineSegment(sketch, "E1157", {"start": v(91.1, 37.45) * mm, "end": v(91.1, 43.52) * mm});
            skLineSegment(sketch, "E1158", {"start": v(91.1, 43.52) * mm, "end": v(94.13, 43.52) * mm});
            skLineSegment(sketch, "E1159", {"start": v(94.13, 43.52) * mm, "end": v(94.13, 49.6) * mm});
            skLineSegment(sketch, "E1160", {"start": v(94.13, 49.6) * mm, "end": v(91.1, 49.6) * mm});
            skLineSegment(sketch, "E1161", {"start": v(91.1, 49.6) * mm, "end": v(91.1, 55.67) * mm});
            skLineSegment(sketch, "E1162", {"start": v(91.1, 55.67) * mm, "end": v(94.13, 55.67) * mm});
            skLineSegment(sketch, "E1163", {"start": v(94.13, 55.67) * mm, "end": v(94.13, 61.74) * mm});
            skLineSegment(sketch, "E1164", {"start": v(94.13, 61.74) * mm, "end": v(91.1, 61.74) * mm});
            skLineSegment(sketch, "E1165", {"start": v(91.1, 61.74) * mm, "end": v(91.1, 67.81) * mm});
            skLineSegment(sketch, "E1166", {"start": v(91.1, 67.81) * mm, "end": v(94.13, 67.81) * mm});
            skLineSegment(sketch, "E1167", {"start": v(94.13, 67.81) * mm, "end": v(94.13, 73.89) * mm});
            skLineSegment(sketch, "E1168", {"start": v(94.13, 73.89) * mm, "end": v(91.1, 73.89) * mm});
            skLineSegment(sketch, "E1169", {"start": v(91.1, 73.89) * mm, "end": v(91.1, 79.96) * mm});
            skLineSegment(sketch, "E1170", {"start": v(91.1, 79.96) * mm, "end": v(94.13, 79.96) * mm});
            skLineSegment(sketch, "E1171", {"start": v(94.13, 79.96) * mm, "end": v(94.13, 86.03) * mm});
            skLineSegment(sketch, "E1172", {"start": v(94.13, 86.03) * mm, "end": v(91.1, 86.03) * mm});
            skLineSegment(sketch, "E1173", {"start": v(91.1, 86.03) * mm, "end": v(91.1, 92.1) * mm});
            skLineSegment(sketch, "E1174", {"start": v(91.1, 92.1) * mm, "end": v(94.13, 92.1) * mm});
            skLineSegment(sketch, "E1175", {"start": v(94.13, 92.1) * mm, "end": v(94.13, 98.18) * mm});
            skLineSegment(sketch, "E1176", {"start": v(94.13, 98.18) * mm, "end": v(91.1, 98.18) * mm});
            skLineSegment(sketch, "E1177", {"start": v(91.1, 98.18) * mm, "end": v(91.1, 104.25) * mm});
            skLineSegment(sketch, "E1178", {"start": v(91.1, 104.25) * mm, "end": v(94.13, 104.25) * mm});
            skLineSegment(sketch, "E1179", {"start": v(94.13, 104.25) * mm, "end": v(94.13, 110.32) * mm});
            skLineSegment(sketch, "E1180", {"start": v(94.13, 110.32) * mm, "end": v(91.1, 110.32) * mm});
            skLineSegment(sketch, "E1181", {"start": v(91.1, 110.32) * mm, "end": v(91.1, 116.4) * mm});
            skLineSegment(sketch, "E1182", {"start": v(91.1, 116.4) * mm, "end": v(94.13, 116.4) * mm});
            skLineSegment(sketch, "E1183", {"start": v(94.13, 116.4) * mm, "end": v(94.13, 122.47) * mm});
            skLineSegment(sketch, "E1184", {"start": v(94.13, 122.47) * mm, "end": v(91.1, 122.47) * mm});
            skLineSegment(sketch, "E1185", {"start": v(91.1, 122.47) * mm, "end": v(91.1, 128.54) * mm});
            skLineSegment(sketch, "E1186", {"start": v(91.1, 128.54) * mm, "end": v(94.13, 128.54) * mm});
            skLineSegment(sketch, "E1187", {"start": v(94.13, 128.54) * mm, "end": v(94.13, 134.62) * mm});
            skLineSegment(sketch, "E1188", {"start": v(94.13, 134.62) * mm, "end": v(91.1, 134.62) * mm});
            skLineSegment(sketch, "E1189", {"start": v(91.1, 134.62) * mm, "end": v(91.1, 140.69) * mm});
            skLineSegment(sketch, "E1190", {"start": v(91.1, 140.69) * mm, "end": v(94.13, 140.69) * mm});
            skLineSegment(sketch, "E1191", {"start": v(94.13, 140.69) * mm, "end": v(94.13, 146.76) * mm});
            skLineSegment(sketch, "E1192", {"start": v(94.13, 146.76) * mm, "end": v(91.1, 146.76) * mm});
            skLineSegment(sketch, "E1193", {"start": v(91.1, 146.76) * mm, "end": v(91.1, 152.83) * mm});
            skLineSegment(sketch, "E1194", {"start": v(91.1, 152.83) * mm, "end": v(94.13, 152.83) * mm});
            skLineSegment(sketch, "E1195", {"start": v(94.13, 152.83) * mm, "end": v(94.13, 158.9) * mm});
            skLineSegment(sketch, "E1196", {"start": v(94.13, 158.9) * mm, "end": v(91.1, 158.9) * mm});
            skLineSegment(sketch, "E1197", {"start": v(91.1, 158.9) * mm, "end": v(91.1, 164.98) * mm});
            skLineSegment(sketch, "E1198", {"start": v(91.1, 164.98) * mm, "end": v(94.13, 164.98) * mm});
            skLineSegment(sketch, "E1199", {"start": v(94.13, 164.98) * mm, "end": v(94.13, 171.06) * mm});
            skLineSegment(sketch, "E1200", {"start": v(94.13, 171.06) * mm, "end": v(91.1, 171.06) * mm});
            skLineSegment(sketch, "E1201", {"start": v(91.1, 171.06) * mm, "end": v(91.1, 177.13) * mm});
            skLineSegment(sketch, "E1202", {"start": v(91.1, 177.13) * mm, "end": v(94.13, 177.13) * mm});
            skLineSegment(sketch, "E1203", {"start": v(94.13, 177.13) * mm, "end": v(94.13, 183.2) * mm});
            skLineSegment(sketch, "E1204", {"start": v(94.13, 183.2) * mm, "end": v(91.1, 183.2) * mm});
            skLineSegment(sketch, "E1205", {"start": v(91.1, 183.2) * mm, "end": v(91.1, 189.27) * mm});
            skLineSegment(sketch, "E1206", {"start": v(91.1, 189.27) * mm, "end": v(94.13, 189.27) * mm});
            skLineSegment(sketch, "E1207", {"start": v(94.13, 189.27) * mm, "end": v(94.13, 195.34) * mm});
            skLineSegment(sketch, "E1208", {"start": v(94.13, 195.34) * mm, "end": v(91.1, 195.34) * mm});
            skLineSegment(sketch, "E1209", {"start": v(91.1, 195.34) * mm, "end": v(91.1, 201.42) * mm});
            skLineSegment(sketch, "E1210", {"start": v(91.1, 201.42) * mm, "end": v(94.13, 201.42) * mm});
            skLineSegment(sketch, "E1211", {"start": v(94.13, 201.42) * mm, "end": v(94.13, 207.49) * mm});
            skLineSegment(sketch, "E1212", {"start": v(94.13, 207.49) * mm, "end": v(91.1, 207.49) * mm});
            skLineSegment(sketch, "E1213", {"start": v(91.1, 207.49) * mm, "end": v(91.1, 213.56) * mm});
            skLineSegment(sketch, "E1214", {"start": v(91.1, 213.56) * mm, "end": v(94.13, 213.56) * mm});
            skLineSegment(sketch, "E1215", {"start": v(94.13, 213.56) * mm, "end": v(94.13, 219.64) * mm});
            skLineSegment(sketch, "E1216", {"start": v(94.13, 219.64) * mm, "end": v(91.1, 219.64) * mm});
            skLineSegment(sketch, "E1217", {"start": v(91.1, 219.64) * mm, "end": v(91.1, 225.7) * mm});
            skLineSegment(sketch, "E1218", {"start": v(91.1, 225.7) * mm, "end": v(94.13, 225.7) * mm});
            skLineSegment(sketch, "E1219", {"start": v(94.13, 225.7) * mm, "end": v(94.13, 231.78) * mm});
            skLineSegment(sketch, "E1220", {"start": v(94.13, 231.78) * mm, "end": v(91.1, 231.78) * mm});
            skLineSegment(sketch, "E1221", {"start": v(91.1, 231.78) * mm, "end": v(91.1, 237.85) * mm});
            skLineSegment(sketch, "E1222", {"start": v(91.1, 237.85) * mm, "end": v(94.13, 237.85) * mm});
            skLineSegment(sketch, "E1223", {"start": v(94.13, 237.85) * mm, "end": v(94.13, 243.93) * mm});
            skLineSegment(sketch, "E1224", {"start": v(94.13, 243.93) * mm, "end": v(91.1, 243.93) * mm});
            skLineSegment(sketch, "E1225", {"start": v(91.1, 243.93) * mm, "end": v(91.1, 250) * mm});
            skLineSegment(sketch, "E1226", {"start": v(91.1, 250) * mm, "end": v(94.13, 250) * mm});
            skLineSegment(sketch, "E1227", {"start": v(94.13, 250) * mm, "end": v(94.13, 256.07) * mm});
            skLineSegment(sketch, "E1228", {"start": v(94.13, 256.07) * mm, "end": v(91.1, 256.07) * mm});
            skLineSegment(sketch, "E1229", {"start": v(91.1, 256.07) * mm, "end": v(91.1, 262.15) * mm});
            skLineSegment(sketch, "E1230", {"start": v(91.1, 262.15) * mm, "end": v(94.13, 262.15) * mm});
            skLineSegment(sketch, "E1231", {"start": v(94.13, 262.15) * mm, "end": v(94.13, 268.22) * mm});
            skLineSegment(sketch, "E1232", {"start": v(94.13, 268.22) * mm, "end": v(91.1, 268.22) * mm});
            skLineSegment(sketch, "E1233", {"start": v(91.1, 268.22) * mm, "end": v(91.1, 274.3) * mm});
            skLineSegment(sketch, "E1234", {"start": v(91.1, 274.3) * mm, "end": v(94.13, 274.3) * mm});
            skLineSegment(sketch, "E1235", {"start": v(94.13, 274.3) * mm, "end": v(94.13, 280.37) * mm});
            skLineSegment(sketch, "E1236", {"start": v(94.13, 280.37) * mm, "end": v(91.1, 280.37) * mm});
            skLineSegment(sketch, "E1237", {"start": v(91.1, 280.37) * mm, "end": v(91.1, 286.44) * mm});
            skLineSegment(sketch, "E1238", {"start": v(91.1, 286.44) * mm, "end": v(94.13, 286.44) * mm});
            skLineSegment(sketch, "E1239", {"start": v(94.13, 286.44) * mm, "end": v(94.13, 292.51) * mm});
            skLineSegment(sketch, "E1240", {"start": v(94.13, 292.51) * mm, "end": v(91.1, 292.51) * mm});
            skLineSegment(sketch, "E1241", {"start": v(91.1, 292.51) * mm, "end": v(91.1, 298.58) * mm});
            skLineSegment(sketch, "E1242", {"start": v(91.1, 298.58) * mm, "end": v(94.13, 298.58) * mm});
            skLineSegment(sketch, "E1243", {"start": v(94.13, 298.58) * mm, "end": v(94.13, 304.66) * mm});
            skLineSegment(sketch, "E1244", {"start": v(94.13, 304.66) * mm, "end": v(91.1, 304.66) * mm});
            skLineSegment(sketch, "E1245", {"start": v(91.1, 304.66) * mm, "end": v(91.1, 310.73) * mm});
            skLineSegment(sketch, "E1246", {"start": v(91.1, 310.73) * mm, "end": v(94.13, 310.73) * mm});
            skLineSegment(sketch, "E1247", {"start": v(94.13, 310.73) * mm, "end": v(94.13, 316.8) * mm});
            skLineSegment(sketch, "E1248", {"start": v(94.13, 316.8) * mm, "end": v(91.1, 316.8) * mm});
            skLineSegment(sketch, "E1249", {"start": v(91.1, 316.8) * mm, "end": v(91.1, 322.87) * mm});
            skLineSegment(sketch, "E1250", {"start": v(91.1, 322.87) * mm, "end": v(94.13, 322.87) * mm});
            skLineSegment(sketch, "E1251", {"start": v(94.13, 322.87) * mm, "end": v(94.13, 328.95) * mm});
            skLineSegment(sketch, "E1252", {"start": v(94.13, 328.95) * mm, "end": v(91.1, 328.95) * mm});
            skLineSegment(sketch, "E1253", {"start": v(91.1, 328.95) * mm, "end": v(91.1, 335.02) * mm});
            skLineSegment(sketch, "E1254", {"start": v(91.1, 335.02) * mm, "end": v(94.13, 335.02) * mm});
            skLineSegment(sketch, "E1255", {"start": v(94.13, 335.02) * mm, "end": v(94.13, 341.1) * mm});
            skLineSegment(sketch, "E1256", {"start": v(94.13, 341.1) * mm, "end": v(91.1, 341.1) * mm});
            skLineSegment(sketch, "E1257", {"start": v(91.1, 341.1) * mm, "end": v(91.1, 347.16) * mm});
            skLineSegment(sketch, "E1258", {"start": v(91.1, 347.16) * mm, "end": v(94.13, 347.16) * mm});
            skLineSegment(sketch, "E1259", {"start": v(94.13, 347.16) * mm, "end": v(94.13, 353.24) * mm});
            skLineSegment(sketch, "E1260", {"start": v(94.13, 353.24) * mm, "end": v(91.1, 353.24) * mm});
            skLineSegment(sketch, "E1261", {"start": v(91.1, 353.24) * mm, "end": v(91.1, 359.31) * mm});
            skLineSegment(sketch, "E1262", {"start": v(91.1, 359.31) * mm, "end": v(94.13, 359.31) * mm});
            skLineSegment(sketch, "E1263", {"start": v(94.13, 359.31) * mm, "end": v(94.13, 365.39) * mm});
            skLineSegment(sketch, "E1264", {"start": v(94.13, 365.39) * mm, "end": v(91.1, 365.39) * mm});
            skLineSegment(sketch, "E1265", {"start": v(91.1, 365.39) * mm, "end": v(91.1, 371.46) * mm});
            skLineSegment(sketch, "E1266", {"start": v(91.1, 371.46) * mm, "end": v(94.13, 371.46) * mm});
            skLineSegment(sketch, "E1267", {"start": v(94.13, 371.46) * mm, "end": v(94.13, 377.53) * mm});
            skLineSegment(sketch, "E1268", {"start": v(94.13, 377.53) * mm, "end": v(91.1, 377.53) * mm});
            skLineSegment(sketch, "E1269", {"start": v(91.1, 377.53) * mm, "end": v(91.1, 383.6) * mm});
            skLineSegment(sketch, "E1270", {"start": v(91.1, 383.6) * mm, "end": v(94.13, 383.6) * mm});
            skLineSegment(sketch, "E1271", {"start": v(94.13, 383.6) * mm, "end": v(94.13, 389.68) * mm});
            skLineSegment(sketch, "E1272", {"start": v(94.13, 389.68) * mm, "end": v(91.1, 389.68) * mm});
            skLineSegment(sketch, "E1273", {"start": v(91.1, 389.68) * mm, "end": v(91.1, 395.75) * mm});
            skLineSegment(sketch, "E1274", {"start": v(91.1, 395.75) * mm, "end": v(94.13, 395.75) * mm});
            skLineSegment(sketch, "E1275", {"start": v(94.13, 395.75) * mm, "end": v(94.13, 401.82) * mm});
            skLineSegment(sketch, "E1276", {"start": v(94.13, 401.82) * mm, "end": v(91.1, 401.82) * mm});
            skLineSegment(sketch, "E1277", {"start": v(91.1, 401.82) * mm, "end": v(91.1, 407.9) * mm});
            skLineSegment(sketch, "E1278", {"start": v(91.1, 407.9) * mm, "end": v(94.13, 407.9) * mm});
            skLineSegment(sketch, "E1279", {"start": v(94.13, 407.9) * mm, "end": v(94.13, 413.97) * mm});
            skLineSegment(sketch, "E1280", {"start": v(94.13, 413.97) * mm, "end": v(91.1, 413.97) * mm});
            skLineSegment(sketch, "E1281", {"start": v(91.1, 413.97) * mm, "end": v(91.1, 420.04) * mm});
            skLineSegment(sketch, "E1282", {"start": v(91.1, 420.04) * mm, "end": v(94.13, 420.04) * mm});
            skLineSegment(sketch, "E1283", {"start": v(94.13, 420.04) * mm, "end": v(94.13, 426.11) * mm});
            skLineSegment(sketch, "E1284", {"start": v(94.13, 426.11) * mm, "end": v(91.1, 426.11) * mm});
            skLineSegment(sketch, "E1285", {"start": v(91.1, 426.11) * mm, "end": v(91.1, 432.18) * mm});
            skLineSegment(sketch, "E1286", {"start": v(91.1, 432.18) * mm, "end": v(94.13, 432.18) * mm});
            skLineSegment(sketch, "E1287", {"start": v(94.13, 432.18) * mm, "end": v(94.13, 438.26) * mm});
            skLineSegment(sketch, "E1288", {"start": v(94.13, 438.26) * mm, "end": v(91.1, 438.26) * mm});
            skLineSegment(sketch, "E1289", {"start": v(91.1, 438.26) * mm, "end": v(91.1, 444.33) * mm});
            skLineSegment(sketch, "E1290", {"start": v(91.1, 444.33) * mm, "end": v(94.13, 444.33) * mm});
            skLineSegment(sketch, "E1291", {"start": v(94.13, 444.33) * mm, "end": v(94.13, 450.4) * mm});
            skLineSegment(sketch, "E1292", {"start": v(94.13, 450.4) * mm, "end": v(91.1, 450.4) * mm});
            skLineSegment(sketch, "E1293", {"start": v(91.1, 450.4) * mm, "end": v(91.1, 456.48) * mm});
            skLineSegment(sketch, "E1294", {"start": v(91.1, 456.48) * mm, "end": v(94.13, 456.48) * mm});
            skLineSegment(sketch, "E1295", {"start": v(94.13, 456.48) * mm, "end": v(94.13, 462.55) * mm});
            skLineSegment(sketch, "E1296", {"start": v(94.13, 462.55) * mm, "end": v(91.1, 462.55) * mm});
            skLineSegment(sketch, "E1297", {"start": v(91.1, 462.55) * mm, "end": v(91.1, 468.62) * mm});
            skLineSegment(sketch, "E1298", {"start": v(91.1, 468.62) * mm, "end": v(94.13, 468.62) * mm});
            skLineSegment(sketch, "E1299", {"start": v(94.13, 468.62) * mm, "end": v(94.13, 474.7) * mm});
            skLineSegment(sketch, "E1300", {"start": v(94.13, 474.7) * mm, "end": v(91.1, 474.7) * mm});
            skLineSegment(sketch, "E1301", {"start": v(91.1, 474.7) * mm, "end": v(91.1, 480.77) * mm});
            skLineSegment(sketch, "E1302", {"start": v(91.1, 480.77) * mm, "end": v(94.13, 480.77) * mm});
            skLineSegment(sketch, "E1303", {"start": v(94.13, 480.77) * mm, "end": v(94.13, 486.84) * mm});
            skLineSegment(sketch, "E1304", {"start": v(94.13, 486.84) * mm, "end": v(91.1, 486.84) * mm});
            skLineSegment(sketch, "E1305", {"start": v(91.1, 486.84) * mm, "end": v(91.1, 496.46) * mm});
            skLineSegment(sketch, "E1306", {"start": v(91.1, 496.46) * mm, "end": v(94.13, 496.46) * mm});
            skLineSegment(sketch, "E1307", {"start": v(94.13, 496.46) * mm, "end": v(94.13, 506.07) * mm});
            skLineSegment(sketch, "E1308", {"start": v(94.13, 0) * mm, "end": v(98.68, 0) * mm});
            skLineSegment(sketch, "E1309", {"start": v(98.68, 0) * mm, "end": v(98.68, -3.04) * mm});
            skLineSegment(sketch, "E1310", {"start": v(98.68, -3.04) * mm, "end": v(106.28, -3.04) * mm});
            skLineSegment(sketch, "E1311", {"start": v(106.28, -3.04) * mm, "end": v(106.28, 0) * mm});
            skLineSegment(sketch, "E1312", {"start": v(106.28, 0) * mm, "end": v(112.35, 0) * mm});
            skLineSegment(sketch, "E1313", {"start": v(112.35, 0) * mm, "end": v(112.35, -3.04) * mm});
            skLineSegment(sketch, "E1314", {"start": v(112.35, -3.04) * mm, "end": v(118.42, -3.04) * mm});
            skLineSegment(sketch, "E1315", {"start": v(118.42, -3.04) * mm, "end": v(118.42, 0) * mm});
            skLineSegment(sketch, "E1316", {"start": v(118.42, 0) * mm, "end": v(124.5, 0) * mm});
            skLineSegment(sketch, "E1317", {"start": v(124.5, 0) * mm, "end": v(124.5, -3.04) * mm});
            skLineSegment(sketch, "E1318", {"start": v(124.5, -3.04) * mm, "end": v(130.56, -3.04) * mm});
            skLineSegment(sketch, "E1319", {"start": v(130.56, -3.04) * mm, "end": v(130.56, 0) * mm});
            skLineSegment(sketch, "E1320", {"start": v(130.56, 0) * mm, "end": v(136.64, 0) * mm});
            skLineSegment(sketch, "E1321", {"start": v(136.64, 0) * mm, "end": v(136.64, -3.04) * mm});
            skLineSegment(sketch, "E1322", {"start": v(136.64, -3.04) * mm, "end": v(142.71, -3.04) * mm});
            skLineSegment(sketch, "E1323", {"start": v(142.71, -3.04) * mm, "end": v(142.71, 0) * mm});
            skLineSegment(sketch, "E1324", {"start": v(142.71, 0) * mm, "end": v(148.79, 0) * mm});
            skLineSegment(sketch, "E1325", {"start": v(148.79, 0) * mm, "end": v(148.79, -3.04) * mm});
            skLineSegment(sketch, "E1326", {"start": v(148.79, -3.04) * mm, "end": v(154.86, -3.04) * mm});
            skLineSegment(sketch, "E1327", {"start": v(154.86, -3.04) * mm, "end": v(154.86, 0) * mm});
            skLineSegment(sketch, "E1328", {"start": v(154.86, 0) * mm, "end": v(160.93, 0) * mm});
            skLineSegment(sketch, "E1329", {"start": v(160.93, 0) * mm, "end": v(160.93, -3.04) * mm});
            skLineSegment(sketch, "E1330", {"start": v(160.93, -3.04) * mm, "end": v(167, -3.04) * mm});
            skLineSegment(sketch, "E1331", {"start": v(167, -3.04) * mm, "end": v(167, 0) * mm});
            skLineSegment(sketch, "E1332", {"start": v(167, 0) * mm, "end": v(173.08, 0) * mm});
            skLineSegment(sketch, "E1333", {"start": v(173.08, 0) * mm, "end": v(173.08, -3.04) * mm});
            skLineSegment(sketch, "E1334", {"start": v(173.08, -3.04) * mm, "end": v(179.15, -3.04) * mm});
            skLineSegment(sketch, "E1335", {"start": v(179.15, -3.04) * mm, "end": v(179.15, 0) * mm});
            skLineSegment(sketch, "E1336", {"start": v(179.15, 0) * mm, "end": v(185.22, 0) * mm});
            skLineSegment(sketch, "E1337", {"start": v(185.22, 0) * mm, "end": v(185.22, -3.04) * mm});
            skLineSegment(sketch, "E1338", {"start": v(185.22, -3.04) * mm, "end": v(191.3, -3.04) * mm});
            skLineSegment(sketch, "E1339", {"start": v(191.3, -3.04) * mm, "end": v(191.3, 0) * mm});
            skLineSegment(sketch, "E1340", {"start": v(191.3, 0) * mm, "end": v(197.37, 0) * mm});
            skLineSegment(sketch, "E1341", {"start": v(197.37, 0) * mm, "end": v(197.37, -3.04) * mm});
            skLineSegment(sketch, "E1342", {"start": v(197.37, -3.04) * mm, "end": v(203.44, -3.04) * mm});
            skLineSegment(sketch, "E1343", {"start": v(203.44, -3.04) * mm, "end": v(203.44, 0) * mm});
            skLineSegment(sketch, "E1344", {"start": v(203.44, 0) * mm, "end": v(209.51, 0) * mm});
            skLineSegment(sketch, "E1345", {"start": v(209.51, 0) * mm, "end": v(209.51, -3.04) * mm});
            skLineSegment(sketch, "E1346", {"start": v(209.51, -3.04) * mm, "end": v(215.59, -3.04) * mm});
            skLineSegment(sketch, "E1347", {"start": v(215.59, -3.04) * mm, "end": v(215.59, 0) * mm});
            skLineSegment(sketch, "E1348", {"start": v(215.59, 0) * mm, "end": v(221.66, 0) * mm});
            skLineSegment(sketch, "E1349", {"start": v(221.66, 0) * mm, "end": v(221.66, -3.04) * mm});
            skLineSegment(sketch, "E1350", {"start": v(221.66, -3.04) * mm, "end": v(227.73, -3.04) * mm});
            skLineSegment(sketch, "E1351", {"start": v(227.73, -3.04) * mm, "end": v(227.73, 0) * mm});
            skLineSegment(sketch, "E1352", {"start": v(227.73, 0) * mm, "end": v(233.8, 0) * mm});
            skLineSegment(sketch, "E1353", {"start": v(233.8, 0) * mm, "end": v(233.8, -3.04) * mm});
            skLineSegment(sketch, "E1354", {"start": v(233.8, -3.04) * mm, "end": v(239.88, -3.04) * mm});
            skLineSegment(sketch, "E1355", {"start": v(239.88, -3.04) * mm, "end": v(239.88, 0) * mm});
            skLineSegment(sketch, "E1356", {"start": v(239.88, 0) * mm, "end": v(245.95, 0) * mm});
            skLineSegment(sketch, "E1357", {"start": v(245.95, 0) * mm, "end": v(245.95, -3.04) * mm});
            skLineSegment(sketch, "E1358", {"start": v(245.95, -3.04) * mm, "end": v(252.02, -3.04) * mm});
            skLineSegment(sketch, "E1359", {"start": v(252.02, -3.04) * mm, "end": v(252.02, 0) * mm});
            skLineSegment(sketch, "E1360", {"start": v(252.02, 0) * mm, "end": v(258.1, 0) * mm});
            skLineSegment(sketch, "E1361", {"start": v(258.1, 0) * mm, "end": v(258.1, -3.04) * mm});
            skLineSegment(sketch, "E1362", {"start": v(258.1, -3.04) * mm, "end": v(265.69, -3.04) * mm});
            skLineSegment(sketch, "E1363", {"start": v(265.69, -3.04) * mm, "end": v(265.69, 0) * mm});
            skLineSegment(sketch, "E1364", {"start": v(265.69, 0) * mm, "end": v(270.24, 0) * mm});
            skLineSegment(sketch, "E1365", {"start": v(270.24, 0) * mm, "end": v(270.24, -9.62) * mm});
            skLineSegment(sketch, "E1366", {"start": v(270.24, -9.62) * mm, "end": v(273.28, -9.62) * mm});
            skLineSegment(sketch, "E1367", {"start": v(273.28, -9.62) * mm, "end": v(273.28, -19.23) * mm});
            skLineSegment(sketch, "E1368", {"start": v(273.28, -19.23) * mm, "end": v(270.24, -19.23) * mm});
            skLineSegment(sketch, "E1369", {"start": v(270.24, -19.23) * mm, "end": v(270.24, -25.3) * mm});
            skLineSegment(sketch, "E1370", {"start": v(270.24, -25.3) * mm, "end": v(273.28, -25.3) * mm});
            skLineSegment(sketch, "E1371", {"start": v(273.28, -25.3) * mm, "end": v(273.28, -31.38) * mm});
            skLineSegment(sketch, "E1372", {"start": v(273.28, -31.38) * mm, "end": v(270.24, -31.38) * mm});
            skLineSegment(sketch, "E1373", {"start": v(270.24, -31.38) * mm, "end": v(270.24, -37.45) * mm});
            skLineSegment(sketch, "E1374", {"start": v(270.24, -37.45) * mm, "end": v(273.28, -37.45) * mm});
            skLineSegment(sketch, "E1375", {"start": v(273.28, -37.45) * mm, "end": v(273.28, -43.52) * mm});
            skLineSegment(sketch, "E1376", {"start": v(273.28, -43.52) * mm, "end": v(270.24, -43.52) * mm});
            skLineSegment(sketch, "E1377", {"start": v(270.24, -43.52) * mm, "end": v(270.24, -49.6) * mm});
            skLineSegment(sketch, "E1378", {"start": v(270.24, -49.6) * mm, "end": v(273.28, -49.6) * mm});
            skLineSegment(sketch, "E1379", {"start": v(273.28, -49.6) * mm, "end": v(273.28, -55.67) * mm});
            skLineSegment(sketch, "E1380", {"start": v(273.28, -55.67) * mm, "end": v(270.24, -55.67) * mm});
            skLineSegment(sketch, "E1381", {"start": v(270.24, -55.67) * mm, "end": v(270.24, -61.74) * mm});
            skLineSegment(sketch, "E1382", {"start": v(270.24, -61.74) * mm, "end": v(273.28, -61.74) * mm});
            skLineSegment(sketch, "E1383", {"start": v(273.28, -61.74) * mm, "end": v(273.28, -67.81) * mm});
            skLineSegment(sketch, "E1384", {"start": v(273.28, -67.81) * mm, "end": v(270.24, -67.81) * mm});
            skLineSegment(sketch, "E1385", {"start": v(270.24, -67.81) * mm, "end": v(270.24, -73.89) * mm});
            skLineSegment(sketch, "E1386", {"start": v(270.24, -73.89) * mm, "end": v(273.28, -73.89) * mm});
            skLineSegment(sketch, "E1387", {"start": v(273.28, -73.89) * mm, "end": v(273.28, -79.96) * mm});
            skLineSegment(sketch, "E1388", {"start": v(273.28, -79.96) * mm, "end": v(270.24, -79.96) * mm});
            skLineSegment(sketch, "E1389", {"start": v(270.24, -79.96) * mm, "end": v(270.24, -86.03) * mm});
            skLineSegment(sketch, "E1390", {"start": v(270.24, -86.03) * mm, "end": v(273.28, -86.03) * mm});
            skLineSegment(sketch, "E1391", {"start": v(273.28, -86.03) * mm, "end": v(273.28, -92.1) * mm});
            skLineSegment(sketch, "E1392", {"start": v(273.28, -92.1) * mm, "end": v(270.24, -92.1) * mm});
            skLineSegment(sketch, "E1393", {"start": v(270.24, -92.1) * mm, "end": v(270.24, -98.18) * mm});
            skLineSegment(sketch, "E1394", {"start": v(270.24, -98.18) * mm, "end": v(273.28, -98.18) * mm});
            skLineSegment(sketch, "E1395", {"start": v(273.28, -98.18) * mm, "end": v(273.28, -104.25) * mm});
            skLineSegment(sketch, "E1396", {"start": v(273.28, -104.25) * mm, "end": v(270.24, -104.25) * mm});
            skLineSegment(sketch, "E1397", {"start": v(270.24, -104.25) * mm, "end": v(270.24, -110.32) * mm});
            skLineSegment(sketch, "E1398", {"start": v(270.24, -110.32) * mm, "end": v(273.28, -110.32) * mm});
            skLineSegment(sketch, "E1399", {"start": v(273.28, -110.32) * mm, "end": v(273.28, -116.4) * mm});
            skLineSegment(sketch, "E1400", {"start": v(273.28, -116.4) * mm, "end": v(270.24, -116.4) * mm});
            skLineSegment(sketch, "E1401", {"start": v(270.24, -116.4) * mm, "end": v(270.24, -122.47) * mm});
            skLineSegment(sketch, "E1402", {"start": v(270.24, -122.47) * mm, "end": v(273.28, -122.47) * mm});
            skLineSegment(sketch, "E1403", {"start": v(273.28, -122.47) * mm, "end": v(273.28, -128.54) * mm});
            skLineSegment(sketch, "E1404", {"start": v(273.28, -128.54) * mm, "end": v(270.24, -128.54) * mm});
            skLineSegment(sketch, "E1405", {"start": v(270.24, -128.54) * mm, "end": v(270.24, -134.62) * mm});
            skLineSegment(sketch, "E1406", {"start": v(270.24, -134.62) * mm, "end": v(273.28, -134.62) * mm});
            skLineSegment(sketch, "E1407", {"start": v(273.28, -134.62) * mm, "end": v(273.28, -140.69) * mm});
            skLineSegment(sketch, "E1408", {"start": v(273.28, -140.69) * mm, "end": v(270.24, -140.69) * mm});
            skLineSegment(sketch, "E1409", {"start": v(270.24, -140.69) * mm, "end": v(270.24, -146.76) * mm});
            skLineSegment(sketch, "E1410", {"start": v(270.24, -146.76) * mm, "end": v(273.28, -146.76) * mm});
            skLineSegment(sketch, "E1411", {"start": v(273.28, -146.76) * mm, "end": v(273.28, -152.83) * mm});
            skLineSegment(sketch, "E1412", {"start": v(273.28, -152.83) * mm, "end": v(270.24, -152.83) * mm});
            skLineSegment(sketch, "E1413", {"start": v(270.24, -152.83) * mm, "end": v(270.24, -158.9) * mm});
            skLineSegment(sketch, "E1414", {"start": v(270.24, -158.9) * mm, "end": v(273.28, -158.9) * mm});
            skLineSegment(sketch, "E1415", {"start": v(273.28, -158.9) * mm, "end": v(273.28, -164.98) * mm});
            skLineSegment(sketch, "E1416", {"start": v(273.28, -164.98) * mm, "end": v(270.24, -164.98) * mm});
            skLineSegment(sketch, "E1417", {"start": v(270.24, -164.98) * mm, "end": v(270.24, -171.05) * mm});
            skLineSegment(sketch, "E1418", {"start": v(270.24, -171.05) * mm, "end": v(273.28, -171.05) * mm});
            skLineSegment(sketch, "E1419", {"start": v(273.28, -171.05) * mm, "end": v(273.28, -177.13) * mm});
            skLineSegment(sketch, "E1420", {"start": v(273.28, -177.13) * mm, "end": v(270.24, -177.13) * mm});
            skLineSegment(sketch, "E1421", {"start": v(270.24, -177.13) * mm, "end": v(270.24, -183.2) * mm});
            skLineSegment(sketch, "E1422", {"start": v(270.24, -183.2) * mm, "end": v(273.28, -183.2) * mm});
            skLineSegment(sketch, "E1423", {"start": v(273.28, -183.2) * mm, "end": v(273.28, -189.27) * mm});
            skLineSegment(sketch, "E1424", {"start": v(273.28, -189.27) * mm, "end": v(270.24, -189.27) * mm});
            skLineSegment(sketch, "E1425", {"start": v(270.24, -189.27) * mm, "end": v(270.24, -195.35) * mm});
            skLineSegment(sketch, "E1426", {"start": v(270.24, -195.35) * mm, "end": v(273.28, -195.35) * mm});
            skLineSegment(sketch, "E1427", {"start": v(273.28, -195.35) * mm, "end": v(273.28, -201.42) * mm});
            skLineSegment(sketch, "E1428", {"start": v(273.28, -201.42) * mm, "end": v(270.24, -201.42) * mm});
            skLineSegment(sketch, "E1429", {"start": v(270.24, -201.42) * mm, "end": v(270.24, -207.49) * mm});
            skLineSegment(sketch, "E1430", {"start": v(270.24, -207.49) * mm, "end": v(273.28, -207.49) * mm});
            skLineSegment(sketch, "E1431", {"start": v(273.28, -207.49) * mm, "end": v(273.28, -213.56) * mm});
            skLineSegment(sketch, "E1432", {"start": v(273.28, -213.56) * mm, "end": v(270.24, -213.56) * mm});
            skLineSegment(sketch, "E1433", {"start": v(270.24, -213.56) * mm, "end": v(270.24, -219.64) * mm});
            skLineSegment(sketch, "E1434", {"start": v(270.24, -219.64) * mm, "end": v(273.28, -219.64) * mm});
            skLineSegment(sketch, "E1435", {"start": v(273.28, -219.64) * mm, "end": v(273.28, -225.7) * mm});
            skLineSegment(sketch, "E1436", {"start": v(273.28, -225.7) * mm, "end": v(270.24, -225.7) * mm});
            skLineSegment(sketch, "E1437", {"start": v(270.24, -225.7) * mm, "end": v(270.24, -231.78) * mm});
            skLineSegment(sketch, "E1438", {"start": v(270.24, -231.78) * mm, "end": v(273.28, -231.78) * mm});
            skLineSegment(sketch, "E1439", {"start": v(273.28, -231.78) * mm, "end": v(273.28, -237.85) * mm});
            skLineSegment(sketch, "E1440", {"start": v(273.28, -237.85) * mm, "end": v(270.24, -237.85) * mm});
            skLineSegment(sketch, "E1441", {"start": v(270.24, -237.85) * mm, "end": v(270.24, -243.93) * mm});
            skLineSegment(sketch, "E1442", {"start": v(270.24, -243.93) * mm, "end": v(273.28, -243.93) * mm});
            skLineSegment(sketch, "E1443", {"start": v(273.28, -243.93) * mm, "end": v(273.28, -250) * mm});
            skLineSegment(sketch, "E1444", {"start": v(273.28, -250) * mm, "end": v(270.24, -250) * mm});
            skLineSegment(sketch, "E1445", {"start": v(270.24, -250) * mm, "end": v(270.24, -256.07) * mm});
            skLineSegment(sketch, "E1446", {"start": v(270.24, -256.07) * mm, "end": v(273.28, -256.07) * mm});
            skLineSegment(sketch, "E1447", {"start": v(273.28, -256.07) * mm, "end": v(273.28, -262.15) * mm});
            skLineSegment(sketch, "E1448", {"start": v(273.28, -262.15) * mm, "end": v(270.24, -262.15) * mm});
            skLineSegment(sketch, "E1449", {"start": v(270.24, -262.15) * mm, "end": v(270.24, -268.22) * mm});
            skLineSegment(sketch, "E1450", {"start": v(270.24, -268.22) * mm, "end": v(273.28, -268.22) * mm});
            skLineSegment(sketch, "E1451", {"start": v(273.28, -268.22) * mm, "end": v(273.28, -274.3) * mm});
            skLineSegment(sketch, "E1452", {"start": v(273.28, -274.3) * mm, "end": v(270.24, -274.3) * mm});
            skLineSegment(sketch, "E1453", {"start": v(270.24, -274.3) * mm, "end": v(270.24, -280.36) * mm});
            skLineSegment(sketch, "E1454", {"start": v(270.24, -280.36) * mm, "end": v(273.28, -280.36) * mm});
            skLineSegment(sketch, "E1455", {"start": v(273.28, -280.36) * mm, "end": v(273.28, -286.44) * mm});
            skLineSegment(sketch, "E1456", {"start": v(273.28, -286.44) * mm, "end": v(270.24, -286.44) * mm});
            skLineSegment(sketch, "E1457", {"start": v(270.24, -286.44) * mm, "end": v(270.24, -292.51) * mm});
            skLineSegment(sketch, "E1458", {"start": v(270.24, -292.51) * mm, "end": v(273.28, -292.51) * mm});
            skLineSegment(sketch, "E1459", {"start": v(273.28, -292.51) * mm, "end": v(273.28, -298.58) * mm});
            skLineSegment(sketch, "E1460", {"start": v(273.28, -298.58) * mm, "end": v(270.24, -298.58) * mm});
            skLineSegment(sketch, "E1461", {"start": v(270.24, -298.58) * mm, "end": v(270.24, -304.66) * mm});
            skLineSegment(sketch, "E1462", {"start": v(270.24, -304.66) * mm, "end": v(273.28, -304.66) * mm});
            skLineSegment(sketch, "E1463", {"start": v(273.28, -304.66) * mm, "end": v(273.28, -310.73) * mm});
            skLineSegment(sketch, "E1464", {"start": v(273.28, -310.73) * mm, "end": v(270.24, -310.73) * mm});
            skLineSegment(sketch, "E1465", {"start": v(270.24, -310.73) * mm, "end": v(270.24, -316.8) * mm});
            skLineSegment(sketch, "E1466", {"start": v(270.24, -316.8) * mm, "end": v(273.28, -316.8) * mm});
            skLineSegment(sketch, "E1467", {"start": v(273.28, -316.8) * mm, "end": v(273.28, -322.88) * mm});
            skLineSegment(sketch, "E1468", {"start": v(273.28, -322.88) * mm, "end": v(270.24, -322.88) * mm});
            skLineSegment(sketch, "E1469", {"start": v(270.24, -322.88) * mm, "end": v(270.24, -328.95) * mm});
            skLineSegment(sketch, "E1470", {"start": v(270.24, -328.95) * mm, "end": v(273.28, -328.95) * mm});
            skLineSegment(sketch, "E1471", {"start": v(273.28, -328.95) * mm, "end": v(273.28, -335.02) * mm});
            skLineSegment(sketch, "E1472", {"start": v(273.28, -335.02) * mm, "end": v(270.24, -335.02) * mm});
            skLineSegment(sketch, "E1473", {"start": v(270.24, -335.02) * mm, "end": v(270.24, -341.1) * mm});
            skLineSegment(sketch, "E1474", {"start": v(270.24, -341.1) * mm, "end": v(273.28, -341.1) * mm});
            skLineSegment(sketch, "E1475", {"start": v(273.28, -341.1) * mm, "end": v(273.28, -347.17) * mm});
            skLineSegment(sketch, "E1476", {"start": v(273.28, -347.17) * mm, "end": v(270.24, -347.17) * mm});
            skLineSegment(sketch, "E1477", {"start": v(270.24, -347.17) * mm, "end": v(270.24, -353.24) * mm});
            skLineSegment(sketch, "E1478", {"start": v(270.24, -353.24) * mm, "end": v(273.28, -353.24) * mm});
            skLineSegment(sketch, "E1479", {"start": v(273.28, -353.24) * mm, "end": v(273.28, -359.31) * mm});
            skLineSegment(sketch, "E1480", {"start": v(273.28, -359.31) * mm, "end": v(270.24, -359.31) * mm});
            skLineSegment(sketch, "E1481", {"start": v(270.24, -359.31) * mm, "end": v(270.24, -365.39) * mm});
            skLineSegment(sketch, "E1482", {"start": v(270.24, -365.39) * mm, "end": v(273.28, -365.39) * mm});
            skLineSegment(sketch, "E1483", {"start": v(273.28, -365.39) * mm, "end": v(273.28, -371.46) * mm});
            skLineSegment(sketch, "E1484", {"start": v(273.28, -371.46) * mm, "end": v(270.24, -371.46) * mm});
            skLineSegment(sketch, "E1485", {"start": v(270.24, -371.46) * mm, "end": v(270.24, -377.53) * mm});
            skLineSegment(sketch, "E1486", {"start": v(270.24, -377.53) * mm, "end": v(273.28, -377.53) * mm});
            skLineSegment(sketch, "E1487", {"start": v(273.28, -377.53) * mm, "end": v(273.28, -383.6) * mm});
            skLineSegment(sketch, "E1488", {"start": v(273.28, -383.6) * mm, "end": v(270.24, -383.6) * mm});
            skLineSegment(sketch, "E1489", {"start": v(270.24, -383.6) * mm, "end": v(270.24, -389.68) * mm});
            skLineSegment(sketch, "E1490", {"start": v(270.24, -389.68) * mm, "end": v(273.28, -389.68) * mm});
            skLineSegment(sketch, "E1491", {"start": v(273.28, -389.68) * mm, "end": v(273.28, -395.75) * mm});
            skLineSegment(sketch, "E1492", {"start": v(273.28, -395.75) * mm, "end": v(270.24, -395.75) * mm});
            skLineSegment(sketch, "E1493", {"start": v(270.24, -395.75) * mm, "end": v(270.24, -401.82) * mm});
            skLineSegment(sketch, "E1494", {"start": v(270.24, -401.82) * mm, "end": v(273.28, -401.82) * mm});
            skLineSegment(sketch, "E1495", {"start": v(273.28, -401.82) * mm, "end": v(273.28, -407.9) * mm});
            skLineSegment(sketch, "E1496", {"start": v(273.28, -407.9) * mm, "end": v(270.24, -407.9) * mm});
            skLineSegment(sketch, "E1497", {"start": v(270.24, -407.9) * mm, "end": v(270.24, -413.97) * mm});
            skLineSegment(sketch, "E1498", {"start": v(270.24, -413.97) * mm, "end": v(273.28, -413.97) * mm});
            skLineSegment(sketch, "E1499", {"start": v(273.28, -413.97) * mm, "end": v(273.28, -420.04) * mm});
            skLineSegment(sketch, "E1500", {"start": v(273.28, -420.04) * mm, "end": v(270.24, -420.04) * mm});
            skLineSegment(sketch, "E1501", {"start": v(270.24, -420.04) * mm, "end": v(270.24, -426.11) * mm});
            skLineSegment(sketch, "E1502", {"start": v(270.24, -426.11) * mm, "end": v(273.28, -426.11) * mm});
            skLineSegment(sketch, "E1503", {"start": v(273.28, -426.11) * mm, "end": v(273.28, -432.19) * mm});
            skLineSegment(sketch, "E1504", {"start": v(273.28, -432.19) * mm, "end": v(270.24, -432.19) * mm});
            skLineSegment(sketch, "E1505", {"start": v(270.24, -432.19) * mm, "end": v(270.24, -438.26) * mm});
            skLineSegment(sketch, "E1506", {"start": v(270.24, -438.26) * mm, "end": v(273.28, -438.26) * mm});
            skLineSegment(sketch, "E1507", {"start": v(273.28, -438.26) * mm, "end": v(273.28, -444.33) * mm});
            skLineSegment(sketch, "E1508", {"start": v(273.28, -444.33) * mm, "end": v(270.24, -444.33) * mm});
            skLineSegment(sketch, "E1509", {"start": v(270.24, -444.33) * mm, "end": v(270.24, -450.4) * mm});
            skLineSegment(sketch, "E1510", {"start": v(270.24, -450.4) * mm, "end": v(273.28, -450.4) * mm});
            skLineSegment(sketch, "E1511", {"start": v(273.28, -450.4) * mm, "end": v(273.28, -456.48) * mm});
            skLineSegment(sketch, "E1512", {"start": v(273.28, -456.48) * mm, "end": v(270.24, -456.48) * mm});
            skLineSegment(sketch, "E1513", {"start": v(270.24, -456.48) * mm, "end": v(270.24, -462.55) * mm});
            skLineSegment(sketch, "E1514", {"start": v(270.24, -462.55) * mm, "end": v(273.28, -462.55) * mm});
            skLineSegment(sketch, "E1515", {"start": v(273.28, -462.55) * mm, "end": v(273.28, -468.62) * mm});
            skLineSegment(sketch, "E1516", {"start": v(273.28, -468.62) * mm, "end": v(270.24, -468.62) * mm});
            skLineSegment(sketch, "E1517", {"start": v(270.24, -468.62) * mm, "end": v(270.24, -474.7) * mm});
            skLineSegment(sketch, "E1518", {"start": v(270.24, -474.7) * mm, "end": v(273.28, -474.7) * mm});
            skLineSegment(sketch, "E1519", {"start": v(273.28, -474.7) * mm, "end": v(273.28, -480.77) * mm});
            skLineSegment(sketch, "E1520", {"start": v(273.28, -480.77) * mm, "end": v(270.24, -480.77) * mm});
            skLineSegment(sketch, "E1521", {"start": v(270.24, -480.77) * mm, "end": v(270.24, -486.84) * mm});
            skLineSegment(sketch, "E1522", {"start": v(270.24, -486.84) * mm, "end": v(273.28, -486.84) * mm});
            skLineSegment(sketch, "E1523", {"start": v(273.28, -486.84) * mm, "end": v(273.28, -496.46) * mm});
            skLineSegment(sketch, "E1524", {"start": v(273.28, -496.46) * mm, "end": v(270.24, -496.46) * mm});
            skLineSegment(sketch, "E1525", {"start": v(270.24, -496.46) * mm, "end": v(270.24, -506.07) * mm});
            skLineSegment(sketch, "E1526", {"start": v(270.24, -506.07) * mm, "end": v(265.69, -506.07) * mm});
            skLineSegment(sketch, "E1527", {"start": v(265.69, -506.07) * mm, "end": v(265.69, -503.04) * mm});
            skLineSegment(sketch, "E1528", {"start": v(265.69, -503.04) * mm, "end": v(258.1, -503.04) * mm});
            skLineSegment(sketch, "E1529", {"start": v(258.1, -503.04) * mm, "end": v(258.1, -506.07) * mm});
            skLineSegment(sketch, "E1530", {"start": v(258.1, -506.07) * mm, "end": v(252.02, -506.07) * mm});
            skLineSegment(sketch, "E1531", {"start": v(252.02, -506.07) * mm, "end": v(252.02, -503.04) * mm});
            skLineSegment(sketch, "E1532", {"start": v(252.02, -503.04) * mm, "end": v(245.95, -503.04) * mm});
            skLineSegment(sketch, "E1533", {"start": v(245.95, -503.04) * mm, "end": v(245.95, -506.07) * mm});
            skLineSegment(sketch, "E1534", {"start": v(245.95, -506.07) * mm, "end": v(239.88, -506.07) * mm});
            skLineSegment(sketch, "E1535", {"start": v(239.88, -506.07) * mm, "end": v(239.88, -503.04) * mm});
            skLineSegment(sketch, "E1536", {"start": v(239.88, -503.04) * mm, "end": v(233.8, -503.04) * mm});
            skLineSegment(sketch, "E1537", {"start": v(233.8, -503.04) * mm, "end": v(233.8, -506.07) * mm});
            skLineSegment(sketch, "E1538", {"start": v(233.8, -506.07) * mm, "end": v(227.73, -506.07) * mm});
            skLineSegment(sketch, "E1539", {"start": v(227.73, -506.07) * mm, "end": v(227.73, -503.04) * mm});
            skLineSegment(sketch, "E1540", {"start": v(227.73, -503.04) * mm, "end": v(221.66, -503.04) * mm});
            skLineSegment(sketch, "E1541", {"start": v(221.66, -503.04) * mm, "end": v(221.66, -506.07) * mm});
            skLineSegment(sketch, "E1542", {"start": v(221.66, -506.07) * mm, "end": v(215.59, -506.07) * mm});
            skLineSegment(sketch, "E1543", {"start": v(215.59, -506.07) * mm, "end": v(215.59, -503.04) * mm});
            skLineSegment(sketch, "E1544", {"start": v(215.59, -503.04) * mm, "end": v(209.51, -503.04) * mm});
            skLineSegment(sketch, "E1545", {"start": v(209.51, -503.04) * mm, "end": v(209.51, -506.07) * mm});
            skLineSegment(sketch, "E1546", {"start": v(209.51, -506.07) * mm, "end": v(203.44, -506.07) * mm});
            skLineSegment(sketch, "E1547", {"start": v(203.44, -506.07) * mm, "end": v(203.44, -503.04) * mm});
            skLineSegment(sketch, "E1548", {"start": v(203.44, -503.04) * mm, "end": v(197.37, -503.04) * mm});
            skLineSegment(sketch, "E1549", {"start": v(197.37, -503.04) * mm, "end": v(197.37, -506.07) * mm});
            skLineSegment(sketch, "E1550", {"start": v(197.37, -506.07) * mm, "end": v(191.3, -506.07) * mm});
            skLineSegment(sketch, "E1551", {"start": v(191.3, -506.07) * mm, "end": v(191.3, -503.04) * mm});
            skLineSegment(sketch, "E1552", {"start": v(191.3, -503.04) * mm, "end": v(185.22, -503.04) * mm});
            skLineSegment(sketch, "E1553", {"start": v(185.22, -503.04) * mm, "end": v(185.22, -506.07) * mm});
            skLineSegment(sketch, "E1554", {"start": v(185.22, -506.07) * mm, "end": v(179.15, -506.07) * mm});
            skLineSegment(sketch, "E1555", {"start": v(179.15, -506.07) * mm, "end": v(179.15, -503.04) * mm});
            skLineSegment(sketch, "E1556", {"start": v(179.15, -503.04) * mm, "end": v(173.08, -503.04) * mm});
            skLineSegment(sketch, "E1557", {"start": v(173.08, -503.04) * mm, "end": v(173.08, -506.07) * mm});
            skLineSegment(sketch, "E1558", {"start": v(173.08, -506.07) * mm, "end": v(167, -506.07) * mm});
            skLineSegment(sketch, "E1559", {"start": v(167, -506.07) * mm, "end": v(167, -503.04) * mm});
            skLineSegment(sketch, "E1560", {"start": v(167, -503.04) * mm, "end": v(160.93, -503.04) * mm});
            skLineSegment(sketch, "E1561", {"start": v(160.93, -503.04) * mm, "end": v(160.93, -506.07) * mm});
            skLineSegment(sketch, "E1562", {"start": v(160.93, -506.07) * mm, "end": v(154.86, -506.07) * mm});
            skLineSegment(sketch, "E1563", {"start": v(154.86, -506.07) * mm, "end": v(154.86, -503.04) * mm});
            skLineSegment(sketch, "E1564", {"start": v(154.86, -503.04) * mm, "end": v(148.79, -503.04) * mm});
            skLineSegment(sketch, "E1565", {"start": v(148.79, -503.04) * mm, "end": v(148.79, -506.07) * mm});
            skLineSegment(sketch, "E1566", {"start": v(148.79, -506.07) * mm, "end": v(142.71, -506.07) * mm});
            skLineSegment(sketch, "E1567", {"start": v(142.71, -506.07) * mm, "end": v(142.71, -503.04) * mm});
            skLineSegment(sketch, "E1568", {"start": v(142.71, -503.04) * mm, "end": v(136.64, -503.04) * mm});
            skLineSegment(sketch, "E1569", {"start": v(136.64, -503.04) * mm, "end": v(136.64, -506.07) * mm});
            skLineSegment(sketch, "E1570", {"start": v(136.64, -506.07) * mm, "end": v(130.56, -506.07) * mm});
            skLineSegment(sketch, "E1571", {"start": v(130.56, -506.07) * mm, "end": v(130.56, -503.04) * mm});
            skLineSegment(sketch, "E1572", {"start": v(130.56, -503.04) * mm, "end": v(124.5, -503.04) * mm});
            skLineSegment(sketch, "E1573", {"start": v(124.5, -503.04) * mm, "end": v(124.5, -506.07) * mm});
            skLineSegment(sketch, "E1574", {"start": v(124.5, -506.07) * mm, "end": v(118.42, -506.07) * mm});
            skLineSegment(sketch, "E1575", {"start": v(118.42, -506.07) * mm, "end": v(118.42, -503.04) * mm});
            skLineSegment(sketch, "E1576", {"start": v(118.42, -503.04) * mm, "end": v(112.35, -503.04) * mm});
            skLineSegment(sketch, "E1577", {"start": v(112.35, -503.04) * mm, "end": v(112.35, -506.07) * mm});
            skLineSegment(sketch, "E1578", {"start": v(112.35, -506.07) * mm, "end": v(106.28, -506.07) * mm});
            skLineSegment(sketch, "E1579", {"start": v(106.28, -506.07) * mm, "end": v(106.28, -503.04) * mm});
            skLineSegment(sketch, "E1580", {"start": v(106.28, -503.04) * mm, "end": v(98.68, -503.04) * mm});
            skLineSegment(sketch, "E1581", {"start": v(98.68, -503.04) * mm, "end": v(98.68, -506.07) * mm});
            skLineSegment(sketch, "E1582", {"start": v(98.68, -506.07) * mm, "end": v(94.13, -506.07) * mm});
            skLineSegment(sketch, "E1583", {"start": v(94.13, -506.07) * mm, "end": v(94.13, -496.46) * mm});
            skLineSegment(sketch, "E1584", {"start": v(94.13, -496.46) * mm, "end": v(91.1, -496.46) * mm});
            skLineSegment(sketch, "E1585", {"start": v(91.1, -496.46) * mm, "end": v(91.1, -486.84) * mm});
            skLineSegment(sketch, "E1586", {"start": v(91.1, -486.84) * mm, "end": v(94.13, -486.84) * mm});
            skLineSegment(sketch, "E1587", {"start": v(94.13, -486.84) * mm, "end": v(94.13, -480.77) * mm});
            skLineSegment(sketch, "E1588", {"start": v(94.13, -480.77) * mm, "end": v(91.1, -480.77) * mm});
            skLineSegment(sketch, "E1589", {"start": v(91.1, -480.77) * mm, "end": v(91.1, -474.7) * mm});
            skLineSegment(sketch, "E1590", {"start": v(91.1, -474.7) * mm, "end": v(94.13, -474.7) * mm});
            skLineSegment(sketch, "E1591", {"start": v(94.13, -474.7) * mm, "end": v(94.13, -468.62) * mm});
            skLineSegment(sketch, "E1592", {"start": v(94.13, -468.62) * mm, "end": v(91.1, -468.62) * mm});
            skLineSegment(sketch, "E1593", {"start": v(91.1, -468.62) * mm, "end": v(91.1, -462.55) * mm});
            skLineSegment(sketch, "E1594", {"start": v(91.1, -462.55) * mm, "end": v(94.13, -462.55) * mm});
            skLineSegment(sketch, "E1595", {"start": v(94.13, -462.55) * mm, "end": v(94.13, -456.48) * mm});
            skLineSegment(sketch, "E1596", {"start": v(94.13, -456.48) * mm, "end": v(91.1, -456.48) * mm});
            skLineSegment(sketch, "E1597", {"start": v(91.1, -456.48) * mm, "end": v(91.1, -450.4) * mm});
            skLineSegment(sketch, "E1598", {"start": v(91.1, -450.4) * mm, "end": v(94.13, -450.4) * mm});
            skLineSegment(sketch, "E1599", {"start": v(94.13, -450.4) * mm, "end": v(94.13, -444.33) * mm});
            skLineSegment(sketch, "E1600", {"start": v(94.13, -444.33) * mm, "end": v(91.1, -444.33) * mm});
            skLineSegment(sketch, "E1601", {"start": v(91.1, -444.33) * mm, "end": v(91.1, -438.26) * mm});
            skLineSegment(sketch, "E1602", {"start": v(91.1, -438.26) * mm, "end": v(94.13, -438.26) * mm});
            skLineSegment(sketch, "E1603", {"start": v(94.13, -438.26) * mm, "end": v(94.13, -432.19) * mm});
            skLineSegment(sketch, "E1604", {"start": v(94.13, -432.19) * mm, "end": v(91.1, -432.19) * mm});
            skLineSegment(sketch, "E1605", {"start": v(91.1, -432.19) * mm, "end": v(91.1, -426.11) * mm});
            skLineSegment(sketch, "E1606", {"start": v(91.1, -426.11) * mm, "end": v(94.13, -426.11) * mm});
            skLineSegment(sketch, "E1607", {"start": v(94.13, -426.11) * mm, "end": v(94.13, -420.04) * mm});
            skLineSegment(sketch, "E1608", {"start": v(94.13, -420.04) * mm, "end": v(91.1, -420.04) * mm});
            skLineSegment(sketch, "E1609", {"start": v(91.1, -420.04) * mm, "end": v(91.1, -413.97) * mm});
            skLineSegment(sketch, "E1610", {"start": v(91.1, -413.97) * mm, "end": v(94.13, -413.97) * mm});
            skLineSegment(sketch, "E1611", {"start": v(94.13, -413.97) * mm, "end": v(94.13, -407.9) * mm});
            skLineSegment(sketch, "E1612", {"start": v(94.13, -407.9) * mm, "end": v(91.1, -407.9) * mm});
            skLineSegment(sketch, "E1613", {"start": v(91.1, -407.9) * mm, "end": v(91.1, -401.82) * mm});
            skLineSegment(sketch, "E1614", {"start": v(91.1, -401.82) * mm, "end": v(94.13, -401.82) * mm});
            skLineSegment(sketch, "E1615", {"start": v(94.13, -401.82) * mm, "end": v(94.13, -395.75) * mm});
            skLineSegment(sketch, "E1616", {"start": v(94.13, -395.75) * mm, "end": v(91.1, -395.75) * mm});
            skLineSegment(sketch, "E1617", {"start": v(91.1, -395.75) * mm, "end": v(91.1, -389.68) * mm});
            skLineSegment(sketch, "E1618", {"start": v(91.1, -389.68) * mm, "end": v(94.13, -389.68) * mm});
            skLineSegment(sketch, "E1619", {"start": v(94.13, -389.68) * mm, "end": v(94.13, -383.6) * mm});
            skLineSegment(sketch, "E1620", {"start": v(94.13, -383.6) * mm, "end": v(91.1, -383.6) * mm});
            skLineSegment(sketch, "E1621", {"start": v(91.1, -383.6) * mm, "end": v(91.1, -377.53) * mm});
            skLineSegment(sketch, "E1622", {"start": v(91.1, -377.53) * mm, "end": v(94.13, -377.53) * mm});
            skLineSegment(sketch, "E1623", {"start": v(94.13, -377.53) * mm, "end": v(94.13, -371.46) * mm});
            skLineSegment(sketch, "E1624", {"start": v(94.13, -371.46) * mm, "end": v(91.1, -371.46) * mm});
            skLineSegment(sketch, "E1625", {"start": v(91.1, -371.46) * mm, "end": v(91.1, -365.39) * mm});
            skLineSegment(sketch, "E1626", {"start": v(91.1, -365.39) * mm, "end": v(94.13, -365.39) * mm});
            skLineSegment(sketch, "E1627", {"start": v(94.13, -365.39) * mm, "end": v(94.13, -359.31) * mm});
            skLineSegment(sketch, "E1628", {"start": v(94.13, -359.31) * mm, "end": v(91.1, -359.31) * mm});
            skLineSegment(sketch, "E1629", {"start": v(91.1, -359.31) * mm, "end": v(91.1, -353.24) * mm});
            skLineSegment(sketch, "E1630", {"start": v(91.1, -353.24) * mm, "end": v(94.13, -353.24) * mm});
            skLineSegment(sketch, "E1631", {"start": v(94.13, -353.24) * mm, "end": v(94.13, -347.17) * mm});
            skLineSegment(sketch, "E1632", {"start": v(94.13, -347.17) * mm, "end": v(91.1, -347.17) * mm});
            skLineSegment(sketch, "E1633", {"start": v(91.1, -347.17) * mm, "end": v(91.1, -341.1) * mm});
            skLineSegment(sketch, "E1634", {"start": v(91.1, -341.1) * mm, "end": v(94.13, -341.1) * mm});
            skLineSegment(sketch, "E1635", {"start": v(94.13, -341.1) * mm, "end": v(94.13, -335.02) * mm});
            skLineSegment(sketch, "E1636", {"start": v(94.13, -335.02) * mm, "end": v(91.1, -335.02) * mm});
            skLineSegment(sketch, "E1637", {"start": v(91.1, -335.02) * mm, "end": v(91.1, -328.95) * mm});
            skLineSegment(sketch, "E1638", {"start": v(91.1, -328.95) * mm, "end": v(94.13, -328.95) * mm});
            skLineSegment(sketch, "E1639", {"start": v(94.13, -328.95) * mm, "end": v(94.13, -322.88) * mm});
            skLineSegment(sketch, "E1640", {"start": v(94.13, -322.88) * mm, "end": v(91.1, -322.88) * mm});
            skLineSegment(sketch, "E1641", {"start": v(91.1, -322.88) * mm, "end": v(91.1, -316.8) * mm});
            skLineSegment(sketch, "E1642", {"start": v(91.1, -316.8) * mm, "end": v(94.13, -316.8) * mm});
            skLineSegment(sketch, "E1643", {"start": v(94.13, -316.8) * mm, "end": v(94.13, -310.73) * mm});
            skLineSegment(sketch, "E1644", {"start": v(94.13, -310.73) * mm, "end": v(91.1, -310.73) * mm});
            skLineSegment(sketch, "E1645", {"start": v(91.1, -310.73) * mm, "end": v(91.1, -304.66) * mm});
            skLineSegment(sketch, "E1646", {"start": v(91.1, -304.66) * mm, "end": v(94.13, -304.66) * mm});
            skLineSegment(sketch, "E1647", {"start": v(94.13, -304.66) * mm, "end": v(94.13, -298.58) * mm});
            skLineSegment(sketch, "E1648", {"start": v(94.13, -298.58) * mm, "end": v(91.1, -298.58) * mm});
            skLineSegment(sketch, "E1649", {"start": v(91.1, -298.58) * mm, "end": v(91.1, -292.51) * mm});
            skLineSegment(sketch, "E1650", {"start": v(91.1, -292.51) * mm, "end": v(94.13, -292.51) * mm});
            skLineSegment(sketch, "E1651", {"start": v(94.13, -292.51) * mm, "end": v(94.13, -286.44) * mm});
            skLineSegment(sketch, "E1652", {"start": v(94.13, -286.44) * mm, "end": v(91.1, -286.44) * mm});
            skLineSegment(sketch, "E1653", {"start": v(91.1, -286.44) * mm, "end": v(91.1, -280.36) * mm});
            skLineSegment(sketch, "E1654", {"start": v(91.1, -280.36) * mm, "end": v(94.13, -280.36) * mm});
            skLineSegment(sketch, "E1655", {"start": v(94.13, -280.36) * mm, "end": v(94.13, -274.3) * mm});
            skLineSegment(sketch, "E1656", {"start": v(94.13, -274.3) * mm, "end": v(91.1, -274.3) * mm});
            skLineSegment(sketch, "E1657", {"start": v(91.1, -274.3) * mm, "end": v(91.1, -268.22) * mm});
            skLineSegment(sketch, "E1658", {"start": v(91.1, -268.22) * mm, "end": v(94.13, -268.22) * mm});
            skLineSegment(sketch, "E1659", {"start": v(94.13, -268.22) * mm, "end": v(94.13, -262.15) * mm});
            skLineSegment(sketch, "E1660", {"start": v(94.13, -262.15) * mm, "end": v(91.1, -262.15) * mm});
            skLineSegment(sketch, "E1661", {"start": v(91.1, -262.15) * mm, "end": v(91.1, -256.07) * mm});
            skLineSegment(sketch, "E1662", {"start": v(91.1, -256.07) * mm, "end": v(94.13, -256.07) * mm});
            skLineSegment(sketch, "E1663", {"start": v(94.13, -256.07) * mm, "end": v(94.13, -250) * mm});
            skLineSegment(sketch, "E1664", {"start": v(94.13, -250) * mm, "end": v(91.1, -250) * mm});
            skLineSegment(sketch, "E1665", {"start": v(91.1, -250) * mm, "end": v(91.1, -243.93) * mm});
            skLineSegment(sketch, "E1666", {"start": v(91.1, -243.93) * mm, "end": v(94.13, -243.93) * mm});
            skLineSegment(sketch, "E1667", {"start": v(94.13, -243.93) * mm, "end": v(94.13, -237.85) * mm});
            skLineSegment(sketch, "E1668", {"start": v(94.13, -237.85) * mm, "end": v(91.1, -237.85) * mm});
            skLineSegment(sketch, "E1669", {"start": v(91.1, -237.85) * mm, "end": v(91.1, -231.78) * mm});
            skLineSegment(sketch, "E1670", {"start": v(91.1, -231.78) * mm, "end": v(94.13, -231.78) * mm});
            skLineSegment(sketch, "E1671", {"start": v(94.13, -231.78) * mm, "end": v(94.13, -225.7) * mm});
            skLineSegment(sketch, "E1672", {"start": v(94.13, -225.7) * mm, "end": v(91.1, -225.7) * mm});
            skLineSegment(sketch, "E1673", {"start": v(91.1, -225.7) * mm, "end": v(91.1, -219.64) * mm});
            skLineSegment(sketch, "E1674", {"start": v(91.1, -219.64) * mm, "end": v(94.13, -219.64) * mm});
            skLineSegment(sketch, "E1675", {"start": v(94.13, -219.64) * mm, "end": v(94.13, -213.56) * mm});
            skLineSegment(sketch, "E1676", {"start": v(94.13, -213.56) * mm, "end": v(91.1, -213.56) * mm});
            skLineSegment(sketch, "E1677", {"start": v(91.1, -213.56) * mm, "end": v(91.1, -207.49) * mm});
            skLineSegment(sketch, "E1678", {"start": v(91.1, -207.49) * mm, "end": v(94.13, -207.49) * mm});
            skLineSegment(sketch, "E1679", {"start": v(94.13, -207.49) * mm, "end": v(94.13, -201.42) * mm});
            skLineSegment(sketch, "E1680", {"start": v(94.13, -201.42) * mm, "end": v(91.1, -201.42) * mm});
            skLineSegment(sketch, "E1681", {"start": v(91.1, -201.42) * mm, "end": v(91.1, -195.35) * mm});
            skLineSegment(sketch, "E1682", {"start": v(91.1, -195.35) * mm, "end": v(94.13, -195.35) * mm});
            skLineSegment(sketch, "E1683", {"start": v(94.13, -195.35) * mm, "end": v(94.13, -189.27) * mm});
            skLineSegment(sketch, "E1684", {"start": v(94.13, -189.27) * mm, "end": v(91.1, -189.27) * mm});
            skLineSegment(sketch, "E1685", {"start": v(91.1, -189.27) * mm, "end": v(91.1, -183.2) * mm});
            skLineSegment(sketch, "E1686", {"start": v(91.1, -183.2) * mm, "end": v(94.13, -183.2) * mm});
            skLineSegment(sketch, "E1687", {"start": v(94.13, -183.2) * mm, "end": v(94.13, -177.13) * mm});
            skLineSegment(sketch, "E1688", {"start": v(94.13, -177.13) * mm, "end": v(91.1, -177.13) * mm});
            skLineSegment(sketch, "E1689", {"start": v(91.1, -177.13) * mm, "end": v(91.1, -171.05) * mm});
            skLineSegment(sketch, "E1690", {"start": v(91.1, -171.05) * mm, "end": v(94.13, -171.05) * mm});
            skLineSegment(sketch, "E1691", {"start": v(94.13, -171.05) * mm, "end": v(94.13, -164.98) * mm});
            skLineSegment(sketch, "E1692", {"start": v(94.13, -164.98) * mm, "end": v(91.1, -164.98) * mm});
            skLineSegment(sketch, "E1693", {"start": v(91.1, -164.98) * mm, "end": v(91.1, -158.9) * mm});
            skLineSegment(sketch, "E1694", {"start": v(91.1, -158.9) * mm, "end": v(94.13, -158.9) * mm});
            skLineSegment(sketch, "E1695", {"start": v(94.13, -158.9) * mm, "end": v(94.13, -152.83) * mm});
            skLineSegment(sketch, "E1696", {"start": v(94.13, -152.83) * mm, "end": v(91.1, -152.83) * mm});
            skLineSegment(sketch, "E1697", {"start": v(91.1, -152.83) * mm, "end": v(91.1, -146.76) * mm});
            skLineSegment(sketch, "E1698", {"start": v(91.1, -146.76) * mm, "end": v(94.13, -146.76) * mm});
            skLineSegment(sketch, "E1699", {"start": v(94.13, -146.76) * mm, "end": v(94.13, -140.69) * mm});
            skLineSegment(sketch, "E1700", {"start": v(94.13, -140.69) * mm, "end": v(91.1, -140.69) * mm});
            skLineSegment(sketch, "E1701", {"start": v(91.1, -140.69) * mm, "end": v(91.1, -134.62) * mm});
            skLineSegment(sketch, "E1702", {"start": v(91.1, -134.62) * mm, "end": v(94.13, -134.62) * mm});
            skLineSegment(sketch, "E1703", {"start": v(94.13, -134.62) * mm, "end": v(94.13, -128.54) * mm});
            skLineSegment(sketch, "E1704", {"start": v(94.13, -128.54) * mm, "end": v(91.1, -128.54) * mm});
            skLineSegment(sketch, "E1705", {"start": v(91.1, -128.54) * mm, "end": v(91.1, -122.47) * mm});
            skLineSegment(sketch, "E1706", {"start": v(91.1, -122.47) * mm, "end": v(94.13, -122.47) * mm});
            skLineSegment(sketch, "E1707", {"start": v(94.13, -122.47) * mm, "end": v(94.13, -116.4) * mm});
            skLineSegment(sketch, "E1708", {"start": v(94.13, -116.4) * mm, "end": v(91.1, -116.4) * mm});
            skLineSegment(sketch, "E1709", {"start": v(91.1, -116.4) * mm, "end": v(91.1, -110.32) * mm});
            skLineSegment(sketch, "E1710", {"start": v(91.1, -110.32) * mm, "end": v(94.13, -110.32) * mm});
            skLineSegment(sketch, "E1711", {"start": v(94.13, -110.32) * mm, "end": v(94.13, -104.25) * mm});
            skLineSegment(sketch, "E1712", {"start": v(94.13, -104.25) * mm, "end": v(91.1, -104.25) * mm});
            skLineSegment(sketch, "E1713", {"start": v(91.1, -104.25) * mm, "end": v(91.1, -98.18) * mm});
            skLineSegment(sketch, "E1714", {"start": v(91.1, -98.18) * mm, "end": v(94.13, -98.18) * mm});
            skLineSegment(sketch, "E1715", {"start": v(94.13, -98.18) * mm, "end": v(94.13, -92.1) * mm});
            skLineSegment(sketch, "E1716", {"start": v(94.13, -92.1) * mm, "end": v(91.1, -92.1) * mm});
            skLineSegment(sketch, "E1717", {"start": v(91.1, -92.1) * mm, "end": v(91.1, -86.03) * mm});
            skLineSegment(sketch, "E1718", {"start": v(91.1, -86.03) * mm, "end": v(94.13, -86.03) * mm});
            skLineSegment(sketch, "E1719", {"start": v(94.13, -86.03) * mm, "end": v(94.13, -79.96) * mm});
            skLineSegment(sketch, "E1720", {"start": v(94.13, -79.96) * mm, "end": v(91.1, -79.96) * mm});
            skLineSegment(sketch, "E1721", {"start": v(91.1, -79.96) * mm, "end": v(91.1, -73.89) * mm});
            skLineSegment(sketch, "E1722", {"start": v(91.1, -73.89) * mm, "end": v(94.13, -73.89) * mm});
            skLineSegment(sketch, "E1723", {"start": v(94.13, -73.89) * mm, "end": v(94.13, -67.81) * mm});
            skLineSegment(sketch, "E1724", {"start": v(94.13, -67.81) * mm, "end": v(91.1, -67.81) * mm});
            skLineSegment(sketch, "E1725", {"start": v(91.1, -67.81) * mm, "end": v(91.1, -61.74) * mm});
            skLineSegment(sketch, "E1726", {"start": v(91.1, -61.74) * mm, "end": v(94.13, -61.74) * mm});
            skLineSegment(sketch, "E1727", {"start": v(94.13, -61.74) * mm, "end": v(94.13, -55.67) * mm});
            skLineSegment(sketch, "E1728", {"start": v(94.13, -55.67) * mm, "end": v(91.1, -55.67) * mm});
            skLineSegment(sketch, "E1729", {"start": v(91.1, -55.67) * mm, "end": v(91.1, -49.6) * mm});
            skLineSegment(sketch, "E1730", {"start": v(91.1, -49.6) * mm, "end": v(94.13, -49.6) * mm});
            skLineSegment(sketch, "E1731", {"start": v(94.13, -49.6) * mm, "end": v(94.13, -43.52) * mm});
            skLineSegment(sketch, "E1732", {"start": v(94.13, -43.52) * mm, "end": v(91.1, -43.52) * mm});
            skLineSegment(sketch, "E1733", {"start": v(91.1, -43.52) * mm, "end": v(91.1, -37.45) * mm});
            skLineSegment(sketch, "E1734", {"start": v(91.1, -37.45) * mm, "end": v(94.13, -37.45) * mm});
            skLineSegment(sketch, "E1735", {"start": v(94.13, -37.45) * mm, "end": v(94.13, -31.38) * mm});
            skLineSegment(sketch, "E1736", {"start": v(94.13, -31.38) * mm, "end": v(91.1, -31.38) * mm});
            skLineSegment(sketch, "E1737", {"start": v(91.1, -31.38) * mm, "end": v(91.1, -25.3) * mm});
            skLineSegment(sketch, "E1738", {"start": v(91.1, -25.3) * mm, "end": v(94.13, -25.3) * mm});
            skLineSegment(sketch, "E1739", {"start": v(94.13, -25.3) * mm, "end": v(94.13, -19.23) * mm});
            skLineSegment(sketch, "E1740", {"start": v(94.13, -19.23) * mm, "end": v(91.1, -19.23) * mm});
            skLineSegment(sketch, "E1741", {"start": v(91.1, -19.23) * mm, "end": v(91.1, -9.62) * mm});
            skLineSegment(sketch, "E1742", {"start": v(91.1, -9.62) * mm, "end": v(94.13, -9.62) * mm});
            skLineSegment(sketch, "E1743", {"start": v(94.13, -9.62) * mm, "end": v(94.13, 0) * mm});
            skLineSegment(sketch, "E1744", {"start": v(-199.9, -48.58) * mm, "end": v(-199.9, -49.22) * mm});
            skLineSegment(sketch, "E1745", {"start": v(-199.9, -49.22) * mm, "end": v(-200.16, -51.13) * mm});
            skLineSegment(sketch, "E1746", {"start": v(-200.16, -51.13) * mm, "end": v(-200.9, -53.5) * mm});
            skLineSegment(sketch, "E1747", {"start": v(-200.9, -53.5) * mm, "end": v(-202.06, -55.66) * mm});
            skLineSegment(sketch, "E1748", {"start": v(-202.06, -55.66) * mm, "end": v(-203.6, -57.53) * mm});
            skLineSegment(sketch, "E1749", {"start": v(-203.6, -57.53) * mm, "end": v(-205.48, -59.07) * mm});
            skLineSegment(sketch, "E1750", {"start": v(-205.48, -59.07) * mm, "end": v(-207.63, -60.24) * mm});
            skLineSegment(sketch, "E1751", {"start": v(-207.63, -60.24) * mm, "end": v(-210, -60.98) * mm});
            skLineSegment(sketch, "E1752", {"start": v(-210, -60.98) * mm, "end": v(-211.91, -61.23) * mm});
            skLineSegment(sketch, "E1753", {"start": v(-211.91, -61.23) * mm, "end": v(-212.55, -61.23) * mm});
            skLineSegment(sketch, "E1754", {"start": v(-212.55, -61.23) * mm, "end": v(-213.19, -61.23) * mm});
            skLineSegment(sketch, "E1755", {"start": v(-213.19, -61.23) * mm, "end": v(-215.1, -60.98) * mm});
            skLineSegment(sketch, "E1756", {"start": v(-215.1, -60.98) * mm, "end": v(-217.48, -60.24) * mm});
            skLineSegment(sketch, "E1757", {"start": v(-217.48, -60.24) * mm, "end": v(-219.63, -59.07) * mm});
            skLineSegment(sketch, "E1758", {"start": v(-219.63, -59.07) * mm, "end": v(-221.5, -57.53) * mm});
            skLineSegment(sketch, "E1759", {"start": v(-221.5, -57.53) * mm, "end": v(-223.04, -55.66) * mm});
            skLineSegment(sketch, "E1760", {"start": v(-223.04, -55.66) * mm, "end": v(-224.21, -53.5) * mm});
            skLineSegment(sketch, "E1761", {"start": v(-224.21, -53.5) * mm, "end": v(-224.95, -51.13) * mm});
            skLineSegment(sketch, "E1762", {"start": v(-224.95, -51.13) * mm, "end": v(-225.2, -49.22) * mm});
            skLineSegment(sketch, "E1763", {"start": v(-225.2, -49.22) * mm, "end": v(-225.2, -48.58) * mm});
            skLineSegment(sketch, "E1764", {"start": v(-225.2, -48.58) * mm, "end": v(-225.2, -47.95) * mm});
            skLineSegment(sketch, "E1765", {"start": v(-225.2, -47.95) * mm, "end": v(-224.95, -46.03) * mm});
            skLineSegment(sketch, "E1766", {"start": v(-224.95, -46.03) * mm, "end": v(-224.21, -43.66) * mm});
            skLineSegment(sketch, "E1767", {"start": v(-224.21, -43.66) * mm, "end": v(-223.04, -41.5) * mm});
            skLineSegment(sketch, "E1768", {"start": v(-223.04, -41.5) * mm, "end": v(-221.5, -39.64) * mm});
            skLineSegment(sketch, "E1769", {"start": v(-221.5, -39.64) * mm, "end": v(-219.63, -38.1) * mm});
            skLineSegment(sketch, "E1770", {"start": v(-219.63, -38.1) * mm, "end": v(-217.48, -36.92) * mm});
            skLineSegment(sketch, "E1771", {"start": v(-217.48, -36.92) * mm, "end": v(-215.1, -36.19) * mm});
            skLineSegment(sketch, "E1772", {"start": v(-215.1, -36.19) * mm, "end": v(-213.19, -35.93) * mm});
            skLineSegment(sketch, "E1773", {"start": v(-213.19, -35.93) * mm, "end": v(-212.55, -35.93) * mm});
            skLineSegment(sketch, "E1774", {"start": v(-212.55, -35.93) * mm, "end": v(-211.91, -35.93) * mm});
            skLineSegment(sketch, "E1775", {"start": v(-211.91, -35.93) * mm, "end": v(-210, -36.19) * mm});
            skLineSegment(sketch, "E1776", {"start": v(-210, -36.19) * mm, "end": v(-207.63, -36.92) * mm});
            skLineSegment(sketch, "E1777", {"start": v(-207.63, -36.92) * mm, "end": v(-205.48, -38.1) * mm});
            skLineSegment(sketch, "E1778", {"start": v(-205.48, -38.1) * mm, "end": v(-203.6, -39.64) * mm});
            skLineSegment(sketch, "E1779", {"start": v(-203.6, -39.64) * mm, "end": v(-202.06, -41.5) * mm});
            skLineSegment(sketch, "E1780", {"start": v(-202.06, -41.5) * mm, "end": v(-200.9, -43.66) * mm});
            skLineSegment(sketch, "E1781", {"start": v(-200.9, -43.66) * mm, "end": v(-200.16, -46.03) * mm});
            skLineSegment(sketch, "E1782", {"start": v(-200.16, -46.03) * mm, "end": v(-199.9, -47.95) * mm});
            skLineSegment(sketch, "E1783", {"start": v(-199.9, -47.95) * mm, "end": v(-199.9, -48.58) * mm});
            skLineSegment(sketch, "E1784", {"start": v(-270.24, -3.04) * mm, "end": v(-265.69, -3.04) * mm});
            skLineSegment(sketch, "E1785", {"start": v(-265.69, -3.04) * mm, "end": v(-265.69, 0) * mm});
            skLineSegment(sketch, "E1786", {"start": v(-265.69, 0) * mm, "end": v(-258.1, 0) * mm});
            skLineSegment(sketch, "E1787", {"start": v(-258.1, 0) * mm, "end": v(-258.1, -3.04) * mm});
            skLineSegment(sketch, "E1788", {"start": v(-258.1, -3.04) * mm, "end": v(-252.03, -3.04) * mm});
            skLineSegment(sketch, "E1789", {"start": v(-252.03, -3.04) * mm, "end": v(-252.03, 0) * mm});
            skLineSegment(sketch, "E1790", {"start": v(-252.03, 0) * mm, "end": v(-245.95, 0) * mm});
            skLineSegment(sketch, "E1791", {"start": v(-245.95, 0) * mm, "end": v(-245.95, -3.04) * mm});
            skLineSegment(sketch, "E1792", {"start": v(-245.95, -3.04) * mm, "end": v(-239.88, -3.04) * mm});
            skLineSegment(sketch, "E1793", {"start": v(-239.88, -3.04) * mm, "end": v(-239.88, 0) * mm});
            skLineSegment(sketch, "E1794", {"start": v(-239.88, 0) * mm, "end": v(-233.8, 0) * mm});
            skLineSegment(sketch, "E1795", {"start": v(-233.8, 0) * mm, "end": v(-233.8, -3.04) * mm});
            skLineSegment(sketch, "E1796", {"start": v(-233.8, -3.04) * mm, "end": v(-227.73, -3.04) * mm});
            skLineSegment(sketch, "E1797", {"start": v(-227.73, -3.04) * mm, "end": v(-227.73, 0) * mm});
            skLineSegment(sketch, "E1798", {"start": v(-227.73, 0) * mm, "end": v(-221.66, 0) * mm});
            skLineSegment(sketch, "E1799", {"start": v(-221.66, 0) * mm, "end": v(-221.66, -3.04) * mm});
            skLineSegment(sketch, "E1800", {"start": v(-221.66, -3.04) * mm, "end": v(-215.59, -3.04) * mm});
            skLineSegment(sketch, "E1801", {"start": v(-215.59, -3.04) * mm, "end": v(-215.59, 0) * mm});
            skLineSegment(sketch, "E1802", {"start": v(-215.59, 0) * mm, "end": v(-209.52, 0) * mm});
            skLineSegment(sketch, "E1803", {"start": v(-209.52, 0) * mm, "end": v(-209.52, -3.04) * mm});
            skLineSegment(sketch, "E1804", {"start": v(-209.52, -3.04) * mm, "end": v(-203.44, -3.04) * mm});
            skLineSegment(sketch, "E1805", {"start": v(-203.44, -3.04) * mm, "end": v(-203.44, 0) * mm});
            skLineSegment(sketch, "E1806", {"start": v(-203.44, 0) * mm, "end": v(-197.37, 0) * mm});
            skLineSegment(sketch, "E1807", {"start": v(-197.37, 0) * mm, "end": v(-197.37, -3.04) * mm});
            skLineSegment(sketch, "E1808", {"start": v(-197.37, -3.04) * mm, "end": v(-191.3, -3.04) * mm});
            skLineSegment(sketch, "E1809", {"start": v(-191.3, -3.04) * mm, "end": v(-191.3, 0) * mm});
            skLineSegment(sketch, "E1810", {"start": v(-191.3, 0) * mm, "end": v(-185.22, 0) * mm});
            skLineSegment(sketch, "E1811", {"start": v(-185.22, 0) * mm, "end": v(-185.22, -3.04) * mm});
            skLineSegment(sketch, "E1812", {"start": v(-185.22, -3.04) * mm, "end": v(-179.15, -3.04) * mm});
            skLineSegment(sketch, "E1813", {"start": v(-179.15, -3.04) * mm, "end": v(-179.15, 0) * mm});
            skLineSegment(sketch, "E1814", {"start": v(-179.15, 0) * mm, "end": v(-173.08, 0) * mm});
            skLineSegment(sketch, "E1815", {"start": v(-173.08, 0) * mm, "end": v(-173.08, -3.04) * mm});
            skLineSegment(sketch, "E1816", {"start": v(-173.08, -3.04) * mm, "end": v(-167, -3.04) * mm});
            skLineSegment(sketch, "E1817", {"start": v(-167, -3.04) * mm, "end": v(-167, 0) * mm});
            skLineSegment(sketch, "E1818", {"start": v(-167, 0) * mm, "end": v(-160.93, 0) * mm});
            skLineSegment(sketch, "E1819", {"start": v(-160.93, 0) * mm, "end": v(-160.93, -3.04) * mm});
            skLineSegment(sketch, "E1820", {"start": v(-160.93, -3.04) * mm, "end": v(-154.86, -3.04) * mm});
            skLineSegment(sketch, "E1821", {"start": v(-154.86, -3.04) * mm, "end": v(-154.86, 0) * mm});
            skLineSegment(sketch, "E1822", {"start": v(-154.86, 0) * mm, "end": v(-148.79, 0) * mm});
            skLineSegment(sketch, "E1823", {"start": v(-148.79, 0) * mm, "end": v(-148.79, -3.04) * mm});
            skLineSegment(sketch, "E1824", {"start": v(-148.79, -3.04) * mm, "end": v(-142.71, -3.04) * mm});
            skLineSegment(sketch, "E1825", {"start": v(-142.71, -3.04) * mm, "end": v(-142.71, 0) * mm});
            skLineSegment(sketch, "E1826", {"start": v(-142.71, 0) * mm, "end": v(-136.64, 0) * mm});
            skLineSegment(sketch, "E1827", {"start": v(-136.64, 0) * mm, "end": v(-136.64, -3.04) * mm});
            skLineSegment(sketch, "E1828", {"start": v(-136.64, -3.04) * mm, "end": v(-130.57, -3.04) * mm});
            skLineSegment(sketch, "E1829", {"start": v(-130.57, -3.04) * mm, "end": v(-130.57, 0) * mm});
            skLineSegment(sketch, "E1830", {"start": v(-130.57, 0) * mm, "end": v(-124.5, 0) * mm});
            skLineSegment(sketch, "E1831", {"start": v(-124.5, 0) * mm, "end": v(-124.5, -3.04) * mm});
            skLineSegment(sketch, "E1832", {"start": v(-124.5, -3.04) * mm, "end": v(-118.42, -3.04) * mm});
            skLineSegment(sketch, "E1833", {"start": v(-118.42, -3.04) * mm, "end": v(-118.42, 0) * mm});
            skLineSegment(sketch, "E1834", {"start": v(-118.42, 0) * mm, "end": v(-112.35, 0) * mm});
            skLineSegment(sketch, "E1835", {"start": v(-112.35, 0) * mm, "end": v(-112.35, -3.04) * mm});
            skLineSegment(sketch, "E1836", {"start": v(-112.35, -3.04) * mm, "end": v(-106.28, -3.04) * mm});
            skLineSegment(sketch, "E1837", {"start": v(-106.28, -3.04) * mm, "end": v(-106.28, 0) * mm});
            skLineSegment(sketch, "E1838", {"start": v(-106.28, 0) * mm, "end": v(-98.68, 0) * mm});
            skLineSegment(sketch, "E1839", {"start": v(-98.68, 0) * mm, "end": v(-98.68, -3.04) * mm});
            skLineSegment(sketch, "E1840", {"start": v(-98.68, -3.04) * mm, "end": v(-94.13, -3.04) * mm});
            skLineSegment(sketch, "E1841", {"start": v(-94.13, -3.04) * mm, "end": v(-94.13, -7.6) * mm});
            skLineSegment(sketch, "E1842", {"start": v(-94.13, -7.6) * mm, "end": v(-91.1, -7.6) * mm});
            skLineSegment(sketch, "E1843", {"start": v(-91.1, -7.6) * mm, "end": v(-91.1, -15.18) * mm});
            skLineSegment(sketch, "E1844", {"start": v(-91.1, -15.18) * mm, "end": v(-94.13, -15.18) * mm});
            skLineSegment(sketch, "E1845", {"start": v(-94.13, -15.18) * mm, "end": v(-94.13, -21.26) * mm});
            skLineSegment(sketch, "E1846", {"start": v(-94.13, -21.26) * mm, "end": v(-91.1, -21.26) * mm});
            skLineSegment(sketch, "E1847", {"start": v(-91.1, -21.26) * mm, "end": v(-91.1, -27.33) * mm});
            skLineSegment(sketch, "E1848", {"start": v(-91.1, -27.33) * mm, "end": v(-94.13, -27.33) * mm});
            skLineSegment(sketch, "E1849", {"start": v(-94.13, -27.33) * mm, "end": v(-94.13, -33.4) * mm});
            skLineSegment(sketch, "E1850", {"start": v(-94.13, -33.4) * mm, "end": v(-91.1, -33.4) * mm});
            skLineSegment(sketch, "E1851", {"start": v(-91.1, -33.4) * mm, "end": v(-91.1, -39.47) * mm});
            skLineSegment(sketch, "E1852", {"start": v(-91.1, -39.47) * mm, "end": v(-94.13, -39.47) * mm});
            skLineSegment(sketch, "E1853", {"start": v(-94.13, -39.47) * mm, "end": v(-94.13, -45.55) * mm});
            skLineSegment(sketch, "E1854", {"start": v(-94.13, -45.55) * mm, "end": v(-91.1, -45.55) * mm});
            skLineSegment(sketch, "E1855", {"start": v(-91.1, -45.55) * mm, "end": v(-91.1, -51.62) * mm});
            skLineSegment(sketch, "E1856", {"start": v(-91.1, -51.62) * mm, "end": v(-94.13, -51.62) * mm});
            skLineSegment(sketch, "E1857", {"start": v(-94.13, -51.62) * mm, "end": v(-94.13, -57.7) * mm});
            skLineSegment(sketch, "E1858", {"start": v(-94.13, -57.7) * mm, "end": v(-91.1, -57.7) * mm});
            skLineSegment(sketch, "E1859", {"start": v(-91.1, -57.7) * mm, "end": v(-91.1, -63.76) * mm});
            skLineSegment(sketch, "E1860", {"start": v(-91.1, -63.76) * mm, "end": v(-94.13, -63.76) * mm});
            skLineSegment(sketch, "E1861", {"start": v(-94.13, -63.76) * mm, "end": v(-94.13, -69.84) * mm});
            skLineSegment(sketch, "E1862", {"start": v(-94.13, -69.84) * mm, "end": v(-91.1, -69.84) * mm});
            skLineSegment(sketch, "E1863", {"start": v(-91.1, -69.84) * mm, "end": v(-91.1, -75.91) * mm});
            skLineSegment(sketch, "E1864", {"start": v(-91.1, -75.91) * mm, "end": v(-94.13, -75.91) * mm});
            skLineSegment(sketch, "E1865", {"start": v(-94.13, -75.91) * mm, "end": v(-94.13, -81.99) * mm});
            skLineSegment(sketch, "E1866", {"start": v(-94.13, -81.99) * mm, "end": v(-91.1, -81.99) * mm});
            skLineSegment(sketch, "E1867", {"start": v(-91.1, -81.99) * mm, "end": v(-91.1, -88.06) * mm});
            skLineSegment(sketch, "E1868", {"start": v(-91.1, -88.06) * mm, "end": v(-94.13, -88.06) * mm});
            skLineSegment(sketch, "E1869", {"start": v(-94.13, -88.06) * mm, "end": v(-94.13, -94.13) * mm});
            skLineSegment(sketch, "E1870", {"start": v(-94.13, -94.13) * mm, "end": v(-91.1, -94.13) * mm});
            skLineSegment(sketch, "E1871", {"start": v(-91.1, -94.13) * mm, "end": v(-91.1, -100.2) * mm});
            skLineSegment(sketch, "E1872", {"start": v(-91.1, -100.2) * mm, "end": v(-94.13, -100.2) * mm});
            skLineSegment(sketch, "E1873", {"start": v(-94.13, -100.2) * mm, "end": v(-94.13, -106.28) * mm});
            skLineSegment(sketch, "E1874", {"start": v(-94.13, -106.28) * mm, "end": v(-91.1, -106.28) * mm});
            skLineSegment(sketch, "E1875", {"start": v(-91.1, -106.28) * mm, "end": v(-91.1, -112.35) * mm});
            skLineSegment(sketch, "E1876", {"start": v(-91.1, -112.35) * mm, "end": v(-94.13, -112.35) * mm});
            skLineSegment(sketch, "E1877", {"start": v(-94.13, -112.35) * mm, "end": v(-94.13, -118.42) * mm});
            skLineSegment(sketch, "E1878", {"start": v(-94.13, -118.42) * mm, "end": v(-91.1, -118.42) * mm});
            skLineSegment(sketch, "E1879", {"start": v(-91.1, -118.42) * mm, "end": v(-91.1, -124.5) * mm});
            skLineSegment(sketch, "E1880", {"start": v(-91.1, -124.5) * mm, "end": v(-94.13, -124.5) * mm});
            skLineSegment(sketch, "E1881", {"start": v(-94.13, -124.5) * mm, "end": v(-94.13, -130.57) * mm});
            skLineSegment(sketch, "E1882", {"start": v(-94.13, -130.57) * mm, "end": v(-91.1, -130.57) * mm});
            skLineSegment(sketch, "E1883", {"start": v(-91.1, -130.57) * mm, "end": v(-91.1, -136.64) * mm});
            skLineSegment(sketch, "E1884", {"start": v(-91.1, -136.64) * mm, "end": v(-94.13, -136.64) * mm});
            skLineSegment(sketch, "E1885", {"start": v(-94.13, -136.64) * mm, "end": v(-94.13, -142.71) * mm});
            skLineSegment(sketch, "E1886", {"start": v(-94.13, -142.71) * mm, "end": v(-91.1, -142.71) * mm});
            skLineSegment(sketch, "E1887", {"start": v(-91.1, -142.71) * mm, "end": v(-91.1, -148.78) * mm});
            skLineSegment(sketch, "E1888", {"start": v(-91.1, -148.78) * mm, "end": v(-94.13, -148.78) * mm});
            skLineSegment(sketch, "E1889", {"start": v(-94.13, -148.78) * mm, "end": v(-94.13, -154.86) * mm});
            skLineSegment(sketch, "E1890", {"start": v(-94.13, -154.86) * mm, "end": v(-91.1, -154.86) * mm});
            skLineSegment(sketch, "E1891", {"start": v(-91.1, -154.86) * mm, "end": v(-91.1, -160.93) * mm});
            skLineSegment(sketch, "E1892", {"start": v(-91.1, -160.93) * mm, "end": v(-94.13, -160.93) * mm});
            skLineSegment(sketch, "E1893", {"start": v(-94.13, -160.93) * mm, "end": v(-94.13, -167) * mm});
            skLineSegment(sketch, "E1894", {"start": v(-94.13, -167) * mm, "end": v(-91.1, -167) * mm});
            skLineSegment(sketch, "E1895", {"start": v(-91.1, -167) * mm, "end": v(-91.1, -174.6) * mm});
            skLineSegment(sketch, "E1896", {"start": v(-91.1, -174.6) * mm, "end": v(-94.13, -174.6) * mm});
            skLineSegment(sketch, "E1897", {"start": v(-94.13, -174.6) * mm, "end": v(-94.13, -179.15) * mm});
            skLineSegment(sketch, "E1898", {"start": v(-94.13, -179.15) * mm, "end": v(-98.68, -179.15) * mm});
            skLineSegment(sketch, "E1899", {"start": v(-98.68, -179.15) * mm, "end": v(-98.68, -182.19) * mm});
            skLineSegment(sketch, "E1900", {"start": v(-98.68, -182.19) * mm, "end": v(-106.28, -182.19) * mm});
            skLineSegment(sketch, "E1901", {"start": v(-106.28, -182.19) * mm, "end": v(-106.28, -179.15) * mm});
            skLineSegment(sketch, "E1902", {"start": v(-106.28, -179.15) * mm, "end": v(-112.35, -179.15) * mm});
            skLineSegment(sketch, "E1903", {"start": v(-112.35, -179.15) * mm, "end": v(-112.35, -182.19) * mm});
            skLineSegment(sketch, "E1904", {"start": v(-112.35, -182.19) * mm, "end": v(-118.42, -182.19) * mm});
            skLineSegment(sketch, "E1905", {"start": v(-118.42, -182.19) * mm, "end": v(-118.42, -179.15) * mm});
            skLineSegment(sketch, "E1906", {"start": v(-118.42, -179.15) * mm, "end": v(-124.5, -179.15) * mm});
            skLineSegment(sketch, "E1907", {"start": v(-124.5, -179.15) * mm, "end": v(-124.5, -182.19) * mm});
            skLineSegment(sketch, "E1908", {"start": v(-124.5, -182.19) * mm, "end": v(-130.57, -182.19) * mm});
            skLineSegment(sketch, "E1909", {"start": v(-130.57, -182.19) * mm, "end": v(-130.57, -179.15) * mm});
            skLineSegment(sketch, "E1910", {"start": v(-130.57, -179.15) * mm, "end": v(-136.64, -179.15) * mm});
            skLineSegment(sketch, "E1911", {"start": v(-136.64, -179.15) * mm, "end": v(-136.64, -182.19) * mm});
            skLineSegment(sketch, "E1912", {"start": v(-136.64, -182.19) * mm, "end": v(-142.71, -182.19) * mm});
            skLineSegment(sketch, "E1913", {"start": v(-142.71, -182.19) * mm, "end": v(-142.71, -179.15) * mm});
            skLineSegment(sketch, "E1914", {"start": v(-142.71, -179.15) * mm, "end": v(-148.79, -179.15) * mm});
            skLineSegment(sketch, "E1915", {"start": v(-148.79, -179.15) * mm, "end": v(-148.79, -182.19) * mm});
            skLineSegment(sketch, "E1916", {"start": v(-148.79, -182.19) * mm, "end": v(-154.86, -182.19) * mm});
            skLineSegment(sketch, "E1917", {"start": v(-154.86, -182.19) * mm, "end": v(-154.86, -179.15) * mm});
            skLineSegment(sketch, "E1918", {"start": v(-154.86, -179.15) * mm, "end": v(-160.93, -179.15) * mm});
            skLineSegment(sketch, "E1919", {"start": v(-160.93, -179.15) * mm, "end": v(-160.93, -182.19) * mm});
            skLineSegment(sketch, "E1920", {"start": v(-160.93, -182.19) * mm, "end": v(-167, -182.19) * mm});
            skLineSegment(sketch, "E1921", {"start": v(-167, -182.19) * mm, "end": v(-167, -179.15) * mm});
            skLineSegment(sketch, "E1922", {"start": v(-167, -179.15) * mm, "end": v(-173.08, -179.15) * mm});
            skLineSegment(sketch, "E1923", {"start": v(-173.08, -179.15) * mm, "end": v(-173.08, -182.19) * mm});
            skLineSegment(sketch, "E1924", {"start": v(-173.08, -182.19) * mm, "end": v(-179.15, -182.19) * mm});
            skLineSegment(sketch, "E1925", {"start": v(-179.15, -182.19) * mm, "end": v(-179.15, -179.15) * mm});
            skLineSegment(sketch, "E1926", {"start": v(-179.15, -179.15) * mm, "end": v(-185.22, -179.15) * mm});
            skLineSegment(sketch, "E1927", {"start": v(-185.22, -179.15) * mm, "end": v(-185.22, -182.19) * mm});
            skLineSegment(sketch, "E1928", {"start": v(-185.22, -182.19) * mm, "end": v(-191.3, -182.19) * mm});
            skLineSegment(sketch, "E1929", {"start": v(-191.3, -182.19) * mm, "end": v(-191.3, -179.15) * mm});
            skLineSegment(sketch, "E1930", {"start": v(-191.3, -179.15) * mm, "end": v(-197.37, -179.15) * mm});
            skLineSegment(sketch, "E1931", {"start": v(-197.37, -179.15) * mm, "end": v(-197.37, -182.19) * mm});
            skLineSegment(sketch, "E1932", {"start": v(-197.37, -182.19) * mm, "end": v(-203.44, -182.19) * mm});
            skLineSegment(sketch, "E1933", {"start": v(-203.44, -182.19) * mm, "end": v(-203.44, -179.15) * mm});
            skLineSegment(sketch, "E1934", {"start": v(-203.44, -179.15) * mm, "end": v(-209.52, -179.15) * mm});
            skLineSegment(sketch, "E1935", {"start": v(-209.52, -179.15) * mm, "end": v(-209.52, -182.19) * mm});
            skLineSegment(sketch, "E1936", {"start": v(-209.52, -182.19) * mm, "end": v(-215.59, -182.19) * mm});
            skLineSegment(sketch, "E1937", {"start": v(-215.59, -182.19) * mm, "end": v(-215.59, -179.15) * mm});
            skLineSegment(sketch, "E1938", {"start": v(-215.59, -179.15) * mm, "end": v(-221.66, -179.15) * mm});
            skLineSegment(sketch, "E1939", {"start": v(-221.66, -179.15) * mm, "end": v(-221.66, -182.19) * mm});
            skLineSegment(sketch, "E1940", {"start": v(-221.66, -182.19) * mm, "end": v(-227.73, -182.19) * mm});
            skLineSegment(sketch, "E1941", {"start": v(-227.73, -182.19) * mm, "end": v(-227.73, -179.15) * mm});
            skLineSegment(sketch, "E1942", {"start": v(-227.73, -179.15) * mm, "end": v(-233.8, -179.15) * mm});
            skLineSegment(sketch, "E1943", {"start": v(-233.8, -179.15) * mm, "end": v(-233.8, -182.19) * mm});
            skLineSegment(sketch, "E1944", {"start": v(-233.8, -182.19) * mm, "end": v(-239.88, -182.19) * mm});
            skLineSegment(sketch, "E1945", {"start": v(-239.88, -182.19) * mm, "end": v(-239.88, -179.15) * mm});
            skLineSegment(sketch, "E1946", {"start": v(-239.88, -179.15) * mm, "end": v(-245.95, -179.15) * mm});
            skLineSegment(sketch, "E1947", {"start": v(-245.95, -179.15) * mm, "end": v(-245.95, -182.19) * mm});
            skLineSegment(sketch, "E1948", {"start": v(-245.95, -182.19) * mm, "end": v(-252.03, -182.19) * mm});
            skLineSegment(sketch, "E1949", {"start": v(-252.03, -182.19) * mm, "end": v(-252.03, -179.15) * mm});
            skLineSegment(sketch, "E1950", {"start": v(-252.03, -179.15) * mm, "end": v(-258.1, -179.15) * mm});
            skLineSegment(sketch, "E1951", {"start": v(-258.1, -179.15) * mm, "end": v(-258.1, -182.19) * mm});
            skLineSegment(sketch, "E1952", {"start": v(-258.1, -182.19) * mm, "end": v(-265.69, -182.19) * mm});
            skLineSegment(sketch, "E1953", {"start": v(-265.69, -182.19) * mm, "end": v(-265.69, -179.15) * mm});
            skLineSegment(sketch, "E1954", {"start": v(-265.69, -179.15) * mm, "end": v(-270.24, -179.15) * mm});
            skLineSegment(sketch, "E1955", {"start": v(-270.24, -179.15) * mm, "end": v(-270.24, -174.6) * mm});
            skLineSegment(sketch, "E1956", {"start": v(-270.24, -174.6) * mm, "end": v(-273.28, -174.6) * mm});
            skLineSegment(sketch, "E1957", {"start": v(-273.28, -174.6) * mm, "end": v(-273.28, -167) * mm});
            skLineSegment(sketch, "E1958", {"start": v(-273.28, -167) * mm, "end": v(-270.24, -167) * mm});
            skLineSegment(sketch, "E1959", {"start": v(-270.24, -167) * mm, "end": v(-270.24, -160.93) * mm});
            skLineSegment(sketch, "E1960", {"start": v(-270.24, -160.93) * mm, "end": v(-273.28, -160.93) * mm});
            skLineSegment(sketch, "E1961", {"start": v(-273.28, -160.93) * mm, "end": v(-273.28, -154.86) * mm});
            skLineSegment(sketch, "E1962", {"start": v(-273.28, -154.86) * mm, "end": v(-270.24, -154.86) * mm});
            skLineSegment(sketch, "E1963", {"start": v(-270.24, -154.86) * mm, "end": v(-270.24, -148.78) * mm});
            skLineSegment(sketch, "E1964", {"start": v(-270.24, -148.78) * mm, "end": v(-273.28, -148.78) * mm});
            skLineSegment(sketch, "E1965", {"start": v(-273.28, -148.78) * mm, "end": v(-273.28, -142.71) * mm});
            skLineSegment(sketch, "E1966", {"start": v(-273.28, -142.71) * mm, "end": v(-270.24, -142.71) * mm});
            skLineSegment(sketch, "E1967", {"start": v(-270.24, -142.71) * mm, "end": v(-270.24, -136.64) * mm});
            skLineSegment(sketch, "E1968", {"start": v(-270.24, -136.64) * mm, "end": v(-273.28, -136.64) * mm});
            skLineSegment(sketch, "E1969", {"start": v(-273.28, -136.64) * mm, "end": v(-273.28, -130.57) * mm});
            skLineSegment(sketch, "E1970", {"start": v(-273.28, -130.57) * mm, "end": v(-270.24, -130.57) * mm});
            skLineSegment(sketch, "E1971", {"start": v(-270.24, -130.57) * mm, "end": v(-270.24, -124.5) * mm});
            skLineSegment(sketch, "E1972", {"start": v(-270.24, -124.5) * mm, "end": v(-273.28, -124.5) * mm});
            skLineSegment(sketch, "E1973", {"start": v(-273.28, -124.5) * mm, "end": v(-273.28, -118.42) * mm});
            skLineSegment(sketch, "E1974", {"start": v(-273.28, -118.42) * mm, "end": v(-270.24, -118.42) * mm});
            skLineSegment(sketch, "E1975", {"start": v(-270.24, -118.42) * mm, "end": v(-270.24, -112.35) * mm});
            skLineSegment(sketch, "E1976", {"start": v(-270.24, -112.35) * mm, "end": v(-273.28, -112.35) * mm});
            skLineSegment(sketch, "E1977", {"start": v(-273.28, -112.35) * mm, "end": v(-273.28, -106.28) * mm});
            skLineSegment(sketch, "E1978", {"start": v(-273.28, -106.28) * mm, "end": v(-270.24, -106.28) * mm});
            skLineSegment(sketch, "E1979", {"start": v(-270.24, -106.28) * mm, "end": v(-270.24, -100.2) * mm});
            skLineSegment(sketch, "E1980", {"start": v(-270.24, -100.2) * mm, "end": v(-273.28, -100.2) * mm});
            skLineSegment(sketch, "E1981", {"start": v(-273.28, -100.2) * mm, "end": v(-273.28, -94.13) * mm});
            skLineSegment(sketch, "E1982", {"start": v(-273.28, -94.13) * mm, "end": v(-270.24, -94.13) * mm});
            skLineSegment(sketch, "E1983", {"start": v(-270.24, -94.13) * mm, "end": v(-270.24, -88.06) * mm});
            skLineSegment(sketch, "E1984", {"start": v(-270.24, -88.06) * mm, "end": v(-273.28, -88.06) * mm});
            skLineSegment(sketch, "E1985", {"start": v(-273.28, -88.06) * mm, "end": v(-273.28, -81.99) * mm});
            skLineSegment(sketch, "E1986", {"start": v(-273.28, -81.99) * mm, "end": v(-270.24, -81.99) * mm});
            skLineSegment(sketch, "E1987", {"start": v(-270.24, -81.99) * mm, "end": v(-270.24, -75.91) * mm});
            skLineSegment(sketch, "E1988", {"start": v(-270.24, -75.91) * mm, "end": v(-273.28, -75.91) * mm});
            skLineSegment(sketch, "E1989", {"start": v(-273.28, -75.91) * mm, "end": v(-273.28, -69.84) * mm});
            skLineSegment(sketch, "E1990", {"start": v(-273.28, -69.84) * mm, "end": v(-270.24, -69.84) * mm});
            skLineSegment(sketch, "E1991", {"start": v(-270.24, -69.84) * mm, "end": v(-270.24, -63.76) * mm});
            skLineSegment(sketch, "E1992", {"start": v(-270.24, -63.76) * mm, "end": v(-273.28, -63.76) * mm});
            skLineSegment(sketch, "E1993", {"start": v(-273.28, -63.76) * mm, "end": v(-273.28, -57.7) * mm});
            skLineSegment(sketch, "E1994", {"start": v(-273.28, -57.7) * mm, "end": v(-270.24, -57.7) * mm});
            skLineSegment(sketch, "E1995", {"start": v(-270.24, -57.7) * mm, "end": v(-270.24, -51.62) * mm});
            skLineSegment(sketch, "E1996", {"start": v(-270.24, -51.62) * mm, "end": v(-273.28, -51.62) * mm});
            skLineSegment(sketch, "E1997", {"start": v(-273.28, -51.62) * mm, "end": v(-273.28, -45.55) * mm});
            skLineSegment(sketch, "E1998", {"start": v(-273.28, -45.55) * mm, "end": v(-270.24, -45.55) * mm});
            skLineSegment(sketch, "E1999", {"start": v(-270.24, -45.55) * mm, "end": v(-270.24, -39.47) * mm});
            skLineSegment(sketch, "E2000", {"start": v(-270.24, -39.47) * mm, "end": v(-273.28, -39.47) * mm});
            skLineSegment(sketch, "E2001", {"start": v(-273.28, -39.47) * mm, "end": v(-273.28, -33.4) * mm});
            skLineSegment(sketch, "E2002", {"start": v(-273.28, -33.4) * mm, "end": v(-270.24, -33.4) * mm});
            skLineSegment(sketch, "E2003", {"start": v(-270.24, -33.4) * mm, "end": v(-270.24, -27.33) * mm});
            skLineSegment(sketch, "E2004", {"start": v(-270.24, -27.33) * mm, "end": v(-273.28, -27.33) * mm});
            skLineSegment(sketch, "E2005", {"start": v(-273.28, -27.33) * mm, "end": v(-273.28, -21.26) * mm});
            skLineSegment(sketch, "E2006", {"start": v(-273.28, -21.26) * mm, "end": v(-270.24, -21.26) * mm});
            skLineSegment(sketch, "E2007", {"start": v(-270.24, -21.26) * mm, "end": v(-270.24, -15.18) * mm});
            skLineSegment(sketch, "E2008", {"start": v(-270.24, -15.18) * mm, "end": v(-273.28, -15.18) * mm});
            skLineSegment(sketch, "E2009", {"start": v(-273.28, -15.18) * mm, "end": v(-273.28, -7.6) * mm});
            skLineSegment(sketch, "E2010", {"start": v(-273.28, -7.6) * mm, "end": v(-270.24, -7.6) * mm});
            skLineSegment(sketch, "E2011", {"start": v(-270.24, -7.6) * mm, "end": v(-270.24, -3.04) * mm});
            skLineSegment(sketch, "E2012", {"start": v(-88.06, -3.04) * mm, "end": v(-83.5, -3.04) * mm});
            skLineSegment(sketch, "E2013", {"start": v(-83.5, -3.04) * mm, "end": v(-83.5, 0) * mm});
            skLineSegment(sketch, "E2014", {"start": v(-83.5, 0) * mm, "end": v(-75.91, 0) * mm});
            skLineSegment(sketch, "E2015", {"start": v(-75.91, 0) * mm, "end": v(-75.91, -3.04) * mm});
            skLineSegment(sketch, "E2016", {"start": v(-75.91, -3.04) * mm, "end": v(-69.84, -3.04) * mm});
            skLineSegment(sketch, "E2017", {"start": v(-69.84, -3.04) * mm, "end": v(-69.84, 0) * mm});
            skLineSegment(sketch, "E2018", {"start": v(-69.84, 0) * mm, "end": v(-63.77, 0) * mm});
            skLineSegment(sketch, "E2019", {"start": v(-63.77, 0) * mm, "end": v(-63.77, -3.04) * mm});
            skLineSegment(sketch, "E2020", {"start": v(-63.77, -3.04) * mm, "end": v(-57.7, -3.04) * mm});
            skLineSegment(sketch, "E2021", {"start": v(-57.7, -3.04) * mm, "end": v(-57.7, 0) * mm});
            skLineSegment(sketch, "E2022", {"start": v(-57.7, 0) * mm, "end": v(-51.62, 0) * mm});
            skLineSegment(sketch, "E2023", {"start": v(-51.62, 0) * mm, "end": v(-51.62, -3.04) * mm});
            skLineSegment(sketch, "E2024", {"start": v(-51.62, -3.04) * mm, "end": v(-45.55, -3.04) * mm});
            skLineSegment(sketch, "E2025", {"start": v(-45.55, -3.04) * mm, "end": v(-45.55, 0) * mm});
            skLineSegment(sketch, "E2026", {"start": v(-45.55, 0) * mm, "end": v(-39.47, 0) * mm});
            skLineSegment(sketch, "E2027", {"start": v(-39.47, 0) * mm, "end": v(-39.47, -3.04) * mm});
            skLineSegment(sketch, "E2028", {"start": v(-39.47, -3.04) * mm, "end": v(-33.4, -3.04) * mm});
            skLineSegment(sketch, "E2029", {"start": v(-33.4, -3.04) * mm, "end": v(-33.4, 0) * mm});
            skLineSegment(sketch, "E2030", {"start": v(-33.4, 0) * mm, "end": v(-27.33, 0) * mm});
            skLineSegment(sketch, "E2031", {"start": v(-27.33, 0) * mm, "end": v(-27.33, -3.04) * mm});
            skLineSegment(sketch, "E2032", {"start": v(-27.33, -3.04) * mm, "end": v(-21.25, -3.04) * mm});
            skLineSegment(sketch, "E2033", {"start": v(-21.25, -3.04) * mm, "end": v(-21.25, 0) * mm});
            skLineSegment(sketch, "E2034", {"start": v(-21.25, 0) * mm, "end": v(-15.18, 0) * mm});
            skLineSegment(sketch, "E2035", {"start": v(-15.18, 0) * mm, "end": v(-15.18, -3.04) * mm});
            skLineSegment(sketch, "E2036", {"start": v(-15.18, -3.04) * mm, "end": v(-9.1, -3.04) * mm});
            skLineSegment(sketch, "E2037", {"start": v(-9.1, -3.04) * mm, "end": v(-9.1, 0) * mm});
            skLineSegment(sketch, "E2038", {"start": v(-9.1, 0) * mm, "end": v(-3.04, 0) * mm});
            skLineSegment(sketch, "E2039", {"start": v(-3.04, 0) * mm, "end": v(-3.04, -3.04) * mm});
            skLineSegment(sketch, "E2040", {"start": v(-3.04, -3.04) * mm, "end": v(3.04, -3.04) * mm});
            skLineSegment(sketch, "E2041", {"start": v(3.04, -3.04) * mm, "end": v(3.04, 0) * mm});
            skLineSegment(sketch, "E2042", {"start": v(3.04, 0) * mm, "end": v(9.1, 0) * mm});
            skLineSegment(sketch, "E2043", {"start": v(9.1, 0) * mm, "end": v(9.1, -3.04) * mm});
            skLineSegment(sketch, "E2044", {"start": v(9.1, -3.04) * mm, "end": v(15.18, -3.04) * mm});
            skLineSegment(sketch, "E2045", {"start": v(15.18, -3.04) * mm, "end": v(15.18, 0) * mm});
            skLineSegment(sketch, "E2046", {"start": v(15.18, 0) * mm, "end": v(21.25, 0) * mm});
            skLineSegment(sketch, "E2047", {"start": v(21.25, 0) * mm, "end": v(21.25, -3.04) * mm});
            skLineSegment(sketch, "E2048", {"start": v(21.25, -3.04) * mm, "end": v(27.33, -3.04) * mm});
            skLineSegment(sketch, "E2049", {"start": v(27.33, -3.04) * mm, "end": v(27.33, 0) * mm});
            skLineSegment(sketch, "E2050", {"start": v(27.33, 0) * mm, "end": v(33.4, 0) * mm});
            skLineSegment(sketch, "E2051", {"start": v(33.4, 0) * mm, "end": v(33.4, -3.04) * mm});
            skLineSegment(sketch, "E2052", {"start": v(33.4, -3.04) * mm, "end": v(39.47, -3.04) * mm});
            skLineSegment(sketch, "E2053", {"start": v(39.47, -3.04) * mm, "end": v(39.47, 0) * mm});
            skLineSegment(sketch, "E2054", {"start": v(39.47, 0) * mm, "end": v(45.54, 0) * mm});
            skLineSegment(sketch, "E2055", {"start": v(45.54, 0) * mm, "end": v(45.54, -3.04) * mm});
            skLineSegment(sketch, "E2056", {"start": v(45.54, -3.04) * mm, "end": v(51.62, -3.04) * mm});
            skLineSegment(sketch, "E2057", {"start": v(51.62, -3.04) * mm, "end": v(51.62, 0) * mm});
            skLineSegment(sketch, "E2058", {"start": v(51.62, 0) * mm, "end": v(57.7, 0) * mm});
            skLineSegment(sketch, "E2059", {"start": v(57.7, 0) * mm, "end": v(57.7, -3.04) * mm});
            skLineSegment(sketch, "E2060", {"start": v(57.7, -3.04) * mm, "end": v(63.77, -3.04) * mm});
            skLineSegment(sketch, "E2061", {"start": v(63.77, -3.04) * mm, "end": v(63.77, 0) * mm});
            skLineSegment(sketch, "E2062", {"start": v(63.77, 0) * mm, "end": v(69.84, 0) * mm});
            skLineSegment(sketch, "E2063", {"start": v(69.84, 0) * mm, "end": v(69.84, -3.04) * mm});
            skLineSegment(sketch, "E2064", {"start": v(69.84, -3.04) * mm, "end": v(75.91, -3.04) * mm});
            skLineSegment(sketch, "E2065", {"start": v(75.91, -3.04) * mm, "end": v(75.91, 0) * mm});
            skLineSegment(sketch, "E2066", {"start": v(75.91, 0) * mm, "end": v(83.5, 0) * mm});
            skLineSegment(sketch, "E2067", {"start": v(83.5, 0) * mm, "end": v(83.5, -3.04) * mm});
            skLineSegment(sketch, "E2068", {"start": v(83.5, -3.04) * mm, "end": v(88.06, -3.04) * mm});
            skLineSegment(sketch, "E2069", {"start": v(88.06, -3.04) * mm, "end": v(88.06, -7.6) * mm});
            skLineSegment(sketch, "E2070", {"start": v(88.06, -7.6) * mm, "end": v(91.1, -7.6) * mm});
            skLineSegment(sketch, "E2071", {"start": v(91.1, -7.6) * mm, "end": v(91.1, -15.18) * mm});
            skLineSegment(sketch, "E2072", {"start": v(91.1, -15.18) * mm, "end": v(88.06, -15.18) * mm});
            skLineSegment(sketch, "E2073", {"start": v(88.06, -15.18) * mm, "end": v(88.06, -21.26) * mm});
            skLineSegment(sketch, "E2074", {"start": v(88.06, -21.26) * mm, "end": v(91.1, -21.26) * mm});
            skLineSegment(sketch, "E2075", {"start": v(91.1, -21.26) * mm, "end": v(91.1, -27.33) * mm});
            skLineSegment(sketch, "E2076", {"start": v(91.1, -27.33) * mm, "end": v(88.06, -27.33) * mm});
            skLineSegment(sketch, "E2077", {"start": v(88.06, -27.33) * mm, "end": v(88.06, -33.4) * mm});
            skLineSegment(sketch, "E2078", {"start": v(88.06, -33.4) * mm, "end": v(91.1, -33.4) * mm});
            skLineSegment(sketch, "E2079", {"start": v(91.1, -33.4) * mm, "end": v(91.1, -39.47) * mm});
            skLineSegment(sketch, "E2080", {"start": v(91.1, -39.47) * mm, "end": v(88.06, -39.47) * mm});
            skLineSegment(sketch, "E2081", {"start": v(88.06, -39.47) * mm, "end": v(88.06, -45.55) * mm});
            skLineSegment(sketch, "E2082", {"start": v(88.06, -45.55) * mm, "end": v(91.1, -45.55) * mm});
            skLineSegment(sketch, "E2083", {"start": v(91.1, -45.55) * mm, "end": v(91.1, -51.62) * mm});
            skLineSegment(sketch, "E2084", {"start": v(91.1, -51.62) * mm, "end": v(88.06, -51.62) * mm});
            skLineSegment(sketch, "E2085", {"start": v(88.06, -51.62) * mm, "end": v(88.06, -57.7) * mm});
            skLineSegment(sketch, "E2086", {"start": v(88.06, -57.7) * mm, "end": v(91.1, -57.7) * mm});
            skLineSegment(sketch, "E2087", {"start": v(91.1, -57.7) * mm, "end": v(91.1, -63.76) * mm});
            skLineSegment(sketch, "E2088", {"start": v(91.1, -63.76) * mm, "end": v(88.06, -63.76) * mm});
            skLineSegment(sketch, "E2089", {"start": v(88.06, -63.76) * mm, "end": v(88.06, -69.84) * mm});
            skLineSegment(sketch, "E2090", {"start": v(88.06, -69.84) * mm, "end": v(91.1, -69.84) * mm});
            skLineSegment(sketch, "E2091", {"start": v(91.1, -69.84) * mm, "end": v(91.1, -75.91) * mm});
            skLineSegment(sketch, "E2092", {"start": v(91.1, -75.91) * mm, "end": v(88.06, -75.91) * mm});
            skLineSegment(sketch, "E2093", {"start": v(88.06, -75.91) * mm, "end": v(88.06, -81.99) * mm});
            skLineSegment(sketch, "E2094", {"start": v(88.06, -81.99) * mm, "end": v(91.1, -81.99) * mm});
            skLineSegment(sketch, "E2095", {"start": v(91.1, -81.99) * mm, "end": v(91.1, -88.06) * mm});
            skLineSegment(sketch, "E2096", {"start": v(91.1, -88.06) * mm, "end": v(88.06, -88.06) * mm});
            skLineSegment(sketch, "E2097", {"start": v(88.06, -88.06) * mm, "end": v(88.06, -94.13) * mm});
            skLineSegment(sketch, "E2098", {"start": v(88.06, -94.13) * mm, "end": v(91.1, -94.13) * mm});
            skLineSegment(sketch, "E2099", {"start": v(91.1, -94.13) * mm, "end": v(91.1, -100.2) * mm});
            skLineSegment(sketch, "E2100", {"start": v(91.1, -100.2) * mm, "end": v(88.06, -100.2) * mm});
            skLineSegment(sketch, "E2101", {"start": v(88.06, -100.2) * mm, "end": v(88.06, -106.28) * mm});
            skLineSegment(sketch, "E2102", {"start": v(88.06, -106.28) * mm, "end": v(91.1, -106.28) * mm});
            skLineSegment(sketch, "E2103", {"start": v(91.1, -106.28) * mm, "end": v(91.1, -112.35) * mm});
            skLineSegment(sketch, "E2104", {"start": v(91.1, -112.35) * mm, "end": v(88.06, -112.35) * mm});
            skLineSegment(sketch, "E2105", {"start": v(88.06, -112.35) * mm, "end": v(88.06, -118.42) * mm});
            skLineSegment(sketch, "E2106", {"start": v(88.06, -118.42) * mm, "end": v(91.1, -118.42) * mm});
            skLineSegment(sketch, "E2107", {"start": v(91.1, -118.42) * mm, "end": v(91.1, -124.5) * mm});
            skLineSegment(sketch, "E2108", {"start": v(91.1, -124.5) * mm, "end": v(88.06, -124.5) * mm});
            skLineSegment(sketch, "E2109", {"start": v(88.06, -124.5) * mm, "end": v(88.06, -130.57) * mm});
            skLineSegment(sketch, "E2110", {"start": v(88.06, -130.57) * mm, "end": v(91.1, -130.57) * mm});
            skLineSegment(sketch, "E2111", {"start": v(91.1, -130.57) * mm, "end": v(91.1, -136.64) * mm});
            skLineSegment(sketch, "E2112", {"start": v(91.1, -136.64) * mm, "end": v(88.06, -136.64) * mm});
            skLineSegment(sketch, "E2113", {"start": v(88.06, -136.64) * mm, "end": v(88.06, -142.71) * mm});
            skLineSegment(sketch, "E2114", {"start": v(88.06, -142.71) * mm, "end": v(91.1, -142.71) * mm});
            skLineSegment(sketch, "E2115", {"start": v(91.1, -142.71) * mm, "end": v(91.1, -148.78) * mm});
            skLineSegment(sketch, "E2116", {"start": v(91.1, -148.78) * mm, "end": v(88.06, -148.78) * mm});
            skLineSegment(sketch, "E2117", {"start": v(88.06, -148.78) * mm, "end": v(88.06, -154.86) * mm});
            skLineSegment(sketch, "E2118", {"start": v(88.06, -154.86) * mm, "end": v(91.1, -154.86) * mm});
            skLineSegment(sketch, "E2119", {"start": v(91.1, -154.86) * mm, "end": v(91.1, -160.93) * mm});
            skLineSegment(sketch, "E2120", {"start": v(91.1, -160.93) * mm, "end": v(88.06, -160.93) * mm});
            skLineSegment(sketch, "E2121", {"start": v(88.06, -160.93) * mm, "end": v(88.06, -167) * mm});
            skLineSegment(sketch, "E2122", {"start": v(88.06, -167) * mm, "end": v(91.1, -167) * mm});
            skLineSegment(sketch, "E2123", {"start": v(91.1, -167) * mm, "end": v(91.1, -174.6) * mm});
            skLineSegment(sketch, "E2124", {"start": v(91.1, -174.6) * mm, "end": v(88.06, -174.6) * mm});
            skLineSegment(sketch, "E2125", {"start": v(88.06, -174.6) * mm, "end": v(88.06, -179.15) * mm});
            skLineSegment(sketch, "E2126", {"start": v(88.06, -179.15) * mm, "end": v(83.5, -179.15) * mm});
            skLineSegment(sketch, "E2127", {"start": v(83.5, -179.15) * mm, "end": v(83.5, -182.19) * mm});
            skLineSegment(sketch, "E2128", {"start": v(83.5, -182.19) * mm, "end": v(75.91, -182.19) * mm});
            skLineSegment(sketch, "E2129", {"start": v(75.91, -182.19) * mm, "end": v(75.91, -179.15) * mm});
            skLineSegment(sketch, "E2130", {"start": v(75.91, -179.15) * mm, "end": v(69.84, -179.15) * mm});
            skLineSegment(sketch, "E2131", {"start": v(69.84, -179.15) * mm, "end": v(69.84, -182.19) * mm});
            skLineSegment(sketch, "E2132", {"start": v(69.84, -182.19) * mm, "end": v(63.77, -182.19) * mm});
            skLineSegment(sketch, "E2133", {"start": v(63.77, -182.19) * mm, "end": v(63.77, -179.15) * mm});
            skLineSegment(sketch, "E2134", {"start": v(63.77, -179.15) * mm, "end": v(57.7, -179.15) * mm});
            skLineSegment(sketch, "E2135", {"start": v(57.7, -179.15) * mm, "end": v(57.7, -182.19) * mm});
            skLineSegment(sketch, "E2136", {"start": v(57.7, -182.19) * mm, "end": v(51.62, -182.19) * mm});
            skLineSegment(sketch, "E2137", {"start": v(51.62, -182.19) * mm, "end": v(51.62, -179.15) * mm});
            skLineSegment(sketch, "E2138", {"start": v(51.62, -179.15) * mm, "end": v(45.54, -179.15) * mm});
            skLineSegment(sketch, "E2139", {"start": v(45.54, -179.15) * mm, "end": v(45.54, -182.19) * mm});
            skLineSegment(sketch, "E2140", {"start": v(45.54, -182.19) * mm, "end": v(39.47, -182.19) * mm});
            skLineSegment(sketch, "E2141", {"start": v(39.47, -182.19) * mm, "end": v(39.47, -179.15) * mm});
            skLineSegment(sketch, "E2142", {"start": v(39.47, -179.15) * mm, "end": v(33.4, -179.15) * mm});
            skLineSegment(sketch, "E2143", {"start": v(33.4, -179.15) * mm, "end": v(33.4, -182.19) * mm});
            skLineSegment(sketch, "E2144", {"start": v(33.4, -182.19) * mm, "end": v(27.33, -182.19) * mm});
            skLineSegment(sketch, "E2145", {"start": v(27.33, -182.19) * mm, "end": v(27.33, -179.15) * mm});
            skLineSegment(sketch, "E2146", {"start": v(27.33, -179.15) * mm, "end": v(21.25, -179.15) * mm});
            skLineSegment(sketch, "E2147", {"start": v(21.25, -179.15) * mm, "end": v(21.25, -182.19) * mm});
            skLineSegment(sketch, "E2148", {"start": v(21.25, -182.19) * mm, "end": v(15.18, -182.19) * mm});
            skLineSegment(sketch, "E2149", {"start": v(15.18, -182.19) * mm, "end": v(15.18, -179.15) * mm});
            skLineSegment(sketch, "E2150", {"start": v(15.18, -179.15) * mm, "end": v(9.1, -179.15) * mm});
            skLineSegment(sketch, "E2151", {"start": v(9.1, -179.15) * mm, "end": v(9.1, -182.19) * mm});
            skLineSegment(sketch, "E2152", {"start": v(9.1, -182.19) * mm, "end": v(3.04, -182.19) * mm});
            skLineSegment(sketch, "E2153", {"start": v(3.04, -182.19) * mm, "end": v(3.04, -179.15) * mm});
            skLineSegment(sketch, "E2154", {"start": v(3.04, -179.15) * mm, "end": v(-3.04, -179.15) * mm});
            skLineSegment(sketch, "E2155", {"start": v(-3.04, -179.15) * mm, "end": v(-3.04, -182.19) * mm});
            skLineSegment(sketch, "E2156", {"start": v(-3.04, -182.19) * mm, "end": v(-9.1, -182.19) * mm});
            skLineSegment(sketch, "E2157", {"start": v(-9.1, -182.19) * mm, "end": v(-9.1, -179.15) * mm});
            skLineSegment(sketch, "E2158", {"start": v(-9.1, -179.15) * mm, "end": v(-15.18, -179.15) * mm});
            skLineSegment(sketch, "E2159", {"start": v(-15.18, -179.15) * mm, "end": v(-15.18, -182.19) * mm});
            skLineSegment(sketch, "E2160", {"start": v(-15.18, -182.19) * mm, "end": v(-21.25, -182.19) * mm});
            skLineSegment(sketch, "E2161", {"start": v(-21.25, -182.19) * mm, "end": v(-21.25, -179.15) * mm});
            skLineSegment(sketch, "E2162", {"start": v(-21.25, -179.15) * mm, "end": v(-27.33, -179.15) * mm});
            skLineSegment(sketch, "E2163", {"start": v(-27.33, -179.15) * mm, "end": v(-27.33, -182.19) * mm});
            skLineSegment(sketch, "E2164", {"start": v(-27.33, -182.19) * mm, "end": v(-33.4, -182.19) * mm});
            skLineSegment(sketch, "E2165", {"start": v(-33.4, -182.19) * mm, "end": v(-33.4, -179.15) * mm});
            skLineSegment(sketch, "E2166", {"start": v(-33.4, -179.15) * mm, "end": v(-39.47, -179.15) * mm});
            skLineSegment(sketch, "E2167", {"start": v(-39.47, -179.15) * mm, "end": v(-39.47, -182.19) * mm});
            skLineSegment(sketch, "E2168", {"start": v(-39.47, -182.19) * mm, "end": v(-45.55, -182.19) * mm});
            skLineSegment(sketch, "E2169", {"start": v(-45.55, -182.19) * mm, "end": v(-45.55, -179.15) * mm});
            skLineSegment(sketch, "E2170", {"start": v(-45.55, -179.15) * mm, "end": v(-51.62, -179.15) * mm});
            skLineSegment(sketch, "E2171", {"start": v(-51.62, -179.15) * mm, "end": v(-51.62, -182.19) * mm});
            skLineSegment(sketch, "E2172", {"start": v(-51.62, -182.19) * mm, "end": v(-57.7, -182.19) * mm});
            skLineSegment(sketch, "E2173", {"start": v(-57.7, -182.19) * mm, "end": v(-57.7, -179.15) * mm});
            skLineSegment(sketch, "E2174", {"start": v(-57.7, -179.15) * mm, "end": v(-63.77, -179.15) * mm});
            skLineSegment(sketch, "E2175", {"start": v(-63.77, -179.15) * mm, "end": v(-63.77, -182.19) * mm});
            skLineSegment(sketch, "E2176", {"start": v(-63.77, -182.19) * mm, "end": v(-69.84, -182.19) * mm});
            skLineSegment(sketch, "E2177", {"start": v(-69.84, -182.19) * mm, "end": v(-69.84, -179.15) * mm});
            skLineSegment(sketch, "E2178", {"start": v(-69.84, -179.15) * mm, "end": v(-75.91, -179.15) * mm});
            skLineSegment(sketch, "E2179", {"start": v(-75.91, -179.15) * mm, "end": v(-75.91, -182.19) * mm});
            skLineSegment(sketch, "E2180", {"start": v(-75.91, -182.19) * mm, "end": v(-83.5, -182.19) * mm});
            skLineSegment(sketch, "E2181", {"start": v(-83.5, -182.19) * mm, "end": v(-83.5, -179.15) * mm});
            skLineSegment(sketch, "E2182", {"start": v(-83.5, -179.15) * mm, "end": v(-88.06, -179.15) * mm});
            skLineSegment(sketch, "E2183", {"start": v(-88.06, -179.15) * mm, "end": v(-88.06, -174.6) * mm});
            skLineSegment(sketch, "E2184", {"start": v(-88.06, -174.6) * mm, "end": v(-91.1, -174.6) * mm});
            skLineSegment(sketch, "E2185", {"start": v(-91.1, -174.6) * mm, "end": v(-91.1, -167) * mm});
            skLineSegment(sketch, "E2186", {"start": v(-91.1, -167) * mm, "end": v(-88.06, -167) * mm});
            skLineSegment(sketch, "E2187", {"start": v(-88.06, -167) * mm, "end": v(-88.06, -160.93) * mm});
            skLineSegment(sketch, "E2188", {"start": v(-88.06, -160.93) * mm, "end": v(-91.1, -160.93) * mm});
            skLineSegment(sketch, "E2189", {"start": v(-91.1, -160.93) * mm, "end": v(-91.1, -154.86) * mm});
            skLineSegment(sketch, "E2190", {"start": v(-91.1, -154.86) * mm, "end": v(-88.06, -154.86) * mm});
            skLineSegment(sketch, "E2191", {"start": v(-88.06, -154.86) * mm, "end": v(-88.06, -148.78) * mm});
            skLineSegment(sketch, "E2192", {"start": v(-88.06, -148.78) * mm, "end": v(-91.1, -148.78) * mm});
            skLineSegment(sketch, "E2193", {"start": v(-91.1, -148.78) * mm, "end": v(-91.1, -142.71) * mm});
            skLineSegment(sketch, "E2194", {"start": v(-91.1, -142.71) * mm, "end": v(-88.06, -142.71) * mm});
            skLineSegment(sketch, "E2195", {"start": v(-88.06, -142.71) * mm, "end": v(-88.06, -136.64) * mm});
            skLineSegment(sketch, "E2196", {"start": v(-88.06, -136.64) * mm, "end": v(-91.1, -136.64) * mm});
            skLineSegment(sketch, "E2197", {"start": v(-91.1, -136.64) * mm, "end": v(-91.1, -130.57) * mm});
            skLineSegment(sketch, "E2198", {"start": v(-91.1, -130.57) * mm, "end": v(-88.06, -130.57) * mm});
            skLineSegment(sketch, "E2199", {"start": v(-88.06, -130.57) * mm, "end": v(-88.06, -124.5) * mm});
            skLineSegment(sketch, "E2200", {"start": v(-88.06, -124.5) * mm, "end": v(-91.1, -124.5) * mm});
            skLineSegment(sketch, "E2201", {"start": v(-91.1, -124.5) * mm, "end": v(-91.1, -118.42) * mm});
            skLineSegment(sketch, "E2202", {"start": v(-91.1, -118.42) * mm, "end": v(-88.06, -118.42) * mm});
            skLineSegment(sketch, "E2203", {"start": v(-88.06, -118.42) * mm, "end": v(-88.06, -112.35) * mm});
            skLineSegment(sketch, "E2204", {"start": v(-88.06, -112.35) * mm, "end": v(-91.1, -112.35) * mm});
            skLineSegment(sketch, "E2205", {"start": v(-91.1, -112.35) * mm, "end": v(-91.1, -106.28) * mm});
            skLineSegment(sketch, "E2206", {"start": v(-91.1, -106.28) * mm, "end": v(-88.06, -106.28) * mm});
            skLineSegment(sketch, "E2207", {"start": v(-88.06, -106.28) * mm, "end": v(-88.06, -100.2) * mm});
            skLineSegment(sketch, "E2208", {"start": v(-88.06, -100.2) * mm, "end": v(-91.1, -100.2) * mm});
            skLineSegment(sketch, "E2209", {"start": v(-91.1, -100.2) * mm, "end": v(-91.1, -94.13) * mm});
            skLineSegment(sketch, "E2210", {"start": v(-91.1, -94.13) * mm, "end": v(-88.06, -94.13) * mm});
            skLineSegment(sketch, "E2211", {"start": v(-88.06, -94.13) * mm, "end": v(-88.06, -88.06) * mm});
            skLineSegment(sketch, "E2212", {"start": v(-88.06, -88.06) * mm, "end": v(-91.1, -88.06) * mm});
            skLineSegment(sketch, "E2213", {"start": v(-91.1, -88.06) * mm, "end": v(-91.1, -81.99) * mm});
            skLineSegment(sketch, "E2214", {"start": v(-91.1, -81.99) * mm, "end": v(-88.06, -81.99) * mm});
            skLineSegment(sketch, "E2215", {"start": v(-88.06, -81.99) * mm, "end": v(-88.06, -75.91) * mm});
            skLineSegment(sketch, "E2216", {"start": v(-88.06, -75.91) * mm, "end": v(-91.1, -75.91) * mm});
            skLineSegment(sketch, "E2217", {"start": v(-91.1, -75.91) * mm, "end": v(-91.1, -69.84) * mm});
            skLineSegment(sketch, "E2218", {"start": v(-91.1, -69.84) * mm, "end": v(-88.06, -69.84) * mm});
            skLineSegment(sketch, "E2219", {"start": v(-88.06, -69.84) * mm, "end": v(-88.06, -63.76) * mm});
            skLineSegment(sketch, "E2220", {"start": v(-88.06, -63.76) * mm, "end": v(-91.1, -63.76) * mm});
            skLineSegment(sketch, "E2221", {"start": v(-91.1, -63.76) * mm, "end": v(-91.1, -57.7) * mm});
            skLineSegment(sketch, "E2222", {"start": v(-91.1, -57.7) * mm, "end": v(-88.06, -57.7) * mm});
            skLineSegment(sketch, "E2223", {"start": v(-88.06, -57.7) * mm, "end": v(-88.06, -51.62) * mm});
            skLineSegment(sketch, "E2224", {"start": v(-88.06, -51.62) * mm, "end": v(-91.1, -51.62) * mm});
            skLineSegment(sketch, "E2225", {"start": v(-91.1, -51.62) * mm, "end": v(-91.1, -45.55) * mm});
            skLineSegment(sketch, "E2226", {"start": v(-91.1, -45.55) * mm, "end": v(-88.06, -45.55) * mm});
            skLineSegment(sketch, "E2227", {"start": v(-88.06, -45.55) * mm, "end": v(-88.06, -39.47) * mm});
            skLineSegment(sketch, "E2228", {"start": v(-88.06, -39.47) * mm, "end": v(-91.1, -39.47) * mm});
            skLineSegment(sketch, "E2229", {"start": v(-91.1, -39.47) * mm, "end": v(-91.1, -33.4) * mm});
            skLineSegment(sketch, "E2230", {"start": v(-91.1, -33.4) * mm, "end": v(-88.06, -33.4) * mm});
            skLineSegment(sketch, "E2231", {"start": v(-88.06, -33.4) * mm, "end": v(-88.06, -27.33) * mm});
            skLineSegment(sketch, "E2232", {"start": v(-88.06, -27.33) * mm, "end": v(-91.1, -27.33) * mm});
            skLineSegment(sketch, "E2233", {"start": v(-91.1, -27.33) * mm, "end": v(-91.1, -21.26) * mm});
            skLineSegment(sketch, "E2234", {"start": v(-91.1, -21.26) * mm, "end": v(-88.06, -21.26) * mm});
            skLineSegment(sketch, "E2235", {"start": v(-88.06, -21.26) * mm, "end": v(-88.06, -15.18) * mm});
            skLineSegment(sketch, "E2236", {"start": v(-88.06, -15.18) * mm, "end": v(-91.1, -15.18) * mm});
            skLineSegment(sketch, "E2237", {"start": v(-91.1, -15.18) * mm, "end": v(-91.1, -7.6) * mm});
            skLineSegment(sketch, "E2238", {"start": v(-91.1, -7.6) * mm, "end": v(-88.06, -7.6) * mm});
            skLineSegment(sketch, "E2239", {"start": v(-88.06, -7.6) * mm, "end": v(-88.06, -3.04) * mm});
            skSolve(sketch);
        }
        {
            var Q0;
            Q0=makeQuery(id+"F0.imprint","IMPRINT",FACE,{"disambiguationData":[TD([[makeQuery(id+"F0.imprint","IMPRINT",EDGE,{"derivedFrom":sQuery(id+"F0.wireOp",EDGE,"E872")}),-1.0]])]});
            var Q1;
            Q1=makeQuery(id+"F0.imprint","IMPRINT",FACE,{"disambiguationData":[TD([[makeQuery(id+"F0.imprint","IMPRINT",EDGE,{"derivedFrom":sQuery(id+"F0.wireOp",EDGE,"E0")}),-1.0]])]});
            var Q2;
            Q2=makeQuery(id+"F0.imprint","IMPRINT",FACE,{"disambiguationData":[TD([[makeQuery(id+"F0.imprint","IMPRINT",EDGE,{"derivedFrom":sQuery(id+"F0.wireOp",EDGE,"E436")}),-1.0]])]});
            var Q3;
            Q3=makeQuery(id+"F0.imprint","IMPRINT",FACE,{"disambiguationData":[TD([[makeQuery(id+"F0.imprint","IMPRINT",EDGE,{"derivedFrom":sQuery(id+"F0.wireOp",EDGE,"E1744")}),1.0]])]});
            var Q4;
            Q4=makeQuery(id+"F0.imprint","IMPRINT",FACE,{"disambiguationData":[TD([[makeQuery(id+"F0.imprint","IMPRINT",EDGE,{"derivedFrom":sQuery(id+"F0.wireOp",EDGE,"E2012")}),-1.0]])]});
            var Q5;
            Q5=makeQuery(id+"F0.imprint","IMPRINT",FACE,{"disambiguationData":[TD([[makeQuery(id+"F0.imprint","IMPRINT",EDGE,{"derivedFrom":sQuery(id+"F0.wireOp",EDGE,"E1308")}),-1.0]])]});
            extrude(context, id + "F1", {"entities" : qUnion([Q0, Q1, Q2, Q3, Q4, Q5]), "depth" : 3 * mm});
        }
    });
